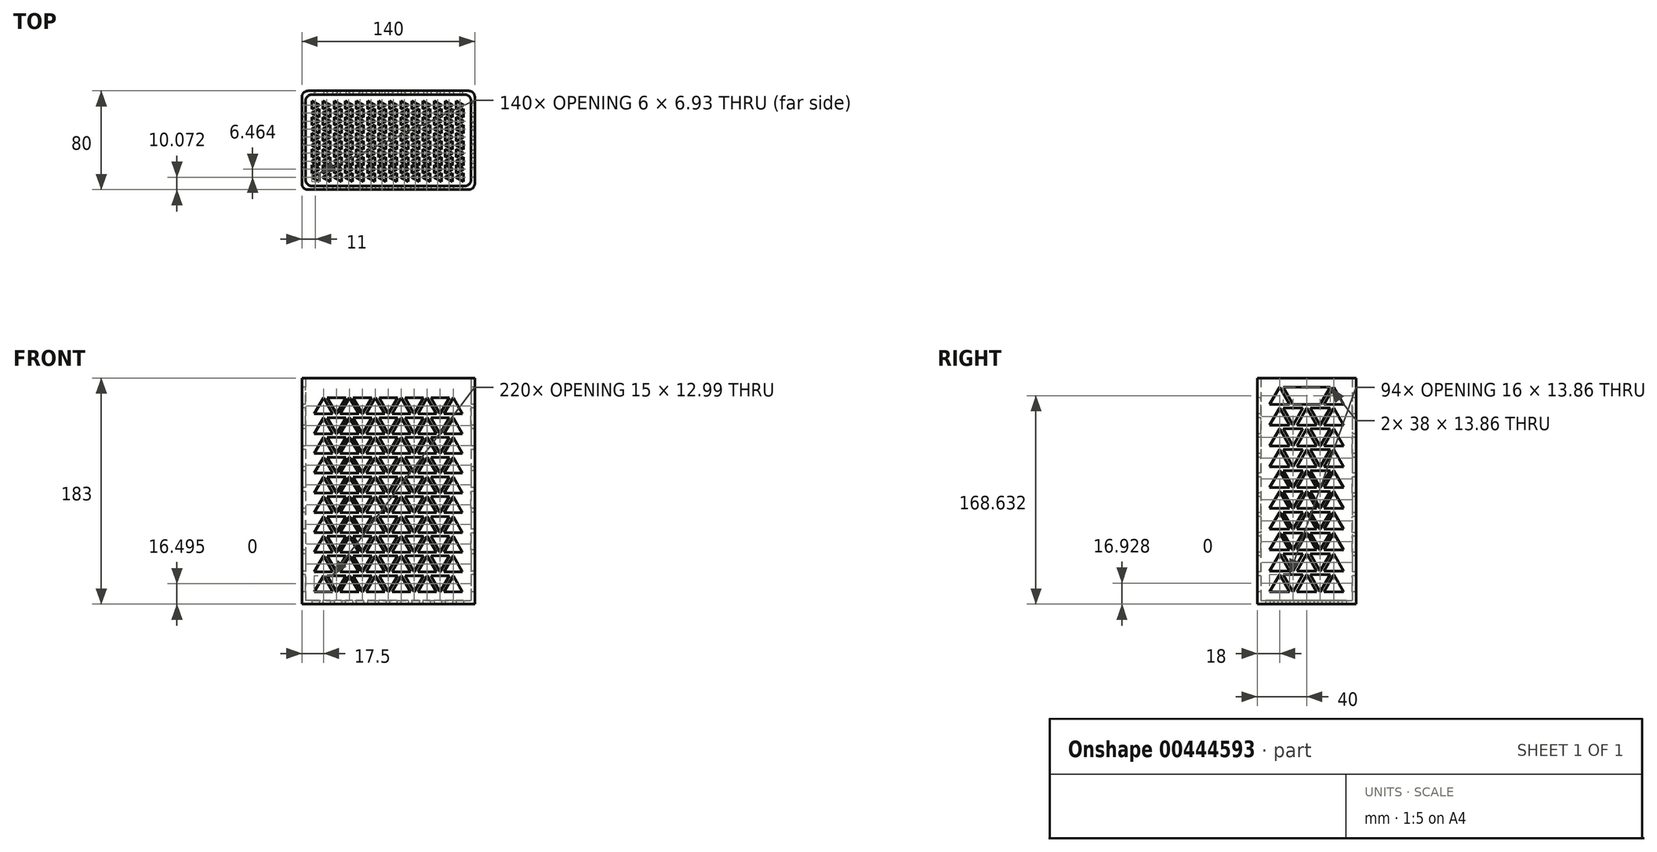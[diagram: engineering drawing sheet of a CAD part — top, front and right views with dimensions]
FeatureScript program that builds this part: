
annotation { "Feature Type Name" : "Feature", "Feature Type Description" : "" }
export const myFeature = defineFeature(function(context is Context, id is Id, definition is map)
    precondition{}
    {
        {
            var Q0;
            Q0=qCreatedBy(makeId("Top.planeOp"),FACE);
            var sketch = newSketch(context, id + "F0", { "sketchPlane" : qUnion([Q0])});
            skLineSegment(sketch, "E0.bottom", {"start": v(-70, 40) * mm, "end": v(70, 40) * mm});
            skLineSegment(sketch, "E0.top", {"start": v(-70, -40) * mm, "end": v(70, -40) * mm});
            skLineSegment(sketch, "E0.left", {"start": v(-70, 40) * mm, "end": v(-70, -40) * mm});
            skLineSegment(sketch, "E0.right", {"start": v(70, 40) * mm, "end": v(70, -40) * mm});
            skPoint(sketch, "E1", {"position": v(0, 40) * mm});
            skPoint(sketch, "E2", {"position": v(70, 0) * mm});
            skCircle(sketch, "E3.cCircle", {"center": v(-58, 22.07) * mm, "radius": 2 * mm, "construction": true});
            skLineSegment(sketch, "E3.0", {"start": v(-56, 25.54) * mm, "end": v(-56, 18.6) * mm});
            skLineSegment(sketch, "E3.1", {"start": v(-56, 18.6) * mm, "end": v(-62, 22.07) * mm});
            skLineSegment(sketch, "E3.2", {"start": v(-62, 22.07) * mm, "end": v(-56, 25.54) * mm});
            skPoint(sketch, "E3.0.midPoint", {"position": v(-56, 22.07) * mm});
            skCircle(sketch, "E4.cCircle", {"center": v(-60, 28.54) * mm, "radius": 2 * mm, "construction": true});
            skLineSegment(sketch, "E4.0", {"start": v(-62, 25.07) * mm, "end": v(-62, 32) * mm});
            skLineSegment(sketch, "E4.1", {"start": v(-62, 32) * mm, "end": v(-56, 28.54) * mm});
            skLineSegment(sketch, "E4.2", {"start": v(-56, 28.54) * mm, "end": v(-62, 25.07) * mm});
            skPoint(sketch, "E4.0.midPoint", {"position": v(-62, 28.54) * mm});
            skCircle(sketch, "E5.0.1.0", {"center": v(-58, 9.07) * mm, "radius": 2 * mm, "construction": true});
            skLineSegment(sketch, "E5.0.1.1", {"start": v(-56, 12.54) * mm, "end": v(-56, 5.6) * mm});
            skLineSegment(sketch, "E5.0.1.2", {"start": v(-56, 5.6) * mm, "end": v(-62, 9.07) * mm});
            skLineSegment(sketch, "E5.0.1.3", {"start": v(-62, 9.07) * mm, "end": v(-56, 12.54) * mm});
            skCircle(sketch, "E5.0.1.4", {"center": v(-60, 15.54) * mm, "radius": 2 * mm, "construction": true});
            skLineSegment(sketch, "E5.0.1.5", {"start": v(-62, 12.07) * mm, "end": v(-62, 19) * mm});
            skLineSegment(sketch, "E5.0.1.6", {"start": v(-62, 19) * mm, "end": v(-56, 15.54) * mm});
            skLineSegment(sketch, "E5.0.1.7", {"start": v(-56, 15.54) * mm, "end": v(-62, 12.07) * mm});
            skPoint(sketch, "E5.0.1.8", {"position": v(-62, 15.54) * mm});
            skPoint(sketch, "E5.0.1.9", {"position": v(-56, 9.07) * mm});
            skCircle(sketch, "E5.0.2.0", {"center": v(-58, -3.93) * mm, "radius": 2 * mm, "construction": true});
            skLineSegment(sketch, "E5.0.2.1", {"start": v(-56, -0.46) * mm, "end": v(-56, -7.4) * mm});
            skLineSegment(sketch, "E5.0.2.2", {"start": v(-56, -7.4) * mm, "end": v(-62, -3.93) * mm});
            skLineSegment(sketch, "E5.0.2.3", {"start": v(-62, -3.93) * mm, "end": v(-56, -0.46) * mm});
            skCircle(sketch, "E5.0.2.4", {"center": v(-60, 2.54) * mm, "radius": 2 * mm, "construction": true});
            skLineSegment(sketch, "E5.0.2.5", {"start": v(-62, -0.93) * mm, "end": v(-62, 6) * mm});
            skLineSegment(sketch, "E5.0.2.6", {"start": v(-62, 6) * mm, "end": v(-56, 2.54) * mm});
            skLineSegment(sketch, "E5.0.2.7", {"start": v(-56, 2.54) * mm, "end": v(-62, -0.93) * mm});
            skPoint(sketch, "E5.0.2.8", {"position": v(-62, 2.54) * mm});
            skPoint(sketch, "E5.0.2.9", {"position": v(-56, -3.93) * mm});
            skCircle(sketch, "E5.0.3.0", {"center": v(-58, -16.93) * mm, "radius": 2 * mm, "construction": true});
            skLineSegment(sketch, "E5.0.3.1", {"start": v(-56, -13.46) * mm, "end": v(-56, -20.4) * mm});
            skLineSegment(sketch, "E5.0.3.2", {"start": v(-56, -20.4) * mm, "end": v(-62, -16.93) * mm});
            skLineSegment(sketch, "E5.0.3.3", {"start": v(-62, -16.93) * mm, "end": v(-56, -13.46) * mm});
            skCircle(sketch, "E5.0.3.4", {"center": v(-60, -10.46) * mm, "radius": 2 * mm, "construction": true});
            skLineSegment(sketch, "E5.0.3.5", {"start": v(-62, -13.93) * mm, "end": v(-62, -7) * mm});
            skLineSegment(sketch, "E5.0.3.6", {"start": v(-62, -7) * mm, "end": v(-56, -10.46) * mm});
            skLineSegment(sketch, "E5.0.3.7", {"start": v(-56, -10.46) * mm, "end": v(-62, -13.93) * mm});
            skPoint(sketch, "E5.0.3.8", {"position": v(-62, -10.46) * mm});
            skPoint(sketch, "E5.0.3.9", {"position": v(-56, -16.93) * mm});
            skCircle(sketch, "E5.0.4.0", {"center": v(-58, -29.93) * mm, "radius": 2 * mm, "construction": true});
            skLineSegment(sketch, "E5.0.4.1", {"start": v(-56, -26.46) * mm, "end": v(-56, -33.4) * mm});
            skLineSegment(sketch, "E5.0.4.2", {"start": v(-56, -33.4) * mm, "end": v(-62, -29.93) * mm});
            skLineSegment(sketch, "E5.0.4.3", {"start": v(-62, -29.93) * mm, "end": v(-56, -26.46) * mm});
            skCircle(sketch, "E5.0.4.4", {"center": v(-60, -23.46) * mm, "radius": 2 * mm, "construction": true});
            skLineSegment(sketch, "E5.0.4.5", {"start": v(-62, -26.93) * mm, "end": v(-62, -20) * mm});
            skLineSegment(sketch, "E5.0.4.6", {"start": v(-62, -20) * mm, "end": v(-56, -23.46) * mm});
            skLineSegment(sketch, "E5.0.4.7", {"start": v(-56, -23.46) * mm, "end": v(-62, -26.93) * mm});
            skPoint(sketch, "E5.0.4.8", {"position": v(-62, -23.46) * mm});
            skPoint(sketch, "E5.0.4.9", {"position": v(-56, -29.93) * mm});
            skCircle(sketch, "E5.1.0.0", {"center": v(-49, 22.07) * mm, "radius": 2 * mm, "construction": true});
            skLineSegment(sketch, "E5.1.0.1", {"start": v(-47, 25.54) * mm, "end": v(-47, 18.6) * mm});
            skLineSegment(sketch, "E5.1.0.2", {"start": v(-47, 18.6) * mm, "end": v(-53, 22.07) * mm});
            skLineSegment(sketch, "E5.1.0.3", {"start": v(-53, 22.07) * mm, "end": v(-47, 25.54) * mm});
            skCircle(sketch, "E5.1.0.4", {"center": v(-51, 28.54) * mm, "radius": 2 * mm, "construction": true});
            skLineSegment(sketch, "E5.1.0.5", {"start": v(-53, 25.07) * mm, "end": v(-53, 32) * mm});
            skLineSegment(sketch, "E5.1.0.6", {"start": v(-53, 32) * mm, "end": v(-47, 28.54) * mm});
            skLineSegment(sketch, "E5.1.0.7", {"start": v(-47, 28.54) * mm, "end": v(-53, 25.07) * mm});
            skPoint(sketch, "E5.1.0.8", {"position": v(-53, 28.54) * mm});
            skPoint(sketch, "E5.1.0.9", {"position": v(-47, 22.07) * mm});
            skCircle(sketch, "E5.1.1.0", {"center": v(-49, 9.07) * mm, "radius": 2 * mm, "construction": true});
            skLineSegment(sketch, "E5.1.1.1", {"start": v(-47, 12.54) * mm, "end": v(-47, 5.6) * mm});
            skLineSegment(sketch, "E5.1.1.2", {"start": v(-47, 5.6) * mm, "end": v(-53, 9.07) * mm});
            skLineSegment(sketch, "E5.1.1.3", {"start": v(-53, 9.07) * mm, "end": v(-47, 12.54) * mm});
            skCircle(sketch, "E5.1.1.4", {"center": v(-51, 15.54) * mm, "radius": 2 * mm, "construction": true});
            skLineSegment(sketch, "E5.1.1.5", {"start": v(-53, 12.07) * mm, "end": v(-53, 19) * mm});
            skLineSegment(sketch, "E5.1.1.6", {"start": v(-53, 19) * mm, "end": v(-47, 15.54) * mm});
            skLineSegment(sketch, "E5.1.1.7", {"start": v(-47, 15.54) * mm, "end": v(-53, 12.07) * mm});
            skPoint(sketch, "E5.1.1.8", {"position": v(-53, 15.54) * mm});
            skPoint(sketch, "E5.1.1.9", {"position": v(-47, 9.07) * mm});
            skCircle(sketch, "E5.1.2.0", {"center": v(-49, -3.93) * mm, "radius": 2 * mm, "construction": true});
            skLineSegment(sketch, "E5.1.2.1", {"start": v(-47, -0.46) * mm, "end": v(-47, -7.4) * mm});
            skLineSegment(sketch, "E5.1.2.2", {"start": v(-47, -7.4) * mm, "end": v(-53, -3.93) * mm});
            skLineSegment(sketch, "E5.1.2.3", {"start": v(-53, -3.93) * mm, "end": v(-47, -0.46) * mm});
            skCircle(sketch, "E5.1.2.4", {"center": v(-51, 2.54) * mm, "radius": 2 * mm, "construction": true});
            skLineSegment(sketch, "E5.1.2.5", {"start": v(-53, -0.93) * mm, "end": v(-53, 6) * mm});
            skLineSegment(sketch, "E5.1.2.6", {"start": v(-53, 6) * mm, "end": v(-47, 2.54) * mm});
            skLineSegment(sketch, "E5.1.2.7", {"start": v(-47, 2.54) * mm, "end": v(-53, -0.93) * mm});
            skPoint(sketch, "E5.1.2.8", {"position": v(-53, 2.54) * mm});
            skPoint(sketch, "E5.1.2.9", {"position": v(-47, -3.93) * mm});
            skCircle(sketch, "E5.1.3.0", {"center": v(-49, -16.93) * mm, "radius": 2 * mm, "construction": true});
            skLineSegment(sketch, "E5.1.3.1", {"start": v(-47, -13.46) * mm, "end": v(-47, -20.4) * mm});
            skLineSegment(sketch, "E5.1.3.2", {"start": v(-47, -20.4) * mm, "end": v(-53, -16.93) * mm});
            skLineSegment(sketch, "E5.1.3.3", {"start": v(-53, -16.93) * mm, "end": v(-47, -13.46) * mm});
            skCircle(sketch, "E5.1.3.4", {"center": v(-51, -10.46) * mm, "radius": 2 * mm, "construction": true});
            skLineSegment(sketch, "E5.1.3.5", {"start": v(-53, -13.93) * mm, "end": v(-53, -7) * mm});
            skLineSegment(sketch, "E5.1.3.6", {"start": v(-53, -7) * mm, "end": v(-47, -10.46) * mm});
            skLineSegment(sketch, "E5.1.3.7", {"start": v(-47, -10.46) * mm, "end": v(-53, -13.93) * mm});
            skPoint(sketch, "E5.1.3.8", {"position": v(-53, -10.46) * mm});
            skPoint(sketch, "E5.1.3.9", {"position": v(-47, -16.93) * mm});
            skCircle(sketch, "E5.1.4.0", {"center": v(-49, -29.93) * mm, "radius": 2 * mm, "construction": true});
            skLineSegment(sketch, "E5.1.4.1", {"start": v(-47, -26.46) * mm, "end": v(-47, -33.4) * mm});
            skLineSegment(sketch, "E5.1.4.2", {"start": v(-47, -33.4) * mm, "end": v(-53, -29.93) * mm});
            skLineSegment(sketch, "E5.1.4.3", {"start": v(-53, -29.93) * mm, "end": v(-47, -26.46) * mm});
            skCircle(sketch, "E5.1.4.4", {"center": v(-51, -23.46) * mm, "radius": 2 * mm, "construction": true});
            skLineSegment(sketch, "E5.1.4.5", {"start": v(-53, -26.93) * mm, "end": v(-53, -20) * mm});
            skLineSegment(sketch, "E5.1.4.6", {"start": v(-53, -20) * mm, "end": v(-47, -23.46) * mm});
            skLineSegment(sketch, "E5.1.4.7", {"start": v(-47, -23.46) * mm, "end": v(-53, -26.93) * mm});
            skPoint(sketch, "E5.1.4.8", {"position": v(-53, -23.46) * mm});
            skPoint(sketch, "E5.1.4.9", {"position": v(-47, -29.93) * mm});
            skCircle(sketch, "E5.2.0.0", {"center": v(-40, 22.07) * mm, "radius": 2 * mm, "construction": true});
            skLineSegment(sketch, "E5.2.0.1", {"start": v(-38, 25.54) * mm, "end": v(-38, 18.6) * mm});
            skLineSegment(sketch, "E5.2.0.2", {"start": v(-38, 18.6) * mm, "end": v(-44, 22.07) * mm});
            skLineSegment(sketch, "E5.2.0.3", {"start": v(-44, 22.07) * mm, "end": v(-38, 25.54) * mm});
            skCircle(sketch, "E5.2.0.4", {"center": v(-42, 28.54) * mm, "radius": 2 * mm, "construction": true});
            skLineSegment(sketch, "E5.2.0.5", {"start": v(-44, 25.07) * mm, "end": v(-44, 32) * mm});
            skLineSegment(sketch, "E5.2.0.6", {"start": v(-44, 32) * mm, "end": v(-38, 28.54) * mm});
            skLineSegment(sketch, "E5.2.0.7", {"start": v(-38, 28.54) * mm, "end": v(-44, 25.07) * mm});
            skPoint(sketch, "E5.2.0.8", {"position": v(-44, 28.54) * mm});
            skPoint(sketch, "E5.2.0.9", {"position": v(-38, 22.07) * mm});
            skCircle(sketch, "E5.2.1.0", {"center": v(-40, 9.07) * mm, "radius": 2 * mm, "construction": true});
            skLineSegment(sketch, "E5.2.1.1", {"start": v(-38, 12.54) * mm, "end": v(-38, 5.6) * mm});
            skLineSegment(sketch, "E5.2.1.2", {"start": v(-38, 5.6) * mm, "end": v(-44, 9.07) * mm});
            skLineSegment(sketch, "E5.2.1.3", {"start": v(-44, 9.07) * mm, "end": v(-38, 12.54) * mm});
            skCircle(sketch, "E5.2.1.4", {"center": v(-42, 15.54) * mm, "radius": 2 * mm, "construction": true});
            skLineSegment(sketch, "E5.2.1.5", {"start": v(-44, 12.07) * mm, "end": v(-44, 19) * mm});
            skLineSegment(sketch, "E5.2.1.6", {"start": v(-44, 19) * mm, "end": v(-38, 15.54) * mm});
            skLineSegment(sketch, "E5.2.1.7", {"start": v(-38, 15.54) * mm, "end": v(-44, 12.07) * mm});
            skPoint(sketch, "E5.2.1.8", {"position": v(-44, 15.54) * mm});
            skPoint(sketch, "E5.2.1.9", {"position": v(-38, 9.07) * mm});
            skCircle(sketch, "E5.2.2.0", {"center": v(-40, -3.93) * mm, "radius": 2 * mm, "construction": true});
            skLineSegment(sketch, "E5.2.2.1", {"start": v(-38, -0.46) * mm, "end": v(-38, -7.4) * mm});
            skLineSegment(sketch, "E5.2.2.2", {"start": v(-38, -7.4) * mm, "end": v(-44, -3.93) * mm});
            skLineSegment(sketch, "E5.2.2.3", {"start": v(-44, -3.93) * mm, "end": v(-38, -0.46) * mm});
            skCircle(sketch, "E5.2.2.4", {"center": v(-42, 2.54) * mm, "radius": 2 * mm, "construction": true});
            skLineSegment(sketch, "E5.2.2.5", {"start": v(-44, -0.93) * mm, "end": v(-44, 6) * mm});
            skLineSegment(sketch, "E5.2.2.6", {"start": v(-44, 6) * mm, "end": v(-38, 2.54) * mm});
            skLineSegment(sketch, "E5.2.2.7", {"start": v(-38, 2.54) * mm, "end": v(-44, -0.93) * mm});
            skPoint(sketch, "E5.2.2.8", {"position": v(-44, 2.54) * mm});
            skPoint(sketch, "E5.2.2.9", {"position": v(-38, -3.93) * mm});
            skCircle(sketch, "E5.2.3.0", {"center": v(-40, -16.93) * mm, "radius": 2 * mm, "construction": true});
            skLineSegment(sketch, "E5.2.3.1", {"start": v(-38, -13.46) * mm, "end": v(-38, -20.4) * mm});
            skLineSegment(sketch, "E5.2.3.2", {"start": v(-38, -20.4) * mm, "end": v(-44, -16.93) * mm});
            skLineSegment(sketch, "E5.2.3.3", {"start": v(-44, -16.93) * mm, "end": v(-38, -13.46) * mm});
            skCircle(sketch, "E5.2.3.4", {"center": v(-42, -10.46) * mm, "radius": 2 * mm, "construction": true});
            skLineSegment(sketch, "E5.2.3.5", {"start": v(-44, -13.93) * mm, "end": v(-44, -7) * mm});
            skLineSegment(sketch, "E5.2.3.6", {"start": v(-44, -7) * mm, "end": v(-38, -10.46) * mm});
            skLineSegment(sketch, "E5.2.3.7", {"start": v(-38, -10.46) * mm, "end": v(-44, -13.93) * mm});
            skPoint(sketch, "E5.2.3.8", {"position": v(-44, -10.46) * mm});
            skPoint(sketch, "E5.2.3.9", {"position": v(-38, -16.93) * mm});
            skCircle(sketch, "E5.2.4.0", {"center": v(-40, -29.93) * mm, "radius": 2 * mm, "construction": true});
            skLineSegment(sketch, "E5.2.4.1", {"start": v(-38, -26.46) * mm, "end": v(-38, -33.4) * mm});
            skLineSegment(sketch, "E5.2.4.2", {"start": v(-38, -33.4) * mm, "end": v(-44, -29.93) * mm});
            skLineSegment(sketch, "E5.2.4.3", {"start": v(-44, -29.93) * mm, "end": v(-38, -26.46) * mm});
            skCircle(sketch, "E5.2.4.4", {"center": v(-42, -23.46) * mm, "radius": 2 * mm, "construction": true});
            skLineSegment(sketch, "E5.2.4.5", {"start": v(-44, -26.93) * mm, "end": v(-44, -20) * mm});
            skLineSegment(sketch, "E5.2.4.6", {"start": v(-44, -20) * mm, "end": v(-38, -23.46) * mm});
            skLineSegment(sketch, "E5.2.4.7", {"start": v(-38, -23.46) * mm, "end": v(-44, -26.93) * mm});
            skPoint(sketch, "E5.2.4.8", {"position": v(-44, -23.46) * mm});
            skPoint(sketch, "E5.2.4.9", {"position": v(-38, -29.93) * mm});
            skCircle(sketch, "E5.3.0.0", {"center": v(-31, 22.07) * mm, "radius": 2 * mm, "construction": true});
            skLineSegment(sketch, "E5.3.0.1", {"start": v(-29, 25.54) * mm, "end": v(-29, 18.6) * mm});
            skLineSegment(sketch, "E5.3.0.2", {"start": v(-29, 18.6) * mm, "end": v(-35, 22.07) * mm});
            skLineSegment(sketch, "E5.3.0.3", {"start": v(-35, 22.07) * mm, "end": v(-29, 25.54) * mm});
            skCircle(sketch, "E5.3.0.4", {"center": v(-33, 28.54) * mm, "radius": 2 * mm, "construction": true});
            skLineSegment(sketch, "E5.3.0.5", {"start": v(-35, 25.07) * mm, "end": v(-35, 32) * mm});
            skLineSegment(sketch, "E5.3.0.6", {"start": v(-35, 32) * mm, "end": v(-29, 28.54) * mm});
            skLineSegment(sketch, "E5.3.0.7", {"start": v(-29, 28.54) * mm, "end": v(-35, 25.07) * mm});
            skPoint(sketch, "E5.3.0.8", {"position": v(-35, 28.54) * mm});
            skPoint(sketch, "E5.3.0.9", {"position": v(-29, 22.07) * mm});
            skCircle(sketch, "E5.3.1.0", {"center": v(-31, 9.07) * mm, "radius": 2 * mm, "construction": true});
            skLineSegment(sketch, "E5.3.1.1", {"start": v(-29, 12.54) * mm, "end": v(-29, 5.6) * mm});
            skLineSegment(sketch, "E5.3.1.2", {"start": v(-29, 5.6) * mm, "end": v(-35, 9.07) * mm});
            skLineSegment(sketch, "E5.3.1.3", {"start": v(-35, 9.07) * mm, "end": v(-29, 12.54) * mm});
            skCircle(sketch, "E5.3.1.4", {"center": v(-33, 15.54) * mm, "radius": 2 * mm, "construction": true});
            skLineSegment(sketch, "E5.3.1.5", {"start": v(-35, 12.07) * mm, "end": v(-35, 19) * mm});
            skLineSegment(sketch, "E5.3.1.6", {"start": v(-35, 19) * mm, "end": v(-29, 15.54) * mm});
            skLineSegment(sketch, "E5.3.1.7", {"start": v(-29, 15.54) * mm, "end": v(-35, 12.07) * mm});
            skPoint(sketch, "E5.3.1.8", {"position": v(-35, 15.54) * mm});
            skPoint(sketch, "E5.3.1.9", {"position": v(-29, 9.07) * mm});
            skCircle(sketch, "E5.3.2.0", {"center": v(-31, -3.93) * mm, "radius": 2 * mm, "construction": true});
            skLineSegment(sketch, "E5.3.2.1", {"start": v(-29, -0.46) * mm, "end": v(-29, -7.4) * mm});
            skLineSegment(sketch, "E5.3.2.2", {"start": v(-29, -7.4) * mm, "end": v(-35, -3.93) * mm});
            skLineSegment(sketch, "E5.3.2.3", {"start": v(-35, -3.93) * mm, "end": v(-29, -0.46) * mm});
            skCircle(sketch, "E5.3.2.4", {"center": v(-33, 2.54) * mm, "radius": 2 * mm, "construction": true});
            skLineSegment(sketch, "E5.3.2.5", {"start": v(-35, -0.93) * mm, "end": v(-35, 6) * mm});
            skLineSegment(sketch, "E5.3.2.6", {"start": v(-35, 6) * mm, "end": v(-29, 2.54) * mm});
            skLineSegment(sketch, "E5.3.2.7", {"start": v(-29, 2.54) * mm, "end": v(-35, -0.93) * mm});
            skPoint(sketch, "E5.3.2.8", {"position": v(-35, 2.54) * mm});
            skPoint(sketch, "E5.3.2.9", {"position": v(-29, -3.93) * mm});
            skCircle(sketch, "E5.3.3.0", {"center": v(-31, -16.93) * mm, "radius": 2 * mm, "construction": true});
            skLineSegment(sketch, "E5.3.3.1", {"start": v(-29, -13.46) * mm, "end": v(-29, -20.4) * mm});
            skLineSegment(sketch, "E5.3.3.2", {"start": v(-29, -20.4) * mm, "end": v(-35, -16.93) * mm});
            skLineSegment(sketch, "E5.3.3.3", {"start": v(-35, -16.93) * mm, "end": v(-29, -13.46) * mm});
            skCircle(sketch, "E5.3.3.4", {"center": v(-33, -10.46) * mm, "radius": 2 * mm, "construction": true});
            skLineSegment(sketch, "E5.3.3.5", {"start": v(-35, -13.93) * mm, "end": v(-35, -7) * mm});
            skLineSegment(sketch, "E5.3.3.6", {"start": v(-35, -7) * mm, "end": v(-29, -10.46) * mm});
            skLineSegment(sketch, "E5.3.3.7", {"start": v(-29, -10.46) * mm, "end": v(-35, -13.93) * mm});
            skPoint(sketch, "E5.3.3.8", {"position": v(-35, -10.46) * mm});
            skPoint(sketch, "E5.3.3.9", {"position": v(-29, -16.93) * mm});
            skCircle(sketch, "E5.3.4.0", {"center": v(-31, -29.93) * mm, "radius": 2 * mm, "construction": true});
            skLineSegment(sketch, "E5.3.4.1", {"start": v(-29, -26.46) * mm, "end": v(-29, -33.4) * mm});
            skLineSegment(sketch, "E5.3.4.2", {"start": v(-29, -33.4) * mm, "end": v(-35, -29.93) * mm});
            skLineSegment(sketch, "E5.3.4.3", {"start": v(-35, -29.93) * mm, "end": v(-29, -26.46) * mm});
            skCircle(sketch, "E5.3.4.4", {"center": v(-33, -23.46) * mm, "radius": 2 * mm, "construction": true});
            skLineSegment(sketch, "E5.3.4.5", {"start": v(-35, -26.93) * mm, "end": v(-35, -20) * mm});
            skLineSegment(sketch, "E5.3.4.6", {"start": v(-35, -20) * mm, "end": v(-29, -23.46) * mm});
            skLineSegment(sketch, "E5.3.4.7", {"start": v(-29, -23.46) * mm, "end": v(-35, -26.93) * mm});
            skPoint(sketch, "E5.3.4.8", {"position": v(-35, -23.46) * mm});
            skPoint(sketch, "E5.3.4.9", {"position": v(-29, -29.93) * mm});
            skCircle(sketch, "E5.4.0.0", {"center": v(-22, 22.07) * mm, "radius": 2 * mm, "construction": true});
            skLineSegment(sketch, "E5.4.0.1", {"start": v(-20, 25.54) * mm, "end": v(-20, 18.6) * mm});
            skLineSegment(sketch, "E5.4.0.2", {"start": v(-20, 18.6) * mm, "end": v(-26, 22.07) * mm});
            skLineSegment(sketch, "E5.4.0.3", {"start": v(-26, 22.07) * mm, "end": v(-20, 25.54) * mm});
            skCircle(sketch, "E5.4.0.4", {"center": v(-24, 28.54) * mm, "radius": 2 * mm, "construction": true});
            skLineSegment(sketch, "E5.4.0.5", {"start": v(-26, 25.07) * mm, "end": v(-26, 32) * mm});
            skLineSegment(sketch, "E5.4.0.6", {"start": v(-26, 32) * mm, "end": v(-20, 28.54) * mm});
            skLineSegment(sketch, "E5.4.0.7", {"start": v(-20, 28.54) * mm, "end": v(-26, 25.07) * mm});
            skPoint(sketch, "E5.4.0.8", {"position": v(-26, 28.54) * mm});
            skPoint(sketch, "E5.4.0.9", {"position": v(-20, 22.07) * mm});
            skCircle(sketch, "E5.4.1.0", {"center": v(-22, 9.07) * mm, "radius": 2 * mm, "construction": true});
            skLineSegment(sketch, "E5.4.1.1", {"start": v(-20, 12.54) * mm, "end": v(-20, 5.6) * mm});
            skLineSegment(sketch, "E5.4.1.2", {"start": v(-20, 5.6) * mm, "end": v(-26, 9.07) * mm});
            skLineSegment(sketch, "E5.4.1.3", {"start": v(-26, 9.07) * mm, "end": v(-20, 12.54) * mm});
            skCircle(sketch, "E5.4.1.4", {"center": v(-24, 15.54) * mm, "radius": 2 * mm, "construction": true});
            skLineSegment(sketch, "E5.4.1.5", {"start": v(-26, 12.07) * mm, "end": v(-26, 19) * mm});
            skLineSegment(sketch, "E5.4.1.6", {"start": v(-26, 19) * mm, "end": v(-20, 15.54) * mm});
            skLineSegment(sketch, "E5.4.1.7", {"start": v(-20, 15.54) * mm, "end": v(-26, 12.07) * mm});
            skPoint(sketch, "E5.4.1.8", {"position": v(-26, 15.54) * mm});
            skPoint(sketch, "E5.4.1.9", {"position": v(-20, 9.07) * mm});
            skCircle(sketch, "E5.4.2.0", {"center": v(-22, -3.93) * mm, "radius": 2 * mm, "construction": true});
            skLineSegment(sketch, "E5.4.2.1", {"start": v(-20, -0.46) * mm, "end": v(-20, -7.4) * mm});
            skLineSegment(sketch, "E5.4.2.2", {"start": v(-20, -7.4) * mm, "end": v(-26, -3.93) * mm});
            skLineSegment(sketch, "E5.4.2.3", {"start": v(-26, -3.93) * mm, "end": v(-20, -0.46) * mm});
            skCircle(sketch, "E5.4.2.4", {"center": v(-24, 2.54) * mm, "radius": 2 * mm, "construction": true});
            skLineSegment(sketch, "E5.4.2.5", {"start": v(-26, -0.93) * mm, "end": v(-26, 6) * mm});
            skLineSegment(sketch, "E5.4.2.6", {"start": v(-26, 6) * mm, "end": v(-20, 2.54) * mm});
            skLineSegment(sketch, "E5.4.2.7", {"start": v(-20, 2.54) * mm, "end": v(-26, -0.93) * mm});
            skPoint(sketch, "E5.4.2.8", {"position": v(-26, 2.54) * mm});
            skPoint(sketch, "E5.4.2.9", {"position": v(-20, -3.93) * mm});
            skCircle(sketch, "E5.4.3.0", {"center": v(-22, -16.93) * mm, "radius": 2 * mm, "construction": true});
            skLineSegment(sketch, "E5.4.3.1", {"start": v(-20, -13.46) * mm, "end": v(-20, -20.4) * mm});
            skLineSegment(sketch, "E5.4.3.2", {"start": v(-20, -20.4) * mm, "end": v(-26, -16.93) * mm});
            skLineSegment(sketch, "E5.4.3.3", {"start": v(-26, -16.93) * mm, "end": v(-20, -13.46) * mm});
            skCircle(sketch, "E5.4.3.4", {"center": v(-24, -10.46) * mm, "radius": 2 * mm, "construction": true});
            skLineSegment(sketch, "E5.4.3.5", {"start": v(-26, -13.93) * mm, "end": v(-26, -7) * mm});
            skLineSegment(sketch, "E5.4.3.6", {"start": v(-26, -7) * mm, "end": v(-20, -10.46) * mm});
            skLineSegment(sketch, "E5.4.3.7", {"start": v(-20, -10.46) * mm, "end": v(-26, -13.93) * mm});
            skPoint(sketch, "E5.4.3.8", {"position": v(-26, -10.46) * mm});
            skPoint(sketch, "E5.4.3.9", {"position": v(-20, -16.93) * mm});
            skCircle(sketch, "E5.4.4.0", {"center": v(-22, -29.93) * mm, "radius": 2 * mm, "construction": true});
            skLineSegment(sketch, "E5.4.4.1", {"start": v(-20, -26.46) * mm, "end": v(-20, -33.4) * mm});
            skLineSegment(sketch, "E5.4.4.2", {"start": v(-20, -33.4) * mm, "end": v(-26, -29.93) * mm});
            skLineSegment(sketch, "E5.4.4.3", {"start": v(-26, -29.93) * mm, "end": v(-20, -26.46) * mm});
            skCircle(sketch, "E5.4.4.4", {"center": v(-24, -23.46) * mm, "radius": 2 * mm, "construction": true});
            skLineSegment(sketch, "E5.4.4.5", {"start": v(-26, -26.93) * mm, "end": v(-26, -20) * mm});
            skLineSegment(sketch, "E5.4.4.6", {"start": v(-26, -20) * mm, "end": v(-20, -23.46) * mm});
            skLineSegment(sketch, "E5.4.4.7", {"start": v(-20, -23.46) * mm, "end": v(-26, -26.93) * mm});
            skPoint(sketch, "E5.4.4.8", {"position": v(-26, -23.46) * mm});
            skPoint(sketch, "E5.4.4.9", {"position": v(-20, -29.93) * mm});
            skCircle(sketch, "E5.5.0.0", {"center": v(-13, 22.07) * mm, "radius": 2 * mm, "construction": true});
            skLineSegment(sketch, "E5.5.0.1", {"start": v(-11, 25.54) * mm, "end": v(-11, 18.6) * mm});
            skLineSegment(sketch, "E5.5.0.2", {"start": v(-11, 18.6) * mm, "end": v(-17, 22.07) * mm});
            skLineSegment(sketch, "E5.5.0.3", {"start": v(-17, 22.07) * mm, "end": v(-11, 25.54) * mm});
            skCircle(sketch, "E5.5.0.4", {"center": v(-15, 28.54) * mm, "radius": 2 * mm, "construction": true});
            skLineSegment(sketch, "E5.5.0.5", {"start": v(-17, 25.07) * mm, "end": v(-17, 32) * mm});
            skLineSegment(sketch, "E5.5.0.6", {"start": v(-17, 32) * mm, "end": v(-11, 28.54) * mm});
            skLineSegment(sketch, "E5.5.0.7", {"start": v(-11, 28.54) * mm, "end": v(-17, 25.07) * mm});
            skPoint(sketch, "E5.5.0.8", {"position": v(-17, 28.54) * mm});
            skPoint(sketch, "E5.5.0.9", {"position": v(-11, 22.07) * mm});
            skCircle(sketch, "E5.5.1.0", {"center": v(-13, 9.07) * mm, "radius": 2 * mm, "construction": true});
            skLineSegment(sketch, "E5.5.1.1", {"start": v(-11, 12.54) * mm, "end": v(-11, 5.6) * mm});
            skLineSegment(sketch, "E5.5.1.2", {"start": v(-11, 5.6) * mm, "end": v(-17, 9.07) * mm});
            skLineSegment(sketch, "E5.5.1.3", {"start": v(-17, 9.07) * mm, "end": v(-11, 12.54) * mm});
            skCircle(sketch, "E5.5.1.4", {"center": v(-15, 15.54) * mm, "radius": 2 * mm, "construction": true});
            skLineSegment(sketch, "E5.5.1.5", {"start": v(-17, 12.07) * mm, "end": v(-17, 19) * mm});
            skLineSegment(sketch, "E5.5.1.6", {"start": v(-17, 19) * mm, "end": v(-11, 15.54) * mm});
            skLineSegment(sketch, "E5.5.1.7", {"start": v(-11, 15.54) * mm, "end": v(-17, 12.07) * mm});
            skPoint(sketch, "E5.5.1.8", {"position": v(-17, 15.54) * mm});
            skPoint(sketch, "E5.5.1.9", {"position": v(-11, 9.07) * mm});
            skCircle(sketch, "E5.5.2.0", {"center": v(-13, -3.93) * mm, "radius": 2 * mm, "construction": true});
            skLineSegment(sketch, "E5.5.2.1", {"start": v(-11, -0.46) * mm, "end": v(-11, -7.4) * mm});
            skLineSegment(sketch, "E5.5.2.2", {"start": v(-11, -7.4) * mm, "end": v(-17, -3.93) * mm});
            skLineSegment(sketch, "E5.5.2.3", {"start": v(-17, -3.93) * mm, "end": v(-11, -0.46) * mm});
            skCircle(sketch, "E5.5.2.4", {"center": v(-15, 2.54) * mm, "radius": 2 * mm, "construction": true});
            skLineSegment(sketch, "E5.5.2.5", {"start": v(-17, -0.93) * mm, "end": v(-17, 6) * mm});
            skLineSegment(sketch, "E5.5.2.6", {"start": v(-17, 6) * mm, "end": v(-11, 2.54) * mm});
            skLineSegment(sketch, "E5.5.2.7", {"start": v(-11, 2.54) * mm, "end": v(-17, -0.93) * mm});
            skPoint(sketch, "E5.5.2.8", {"position": v(-17, 2.54) * mm});
            skPoint(sketch, "E5.5.2.9", {"position": v(-11, -3.93) * mm});
            skCircle(sketch, "E5.5.3.0", {"center": v(-13, -16.93) * mm, "radius": 2 * mm, "construction": true});
            skLineSegment(sketch, "E5.5.3.1", {"start": v(-11, -13.46) * mm, "end": v(-11, -20.4) * mm});
            skLineSegment(sketch, "E5.5.3.2", {"start": v(-11, -20.4) * mm, "end": v(-17, -16.93) * mm});
            skLineSegment(sketch, "E5.5.3.3", {"start": v(-17, -16.93) * mm, "end": v(-11, -13.46) * mm});
            skCircle(sketch, "E5.5.3.4", {"center": v(-15, -10.46) * mm, "radius": 2 * mm, "construction": true});
            skLineSegment(sketch, "E5.5.3.5", {"start": v(-17, -13.93) * mm, "end": v(-17, -7) * mm});
            skLineSegment(sketch, "E5.5.3.6", {"start": v(-17, -7) * mm, "end": v(-11, -10.46) * mm});
            skLineSegment(sketch, "E5.5.3.7", {"start": v(-11, -10.46) * mm, "end": v(-17, -13.93) * mm});
            skPoint(sketch, "E5.5.3.8", {"position": v(-17, -10.46) * mm});
            skPoint(sketch, "E5.5.3.9", {"position": v(-11, -16.93) * mm});
            skCircle(sketch, "E5.5.4.0", {"center": v(-13, -29.93) * mm, "radius": 2 * mm, "construction": true});
            skLineSegment(sketch, "E5.5.4.1", {"start": v(-11, -26.46) * mm, "end": v(-11, -33.4) * mm});
            skLineSegment(sketch, "E5.5.4.2", {"start": v(-11, -33.4) * mm, "end": v(-17, -29.93) * mm});
            skLineSegment(sketch, "E5.5.4.3", {"start": v(-17, -29.93) * mm, "end": v(-11, -26.46) * mm});
            skCircle(sketch, "E5.5.4.4", {"center": v(-15, -23.46) * mm, "radius": 2 * mm, "construction": true});
            skLineSegment(sketch, "E5.5.4.5", {"start": v(-17, -26.93) * mm, "end": v(-17, -20) * mm});
            skLineSegment(sketch, "E5.5.4.6", {"start": v(-17, -20) * mm, "end": v(-11, -23.46) * mm});
            skLineSegment(sketch, "E5.5.4.7", {"start": v(-11, -23.46) * mm, "end": v(-17, -26.93) * mm});
            skPoint(sketch, "E5.5.4.8", {"position": v(-17, -23.46) * mm});
            skPoint(sketch, "E5.5.4.9", {"position": v(-11, -29.93) * mm});
            skCircle(sketch, "E5.6.0.0", {"center": v(-4, 22.07) * mm, "radius": 2 * mm, "construction": true});
            skLineSegment(sketch, "E5.6.0.1", {"start": v(-2, 25.54) * mm, "end": v(-2, 18.6) * mm});
            skLineSegment(sketch, "E5.6.0.2", {"start": v(-2, 18.6) * mm, "end": v(-8, 22.07) * mm});
            skLineSegment(sketch, "E5.6.0.3", {"start": v(-8, 22.07) * mm, "end": v(-2, 25.54) * mm});
            skCircle(sketch, "E5.6.0.4", {"center": v(-6, 28.54) * mm, "radius": 2 * mm, "construction": true});
            skLineSegment(sketch, "E5.6.0.5", {"start": v(-8, 25.07) * mm, "end": v(-8, 32) * mm});
            skLineSegment(sketch, "E5.6.0.6", {"start": v(-8, 32) * mm, "end": v(-2, 28.54) * mm});
            skLineSegment(sketch, "E5.6.0.7", {"start": v(-2, 28.54) * mm, "end": v(-8, 25.07) * mm});
            skPoint(sketch, "E5.6.0.8", {"position": v(-8, 28.54) * mm});
            skPoint(sketch, "E5.6.0.9", {"position": v(-2, 22.07) * mm});
            skCircle(sketch, "E5.6.1.0", {"center": v(-4, 9.07) * mm, "radius": 2 * mm, "construction": true});
            skLineSegment(sketch, "E5.6.1.1", {"start": v(-2, 12.54) * mm, "end": v(-2, 5.6) * mm});
            skLineSegment(sketch, "E5.6.1.2", {"start": v(-2, 5.6) * mm, "end": v(-8, 9.07) * mm});
            skLineSegment(sketch, "E5.6.1.3", {"start": v(-8, 9.07) * mm, "end": v(-2, 12.54) * mm});
            skCircle(sketch, "E5.6.1.4", {"center": v(-6, 15.54) * mm, "radius": 2 * mm, "construction": true});
            skLineSegment(sketch, "E5.6.1.5", {"start": v(-8, 12.07) * mm, "end": v(-8, 19) * mm});
            skLineSegment(sketch, "E5.6.1.6", {"start": v(-8, 19) * mm, "end": v(-2, 15.54) * mm});
            skLineSegment(sketch, "E5.6.1.7", {"start": v(-2, 15.54) * mm, "end": v(-8, 12.07) * mm});
            skPoint(sketch, "E5.6.1.8", {"position": v(-8, 15.54) * mm});
            skPoint(sketch, "E5.6.1.9", {"position": v(-2, 9.07) * mm});
            skCircle(sketch, "E5.6.2.0", {"center": v(-4, -3.93) * mm, "radius": 2 * mm, "construction": true});
            skLineSegment(sketch, "E5.6.2.1", {"start": v(-2, -0.46) * mm, "end": v(-2, -7.4) * mm});
            skLineSegment(sketch, "E5.6.2.2", {"start": v(-2, -7.4) * mm, "end": v(-8, -3.93) * mm});
            skLineSegment(sketch, "E5.6.2.3", {"start": v(-8, -3.93) * mm, "end": v(-2, -0.46) * mm});
            skCircle(sketch, "E5.6.2.4", {"center": v(-6, 2.54) * mm, "radius": 2 * mm, "construction": true});
            skLineSegment(sketch, "E5.6.2.5", {"start": v(-8, -0.93) * mm, "end": v(-8, 6) * mm});
            skLineSegment(sketch, "E5.6.2.6", {"start": v(-8, 6) * mm, "end": v(-2, 2.54) * mm});
            skLineSegment(sketch, "E5.6.2.7", {"start": v(-2, 2.54) * mm, "end": v(-8, -0.93) * mm});
            skPoint(sketch, "E5.6.2.8", {"position": v(-8, 2.54) * mm});
            skPoint(sketch, "E5.6.2.9", {"position": v(-2, -3.93) * mm});
            skCircle(sketch, "E5.6.3.0", {"center": v(-4, -16.93) * mm, "radius": 2 * mm, "construction": true});
            skLineSegment(sketch, "E5.6.3.1", {"start": v(-2, -13.46) * mm, "end": v(-2, -20.4) * mm});
            skLineSegment(sketch, "E5.6.3.2", {"start": v(-2, -20.4) * mm, "end": v(-8, -16.93) * mm});
            skLineSegment(sketch, "E5.6.3.3", {"start": v(-8, -16.93) * mm, "end": v(-2, -13.46) * mm});
            skCircle(sketch, "E5.6.3.4", {"center": v(-6, -10.46) * mm, "radius": 2 * mm, "construction": true});
            skLineSegment(sketch, "E5.6.3.5", {"start": v(-8, -13.93) * mm, "end": v(-8, -7) * mm});
            skLineSegment(sketch, "E5.6.3.6", {"start": v(-8, -7) * mm, "end": v(-2, -10.46) * mm});
            skLineSegment(sketch, "E5.6.3.7", {"start": v(-2, -10.46) * mm, "end": v(-8, -13.93) * mm});
            skPoint(sketch, "E5.6.3.8", {"position": v(-8, -10.46) * mm});
            skPoint(sketch, "E5.6.3.9", {"position": v(-2, -16.93) * mm});
            skCircle(sketch, "E5.6.4.0", {"center": v(-4, -29.93) * mm, "radius": 2 * mm, "construction": true});
            skLineSegment(sketch, "E5.6.4.1", {"start": v(-2, -26.46) * mm, "end": v(-2, -33.4) * mm});
            skLineSegment(sketch, "E5.6.4.2", {"start": v(-2, -33.4) * mm, "end": v(-8, -29.93) * mm});
            skLineSegment(sketch, "E5.6.4.3", {"start": v(-8, -29.93) * mm, "end": v(-2, -26.46) * mm});
            skCircle(sketch, "E5.6.4.4", {"center": v(-6, -23.46) * mm, "radius": 2 * mm, "construction": true});
            skLineSegment(sketch, "E5.6.4.5", {"start": v(-8, -26.93) * mm, "end": v(-8, -20) * mm});
            skLineSegment(sketch, "E5.6.4.6", {"start": v(-8, -20) * mm, "end": v(-2, -23.46) * mm});
            skLineSegment(sketch, "E5.6.4.7", {"start": v(-2, -23.46) * mm, "end": v(-8, -26.93) * mm});
            skPoint(sketch, "E5.6.4.8", {"position": v(-8, -23.46) * mm});
            skPoint(sketch, "E5.6.4.9", {"position": v(-2, -29.93) * mm});
            skCircle(sketch, "E5.7.0.0", {"center": v(5, 22.07) * mm, "radius": 2 * mm, "construction": true});
            skLineSegment(sketch, "E5.7.0.1", {"start": v(7, 25.54) * mm, "end": v(7, 18.6) * mm});
            skLineSegment(sketch, "E5.7.0.2", {"start": v(7, 18.6) * mm, "end": v(1, 22.07) * mm});
            skLineSegment(sketch, "E5.7.0.3", {"start": v(1, 22.07) * mm, "end": v(7, 25.54) * mm});
            skCircle(sketch, "E5.7.0.4", {"center": v(3, 28.54) * mm, "radius": 2 * mm, "construction": true});
            skLineSegment(sketch, "E5.7.0.5", {"start": v(1, 25.07) * mm, "end": v(1, 32) * mm});
            skLineSegment(sketch, "E5.7.0.6", {"start": v(1, 32) * mm, "end": v(7, 28.54) * mm});
            skLineSegment(sketch, "E5.7.0.7", {"start": v(7, 28.54) * mm, "end": v(1, 25.07) * mm});
            skPoint(sketch, "E5.7.0.8", {"position": v(1, 28.54) * mm});
            skPoint(sketch, "E5.7.0.9", {"position": v(7, 22.07) * mm});
            skCircle(sketch, "E5.7.1.0", {"center": v(5, 9.07) * mm, "radius": 2 * mm, "construction": true});
            skLineSegment(sketch, "E5.7.1.1", {"start": v(7, 12.54) * mm, "end": v(7, 5.6) * mm});
            skLineSegment(sketch, "E5.7.1.2", {"start": v(7, 5.6) * mm, "end": v(1, 9.07) * mm});
            skLineSegment(sketch, "E5.7.1.3", {"start": v(1, 9.07) * mm, "end": v(7, 12.54) * mm});
            skCircle(sketch, "E5.7.1.4", {"center": v(3, 15.54) * mm, "radius": 2 * mm, "construction": true});
            skLineSegment(sketch, "E5.7.1.5", {"start": v(1, 12.07) * mm, "end": v(1, 19) * mm});
            skLineSegment(sketch, "E5.7.1.6", {"start": v(1, 19) * mm, "end": v(7, 15.54) * mm});
            skLineSegment(sketch, "E5.7.1.7", {"start": v(7, 15.54) * mm, "end": v(1, 12.07) * mm});
            skPoint(sketch, "E5.7.1.8", {"position": v(1, 15.54) * mm});
            skPoint(sketch, "E5.7.1.9", {"position": v(7, 9.07) * mm});
            skCircle(sketch, "E5.7.2.0", {"center": v(5, -3.93) * mm, "radius": 2 * mm, "construction": true});
            skLineSegment(sketch, "E5.7.2.1", {"start": v(7, -0.46) * mm, "end": v(7, -7.4) * mm});
            skLineSegment(sketch, "E5.7.2.2", {"start": v(7, -7.4) * mm, "end": v(1, -3.93) * mm});
            skLineSegment(sketch, "E5.7.2.3", {"start": v(1, -3.93) * mm, "end": v(7, -0.46) * mm});
            skCircle(sketch, "E5.7.2.4", {"center": v(3, 2.54) * mm, "radius": 2 * mm, "construction": true});
            skLineSegment(sketch, "E5.7.2.5", {"start": v(1, -0.93) * mm, "end": v(1, 6) * mm});
            skLineSegment(sketch, "E5.7.2.6", {"start": v(1, 6) * mm, "end": v(7, 2.54) * mm});
            skLineSegment(sketch, "E5.7.2.7", {"start": v(7, 2.54) * mm, "end": v(1, -0.93) * mm});
            skPoint(sketch, "E5.7.2.8", {"position": v(1, 2.54) * mm});
            skPoint(sketch, "E5.7.2.9", {"position": v(7, -3.93) * mm});
            skCircle(sketch, "E5.7.3.0", {"center": v(5, -16.93) * mm, "radius": 2 * mm, "construction": true});
            skLineSegment(sketch, "E5.7.3.1", {"start": v(7, -13.46) * mm, "end": v(7, -20.4) * mm});
            skLineSegment(sketch, "E5.7.3.2", {"start": v(7, -20.4) * mm, "end": v(1, -16.93) * mm});
            skLineSegment(sketch, "E5.7.3.3", {"start": v(1, -16.93) * mm, "end": v(7, -13.46) * mm});
            skCircle(sketch, "E5.7.3.4", {"center": v(3, -10.46) * mm, "radius": 2 * mm, "construction": true});
            skLineSegment(sketch, "E5.7.3.5", {"start": v(1, -13.93) * mm, "end": v(1, -7) * mm});
            skLineSegment(sketch, "E5.7.3.6", {"start": v(1, -7) * mm, "end": v(7, -10.46) * mm});
            skLineSegment(sketch, "E5.7.3.7", {"start": v(7, -10.46) * mm, "end": v(1, -13.93) * mm});
            skPoint(sketch, "E5.7.3.8", {"position": v(1, -10.46) * mm});
            skPoint(sketch, "E5.7.3.9", {"position": v(7, -16.93) * mm});
            skCircle(sketch, "E5.7.4.0", {"center": v(5, -29.93) * mm, "radius": 2 * mm, "construction": true});
            skLineSegment(sketch, "E5.7.4.1", {"start": v(7, -26.46) * mm, "end": v(7, -33.4) * mm});
            skLineSegment(sketch, "E5.7.4.2", {"start": v(7, -33.4) * mm, "end": v(1, -29.93) * mm});
            skLineSegment(sketch, "E5.7.4.3", {"start": v(1, -29.93) * mm, "end": v(7, -26.46) * mm});
            skCircle(sketch, "E5.7.4.4", {"center": v(3, -23.46) * mm, "radius": 2 * mm, "construction": true});
            skLineSegment(sketch, "E5.7.4.5", {"start": v(1, -26.93) * mm, "end": v(1, -20) * mm});
            skLineSegment(sketch, "E5.7.4.6", {"start": v(1, -20) * mm, "end": v(7, -23.46) * mm});
            skLineSegment(sketch, "E5.7.4.7", {"start": v(7, -23.46) * mm, "end": v(1, -26.93) * mm});
            skPoint(sketch, "E5.7.4.8", {"position": v(1, -23.46) * mm});
            skPoint(sketch, "E5.7.4.9", {"position": v(7, -29.93) * mm});
            skCircle(sketch, "E5.8.0.0", {"center": v(14, 22.07) * mm, "radius": 2 * mm, "construction": true});
            skLineSegment(sketch, "E5.8.0.1", {"start": v(16, 25.54) * mm, "end": v(16, 18.6) * mm});
            skLineSegment(sketch, "E5.8.0.2", {"start": v(16, 18.6) * mm, "end": v(10, 22.07) * mm});
            skLineSegment(sketch, "E5.8.0.3", {"start": v(10, 22.07) * mm, "end": v(16, 25.54) * mm});
            skCircle(sketch, "E5.8.0.4", {"center": v(12, 28.54) * mm, "radius": 2 * mm, "construction": true});
            skLineSegment(sketch, "E5.8.0.5", {"start": v(10, 25.07) * mm, "end": v(10, 32) * mm});
            skLineSegment(sketch, "E5.8.0.6", {"start": v(10, 32) * mm, "end": v(16, 28.54) * mm});
            skLineSegment(sketch, "E5.8.0.7", {"start": v(16, 28.54) * mm, "end": v(10, 25.07) * mm});
            skPoint(sketch, "E5.8.0.8", {"position": v(10, 28.54) * mm});
            skPoint(sketch, "E5.8.0.9", {"position": v(16, 22.07) * mm});
            skCircle(sketch, "E5.8.1.0", {"center": v(14, 9.07) * mm, "radius": 2 * mm, "construction": true});
            skLineSegment(sketch, "E5.8.1.1", {"start": v(16, 12.54) * mm, "end": v(16, 5.6) * mm});
            skLineSegment(sketch, "E5.8.1.2", {"start": v(16, 5.6) * mm, "end": v(10, 9.07) * mm});
            skLineSegment(sketch, "E5.8.1.3", {"start": v(10, 9.07) * mm, "end": v(16, 12.54) * mm});
            skCircle(sketch, "E5.8.1.4", {"center": v(12, 15.54) * mm, "radius": 2 * mm, "construction": true});
            skLineSegment(sketch, "E5.8.1.5", {"start": v(10, 12.07) * mm, "end": v(10, 19) * mm});
            skLineSegment(sketch, "E5.8.1.6", {"start": v(10, 19) * mm, "end": v(16, 15.54) * mm});
            skLineSegment(sketch, "E5.8.1.7", {"start": v(16, 15.54) * mm, "end": v(10, 12.07) * mm});
            skPoint(sketch, "E5.8.1.8", {"position": v(10, 15.54) * mm});
            skPoint(sketch, "E5.8.1.9", {"position": v(16, 9.07) * mm});
            skCircle(sketch, "E5.8.2.0", {"center": v(14, -3.93) * mm, "radius": 2 * mm, "construction": true});
            skLineSegment(sketch, "E5.8.2.1", {"start": v(16, -0.46) * mm, "end": v(16, -7.4) * mm});
            skLineSegment(sketch, "E5.8.2.2", {"start": v(16, -7.4) * mm, "end": v(10, -3.93) * mm});
            skLineSegment(sketch, "E5.8.2.3", {"start": v(10, -3.93) * mm, "end": v(16, -0.46) * mm});
            skCircle(sketch, "E5.8.2.4", {"center": v(12, 2.54) * mm, "radius": 2 * mm, "construction": true});
            skLineSegment(sketch, "E5.8.2.5", {"start": v(10, -0.93) * mm, "end": v(10, 6) * mm});
            skLineSegment(sketch, "E5.8.2.6", {"start": v(10, 6) * mm, "end": v(16, 2.54) * mm});
            skLineSegment(sketch, "E5.8.2.7", {"start": v(16, 2.54) * mm, "end": v(10, -0.93) * mm});
            skPoint(sketch, "E5.8.2.8", {"position": v(10, 2.54) * mm});
            skPoint(sketch, "E5.8.2.9", {"position": v(16, -3.93) * mm});
            skCircle(sketch, "E5.8.3.0", {"center": v(14, -16.93) * mm, "radius": 2 * mm, "construction": true});
            skLineSegment(sketch, "E5.8.3.1", {"start": v(16, -13.46) * mm, "end": v(16, -20.4) * mm});
            skLineSegment(sketch, "E5.8.3.2", {"start": v(16, -20.4) * mm, "end": v(10, -16.93) * mm});
            skLineSegment(sketch, "E5.8.3.3", {"start": v(10, -16.93) * mm, "end": v(16, -13.46) * mm});
            skCircle(sketch, "E5.8.3.4", {"center": v(12, -10.46) * mm, "radius": 2 * mm, "construction": true});
            skLineSegment(sketch, "E5.8.3.5", {"start": v(10, -13.93) * mm, "end": v(10, -7) * mm});
            skLineSegment(sketch, "E5.8.3.6", {"start": v(10, -7) * mm, "end": v(16, -10.46) * mm});
            skLineSegment(sketch, "E5.8.3.7", {"start": v(16, -10.46) * mm, "end": v(10, -13.93) * mm});
            skPoint(sketch, "E5.8.3.8", {"position": v(10, -10.46) * mm});
            skPoint(sketch, "E5.8.3.9", {"position": v(16, -16.93) * mm});
            skCircle(sketch, "E5.8.4.0", {"center": v(14, -29.93) * mm, "radius": 2 * mm, "construction": true});
            skLineSegment(sketch, "E5.8.4.1", {"start": v(16, -26.46) * mm, "end": v(16, -33.4) * mm});
            skLineSegment(sketch, "E5.8.4.2", {"start": v(16, -33.4) * mm, "end": v(10, -29.93) * mm});
            skLineSegment(sketch, "E5.8.4.3", {"start": v(10, -29.93) * mm, "end": v(16, -26.46) * mm});
            skCircle(sketch, "E5.8.4.4", {"center": v(12, -23.46) * mm, "radius": 2 * mm, "construction": true});
            skLineSegment(sketch, "E5.8.4.5", {"start": v(10, -26.93) * mm, "end": v(10, -20) * mm});
            skLineSegment(sketch, "E5.8.4.6", {"start": v(10, -20) * mm, "end": v(16, -23.46) * mm});
            skLineSegment(sketch, "E5.8.4.7", {"start": v(16, -23.46) * mm, "end": v(10, -26.93) * mm});
            skPoint(sketch, "E5.8.4.8", {"position": v(10, -23.46) * mm});
            skPoint(sketch, "E5.8.4.9", {"position": v(16, -29.93) * mm});
            skCircle(sketch, "E5.9.0.0", {"center": v(23, 22.07) * mm, "radius": 2 * mm, "construction": true});
            skLineSegment(sketch, "E5.9.0.1", {"start": v(25, 25.54) * mm, "end": v(25, 18.6) * mm});
            skLineSegment(sketch, "E5.9.0.2", {"start": v(25, 18.6) * mm, "end": v(19, 22.07) * mm});
            skLineSegment(sketch, "E5.9.0.3", {"start": v(19, 22.07) * mm, "end": v(25, 25.54) * mm});
            skCircle(sketch, "E5.9.0.4", {"center": v(21, 28.54) * mm, "radius": 2 * mm, "construction": true});
            skLineSegment(sketch, "E5.9.0.5", {"start": v(19, 25.07) * mm, "end": v(19, 32) * mm});
            skLineSegment(sketch, "E5.9.0.6", {"start": v(19, 32) * mm, "end": v(25, 28.54) * mm});
            skLineSegment(sketch, "E5.9.0.7", {"start": v(25, 28.54) * mm, "end": v(19, 25.07) * mm});
            skPoint(sketch, "E5.9.0.8", {"position": v(19, 28.54) * mm});
            skPoint(sketch, "E5.9.0.9", {"position": v(25, 22.07) * mm});
            skCircle(sketch, "E5.9.1.0", {"center": v(23, 9.07) * mm, "radius": 2 * mm, "construction": true});
            skLineSegment(sketch, "E5.9.1.1", {"start": v(25, 12.54) * mm, "end": v(25, 5.6) * mm});
            skLineSegment(sketch, "E5.9.1.2", {"start": v(25, 5.6) * mm, "end": v(19, 9.07) * mm});
            skLineSegment(sketch, "E5.9.1.3", {"start": v(19, 9.07) * mm, "end": v(25, 12.54) * mm});
            skCircle(sketch, "E5.9.1.4", {"center": v(21, 15.54) * mm, "radius": 2 * mm, "construction": true});
            skLineSegment(sketch, "E5.9.1.5", {"start": v(19, 12.07) * mm, "end": v(19, 19) * mm});
            skLineSegment(sketch, "E5.9.1.6", {"start": v(19, 19) * mm, "end": v(25, 15.54) * mm});
            skLineSegment(sketch, "E5.9.1.7", {"start": v(25, 15.54) * mm, "end": v(19, 12.07) * mm});
            skPoint(sketch, "E5.9.1.8", {"position": v(19, 15.54) * mm});
            skPoint(sketch, "E5.9.1.9", {"position": v(25, 9.07) * mm});
            skCircle(sketch, "E5.9.2.0", {"center": v(23, -3.93) * mm, "radius": 2 * mm, "construction": true});
            skLineSegment(sketch, "E5.9.2.1", {"start": v(25, -0.46) * mm, "end": v(25, -7.4) * mm});
            skLineSegment(sketch, "E5.9.2.2", {"start": v(25, -7.4) * mm, "end": v(19, -3.93) * mm});
            skLineSegment(sketch, "E5.9.2.3", {"start": v(19, -3.93) * mm, "end": v(25, -0.46) * mm});
            skCircle(sketch, "E5.9.2.4", {"center": v(21, 2.54) * mm, "radius": 2 * mm, "construction": true});
            skLineSegment(sketch, "E5.9.2.5", {"start": v(19, -0.93) * mm, "end": v(19, 6) * mm});
            skLineSegment(sketch, "E5.9.2.6", {"start": v(19, 6) * mm, "end": v(25, 2.54) * mm});
            skLineSegment(sketch, "E5.9.2.7", {"start": v(25, 2.54) * mm, "end": v(19, -0.93) * mm});
            skPoint(sketch, "E5.9.2.8", {"position": v(19, 2.54) * mm});
            skPoint(sketch, "E5.9.2.9", {"position": v(25, -3.93) * mm});
            skCircle(sketch, "E5.9.3.0", {"center": v(23, -16.93) * mm, "radius": 2 * mm, "construction": true});
            skLineSegment(sketch, "E5.9.3.1", {"start": v(25, -13.46) * mm, "end": v(25, -20.4) * mm});
            skLineSegment(sketch, "E5.9.3.2", {"start": v(25, -20.4) * mm, "end": v(19, -16.93) * mm});
            skLineSegment(sketch, "E5.9.3.3", {"start": v(19, -16.93) * mm, "end": v(25, -13.46) * mm});
            skCircle(sketch, "E5.9.3.4", {"center": v(21, -10.46) * mm, "radius": 2 * mm, "construction": true});
            skLineSegment(sketch, "E5.9.3.5", {"start": v(19, -13.93) * mm, "end": v(19, -7) * mm});
            skLineSegment(sketch, "E5.9.3.6", {"start": v(19, -7) * mm, "end": v(25, -10.46) * mm});
            skLineSegment(sketch, "E5.9.3.7", {"start": v(25, -10.46) * mm, "end": v(19, -13.93) * mm});
            skPoint(sketch, "E5.9.3.8", {"position": v(19, -10.46) * mm});
            skPoint(sketch, "E5.9.3.9", {"position": v(25, -16.93) * mm});
            skCircle(sketch, "E5.9.4.0", {"center": v(23, -29.93) * mm, "radius": 2 * mm, "construction": true});
            skLineSegment(sketch, "E5.9.4.1", {"start": v(25, -26.46) * mm, "end": v(25, -33.4) * mm});
            skLineSegment(sketch, "E5.9.4.2", {"start": v(25, -33.4) * mm, "end": v(19, -29.93) * mm});
            skLineSegment(sketch, "E5.9.4.3", {"start": v(19, -29.93) * mm, "end": v(25, -26.46) * mm});
            skCircle(sketch, "E5.9.4.4", {"center": v(21, -23.46) * mm, "radius": 2 * mm, "construction": true});
            skLineSegment(sketch, "E5.9.4.5", {"start": v(19, -26.93) * mm, "end": v(19, -20) * mm});
            skLineSegment(sketch, "E5.9.4.6", {"start": v(19, -20) * mm, "end": v(25, -23.46) * mm});
            skLineSegment(sketch, "E5.9.4.7", {"start": v(25, -23.46) * mm, "end": v(19, -26.93) * mm});
            skPoint(sketch, "E5.9.4.8", {"position": v(19, -23.46) * mm});
            skPoint(sketch, "E5.9.4.9", {"position": v(25, -29.93) * mm});
            skCircle(sketch, "E5.10.0.0", {"center": v(32, 22.07) * mm, "radius": 2 * mm, "construction": true});
            skLineSegment(sketch, "E5.10.0.1", {"start": v(34, 25.54) * mm, "end": v(34, 18.6) * mm});
            skLineSegment(sketch, "E5.10.0.2", {"start": v(34, 18.6) * mm, "end": v(28, 22.07) * mm});
            skLineSegment(sketch, "E5.10.0.3", {"start": v(28, 22.07) * mm, "end": v(34, 25.54) * mm});
            skCircle(sketch, "E5.10.0.4", {"center": v(30, 28.54) * mm, "radius": 2 * mm, "construction": true});
            skLineSegment(sketch, "E5.10.0.5", {"start": v(28, 25.07) * mm, "end": v(28, 32) * mm});
            skLineSegment(sketch, "E5.10.0.6", {"start": v(28, 32) * mm, "end": v(34, 28.54) * mm});
            skLineSegment(sketch, "E5.10.0.7", {"start": v(34, 28.54) * mm, "end": v(28, 25.07) * mm});
            skPoint(sketch, "E5.10.0.8", {"position": v(28, 28.54) * mm});
            skPoint(sketch, "E5.10.0.9", {"position": v(34, 22.07) * mm});
            skCircle(sketch, "E5.10.1.0", {"center": v(32, 9.07) * mm, "radius": 2 * mm, "construction": true});
            skLineSegment(sketch, "E5.10.1.1", {"start": v(34, 12.54) * mm, "end": v(34, 5.6) * mm});
            skLineSegment(sketch, "E5.10.1.2", {"start": v(34, 5.6) * mm, "end": v(28, 9.07) * mm});
            skLineSegment(sketch, "E5.10.1.3", {"start": v(28, 9.07) * mm, "end": v(34, 12.54) * mm});
            skCircle(sketch, "E5.10.1.4", {"center": v(30, 15.54) * mm, "radius": 2 * mm, "construction": true});
            skLineSegment(sketch, "E5.10.1.5", {"start": v(28, 12.07) * mm, "end": v(28, 19) * mm});
            skLineSegment(sketch, "E5.10.1.6", {"start": v(28, 19) * mm, "end": v(34, 15.54) * mm});
            skLineSegment(sketch, "E5.10.1.7", {"start": v(34, 15.54) * mm, "end": v(28, 12.07) * mm});
            skPoint(sketch, "E5.10.1.8", {"position": v(28, 15.54) * mm});
            skPoint(sketch, "E5.10.1.9", {"position": v(34, 9.07) * mm});
            skCircle(sketch, "E5.10.2.0", {"center": v(32, -3.93) * mm, "radius": 2 * mm, "construction": true});
            skLineSegment(sketch, "E5.10.2.1", {"start": v(34, -0.46) * mm, "end": v(34, -7.4) * mm});
            skLineSegment(sketch, "E5.10.2.2", {"start": v(34, -7.4) * mm, "end": v(28, -3.93) * mm});
            skLineSegment(sketch, "E5.10.2.3", {"start": v(28, -3.93) * mm, "end": v(34, -0.46) * mm});
            skCircle(sketch, "E5.10.2.4", {"center": v(30, 2.54) * mm, "radius": 2 * mm, "construction": true});
            skLineSegment(sketch, "E5.10.2.5", {"start": v(28, -0.93) * mm, "end": v(28, 6) * mm});
            skLineSegment(sketch, "E5.10.2.6", {"start": v(28, 6) * mm, "end": v(34, 2.54) * mm});
            skLineSegment(sketch, "E5.10.2.7", {"start": v(34, 2.54) * mm, "end": v(28, -0.93) * mm});
            skPoint(sketch, "E5.10.2.8", {"position": v(28, 2.54) * mm});
            skPoint(sketch, "E5.10.2.9", {"position": v(34, -3.93) * mm});
            skCircle(sketch, "E5.10.3.0", {"center": v(32, -16.93) * mm, "radius": 2 * mm, "construction": true});
            skLineSegment(sketch, "E5.10.3.1", {"start": v(34, -13.46) * mm, "end": v(34, -20.4) * mm});
            skLineSegment(sketch, "E5.10.3.2", {"start": v(34, -20.4) * mm, "end": v(28, -16.93) * mm});
            skLineSegment(sketch, "E5.10.3.3", {"start": v(28, -16.93) * mm, "end": v(34, -13.46) * mm});
            skCircle(sketch, "E5.10.3.4", {"center": v(30, -10.46) * mm, "radius": 2 * mm, "construction": true});
            skLineSegment(sketch, "E5.10.3.5", {"start": v(28, -13.93) * mm, "end": v(28, -7) * mm});
            skLineSegment(sketch, "E5.10.3.6", {"start": v(28, -7) * mm, "end": v(34, -10.46) * mm});
            skLineSegment(sketch, "E5.10.3.7", {"start": v(34, -10.46) * mm, "end": v(28, -13.93) * mm});
            skPoint(sketch, "E5.10.3.8", {"position": v(28, -10.46) * mm});
            skPoint(sketch, "E5.10.3.9", {"position": v(34, -16.93) * mm});
            skCircle(sketch, "E5.10.4.0", {"center": v(32, -29.93) * mm, "radius": 2 * mm, "construction": true});
            skLineSegment(sketch, "E5.10.4.1", {"start": v(34, -26.46) * mm, "end": v(34, -33.4) * mm});
            skLineSegment(sketch, "E5.10.4.2", {"start": v(34, -33.4) * mm, "end": v(28, -29.93) * mm});
            skLineSegment(sketch, "E5.10.4.3", {"start": v(28, -29.93) * mm, "end": v(34, -26.46) * mm});
            skCircle(sketch, "E5.10.4.4", {"center": v(30, -23.46) * mm, "radius": 2 * mm, "construction": true});
            skLineSegment(sketch, "E5.10.4.5", {"start": v(28, -26.93) * mm, "end": v(28, -20) * mm});
            skLineSegment(sketch, "E5.10.4.6", {"start": v(28, -20) * mm, "end": v(34, -23.46) * mm});
            skLineSegment(sketch, "E5.10.4.7", {"start": v(34, -23.46) * mm, "end": v(28, -26.93) * mm});
            skPoint(sketch, "E5.10.4.8", {"position": v(28, -23.46) * mm});
            skPoint(sketch, "E5.10.4.9", {"position": v(34, -29.93) * mm});
            skCircle(sketch, "E5.11.0.0", {"center": v(41, 22.07) * mm, "radius": 2 * mm, "construction": true});
            skLineSegment(sketch, "E5.11.0.1", {"start": v(43, 25.54) * mm, "end": v(43, 18.6) * mm});
            skLineSegment(sketch, "E5.11.0.2", {"start": v(43, 18.6) * mm, "end": v(37, 22.07) * mm});
            skLineSegment(sketch, "E5.11.0.3", {"start": v(37, 22.07) * mm, "end": v(43, 25.54) * mm});
            skCircle(sketch, "E5.11.0.4", {"center": v(39, 28.54) * mm, "radius": 2 * mm, "construction": true});
            skLineSegment(sketch, "E5.11.0.5", {"start": v(37, 25.07) * mm, "end": v(37, 32) * mm});
            skLineSegment(sketch, "E5.11.0.6", {"start": v(37, 32) * mm, "end": v(43, 28.54) * mm});
            skLineSegment(sketch, "E5.11.0.7", {"start": v(43, 28.54) * mm, "end": v(37, 25.07) * mm});
            skPoint(sketch, "E5.11.0.8", {"position": v(37, 28.54) * mm});
            skPoint(sketch, "E5.11.0.9", {"position": v(43, 22.07) * mm});
            skCircle(sketch, "E5.11.1.0", {"center": v(41, 9.07) * mm, "radius": 2 * mm, "construction": true});
            skLineSegment(sketch, "E5.11.1.1", {"start": v(43, 12.54) * mm, "end": v(43, 5.6) * mm});
            skLineSegment(sketch, "E5.11.1.2", {"start": v(43, 5.6) * mm, "end": v(37, 9.07) * mm});
            skLineSegment(sketch, "E5.11.1.3", {"start": v(37, 9.07) * mm, "end": v(43, 12.54) * mm});
            skCircle(sketch, "E5.11.1.4", {"center": v(39, 15.54) * mm, "radius": 2 * mm, "construction": true});
            skLineSegment(sketch, "E5.11.1.5", {"start": v(37, 12.07) * mm, "end": v(37, 19) * mm});
            skLineSegment(sketch, "E5.11.1.6", {"start": v(37, 19) * mm, "end": v(43, 15.54) * mm});
            skLineSegment(sketch, "E5.11.1.7", {"start": v(43, 15.54) * mm, "end": v(37, 12.07) * mm});
            skPoint(sketch, "E5.11.1.8", {"position": v(37, 15.54) * mm});
            skPoint(sketch, "E5.11.1.9", {"position": v(43, 9.07) * mm});
            skCircle(sketch, "E5.11.2.0", {"center": v(41, -3.93) * mm, "radius": 2 * mm, "construction": true});
            skLineSegment(sketch, "E5.11.2.1", {"start": v(43, -0.46) * mm, "end": v(43, -7.4) * mm});
            skLineSegment(sketch, "E5.11.2.2", {"start": v(43, -7.4) * mm, "end": v(37, -3.93) * mm});
            skLineSegment(sketch, "E5.11.2.3", {"start": v(37, -3.93) * mm, "end": v(43, -0.46) * mm});
            skCircle(sketch, "E5.11.2.4", {"center": v(39, 2.54) * mm, "radius": 2 * mm, "construction": true});
            skLineSegment(sketch, "E5.11.2.5", {"start": v(37, -0.93) * mm, "end": v(37, 6) * mm});
            skLineSegment(sketch, "E5.11.2.6", {"start": v(37, 6) * mm, "end": v(43, 2.54) * mm});
            skLineSegment(sketch, "E5.11.2.7", {"start": v(43, 2.54) * mm, "end": v(37, -0.93) * mm});
            skPoint(sketch, "E5.11.2.8", {"position": v(37, 2.54) * mm});
            skPoint(sketch, "E5.11.2.9", {"position": v(43, -3.93) * mm});
            skCircle(sketch, "E5.11.3.0", {"center": v(41, -16.93) * mm, "radius": 2 * mm, "construction": true});
            skLineSegment(sketch, "E5.11.3.1", {"start": v(43, -13.46) * mm, "end": v(43, -20.4) * mm});
            skLineSegment(sketch, "E5.11.3.2", {"start": v(43, -20.4) * mm, "end": v(37, -16.93) * mm});
            skLineSegment(sketch, "E5.11.3.3", {"start": v(37, -16.93) * mm, "end": v(43, -13.46) * mm});
            skCircle(sketch, "E5.11.3.4", {"center": v(39, -10.46) * mm, "radius": 2 * mm, "construction": true});
            skLineSegment(sketch, "E5.11.3.5", {"start": v(37, -13.93) * mm, "end": v(37, -7) * mm});
            skLineSegment(sketch, "E5.11.3.6", {"start": v(37, -7) * mm, "end": v(43, -10.46) * mm});
            skLineSegment(sketch, "E5.11.3.7", {"start": v(43, -10.46) * mm, "end": v(37, -13.93) * mm});
            skPoint(sketch, "E5.11.3.8", {"position": v(37, -10.46) * mm});
            skPoint(sketch, "E5.11.3.9", {"position": v(43, -16.93) * mm});
            skCircle(sketch, "E5.11.4.0", {"center": v(41, -29.93) * mm, "radius": 2 * mm, "construction": true});
            skLineSegment(sketch, "E5.11.4.1", {"start": v(43, -26.46) * mm, "end": v(43, -33.4) * mm});
            skLineSegment(sketch, "E5.11.4.2", {"start": v(43, -33.4) * mm, "end": v(37, -29.93) * mm});
            skLineSegment(sketch, "E5.11.4.3", {"start": v(37, -29.93) * mm, "end": v(43, -26.46) * mm});
            skCircle(sketch, "E5.11.4.4", {"center": v(39, -23.46) * mm, "radius": 2 * mm, "construction": true});
            skLineSegment(sketch, "E5.11.4.5", {"start": v(37, -26.93) * mm, "end": v(37, -20) * mm});
            skLineSegment(sketch, "E5.11.4.6", {"start": v(37, -20) * mm, "end": v(43, -23.46) * mm});
            skLineSegment(sketch, "E5.11.4.7", {"start": v(43, -23.46) * mm, "end": v(37, -26.93) * mm});
            skPoint(sketch, "E5.11.4.8", {"position": v(37, -23.46) * mm});
            skPoint(sketch, "E5.11.4.9", {"position": v(43, -29.93) * mm});
            skCircle(sketch, "E5.12.0.0", {"center": v(50, 22.07) * mm, "radius": 2 * mm, "construction": true});
            skLineSegment(sketch, "E5.12.0.1", {"start": v(52, 25.54) * mm, "end": v(52, 18.6) * mm});
            skLineSegment(sketch, "E5.12.0.2", {"start": v(52, 18.6) * mm, "end": v(46, 22.07) * mm});
            skLineSegment(sketch, "E5.12.0.3", {"start": v(46, 22.07) * mm, "end": v(52, 25.54) * mm});
            skCircle(sketch, "E5.12.0.4", {"center": v(48, 28.54) * mm, "radius": 2 * mm, "construction": true});
            skLineSegment(sketch, "E5.12.0.5", {"start": v(46, 25.07) * mm, "end": v(46, 32) * mm});
            skLineSegment(sketch, "E5.12.0.6", {"start": v(46, 32) * mm, "end": v(52, 28.54) * mm});
            skLineSegment(sketch, "E5.12.0.7", {"start": v(52, 28.54) * mm, "end": v(46, 25.07) * mm});
            skPoint(sketch, "E5.12.0.8", {"position": v(46, 28.54) * mm});
            skPoint(sketch, "E5.12.0.9", {"position": v(52, 22.07) * mm});
            skCircle(sketch, "E5.12.1.0", {"center": v(50, 9.07) * mm, "radius": 2 * mm, "construction": true});
            skLineSegment(sketch, "E5.12.1.1", {"start": v(52, 12.54) * mm, "end": v(52, 5.6) * mm});
            skLineSegment(sketch, "E5.12.1.2", {"start": v(52, 5.6) * mm, "end": v(46, 9.07) * mm});
            skLineSegment(sketch, "E5.12.1.3", {"start": v(46, 9.07) * mm, "end": v(52, 12.54) * mm});
            skCircle(sketch, "E5.12.1.4", {"center": v(48, 15.54) * mm, "radius": 2 * mm, "construction": true});
            skLineSegment(sketch, "E5.12.1.5", {"start": v(46, 12.07) * mm, "end": v(46, 19) * mm});
            skLineSegment(sketch, "E5.12.1.6", {"start": v(46, 19) * mm, "end": v(52, 15.54) * mm});
            skLineSegment(sketch, "E5.12.1.7", {"start": v(52, 15.54) * mm, "end": v(46, 12.07) * mm});
            skPoint(sketch, "E5.12.1.8", {"position": v(46, 15.54) * mm});
            skPoint(sketch, "E5.12.1.9", {"position": v(52, 9.07) * mm});
            skCircle(sketch, "E5.12.2.0", {"center": v(50, -3.93) * mm, "radius": 2 * mm, "construction": true});
            skLineSegment(sketch, "E5.12.2.1", {"start": v(52, -0.46) * mm, "end": v(52, -7.4) * mm});
            skLineSegment(sketch, "E5.12.2.2", {"start": v(52, -7.4) * mm, "end": v(46, -3.93) * mm});
            skLineSegment(sketch, "E5.12.2.3", {"start": v(46, -3.93) * mm, "end": v(52, -0.46) * mm});
            skCircle(sketch, "E5.12.2.4", {"center": v(48, 2.54) * mm, "radius": 2 * mm, "construction": true});
            skLineSegment(sketch, "E5.12.2.5", {"start": v(46, -0.93) * mm, "end": v(46, 6) * mm});
            skLineSegment(sketch, "E5.12.2.6", {"start": v(46, 6) * mm, "end": v(52, 2.54) * mm});
            skLineSegment(sketch, "E5.12.2.7", {"start": v(52, 2.54) * mm, "end": v(46, -0.93) * mm});
            skPoint(sketch, "E5.12.2.8", {"position": v(46, 2.54) * mm});
            skPoint(sketch, "E5.12.2.9", {"position": v(52, -3.93) * mm});
            skCircle(sketch, "E5.12.3.0", {"center": v(50, -16.93) * mm, "radius": 2 * mm, "construction": true});
            skLineSegment(sketch, "E5.12.3.1", {"start": v(52, -13.46) * mm, "end": v(52, -20.4) * mm});
            skLineSegment(sketch, "E5.12.3.2", {"start": v(52, -20.4) * mm, "end": v(46, -16.93) * mm});
            skLineSegment(sketch, "E5.12.3.3", {"start": v(46, -16.93) * mm, "end": v(52, -13.46) * mm});
            skCircle(sketch, "E5.12.3.4", {"center": v(48, -10.46) * mm, "radius": 2 * mm, "construction": true});
            skLineSegment(sketch, "E5.12.3.5", {"start": v(46, -13.93) * mm, "end": v(46, -7) * mm});
            skLineSegment(sketch, "E5.12.3.6", {"start": v(46, -7) * mm, "end": v(52, -10.46) * mm});
            skLineSegment(sketch, "E5.12.3.7", {"start": v(52, -10.46) * mm, "end": v(46, -13.93) * mm});
            skPoint(sketch, "E5.12.3.8", {"position": v(46, -10.46) * mm});
            skPoint(sketch, "E5.12.3.9", {"position": v(52, -16.93) * mm});
            skCircle(sketch, "E5.12.4.0", {"center": v(50, -29.93) * mm, "radius": 2 * mm, "construction": true});
            skLineSegment(sketch, "E5.12.4.1", {"start": v(52, -26.46) * mm, "end": v(52, -33.4) * mm});
            skLineSegment(sketch, "E5.12.4.2", {"start": v(52, -33.4) * mm, "end": v(46, -29.93) * mm});
            skLineSegment(sketch, "E5.12.4.3", {"start": v(46, -29.93) * mm, "end": v(52, -26.46) * mm});
            skCircle(sketch, "E5.12.4.4", {"center": v(48, -23.46) * mm, "radius": 2 * mm, "construction": true});
            skLineSegment(sketch, "E5.12.4.5", {"start": v(46, -26.93) * mm, "end": v(46, -20) * mm});
            skLineSegment(sketch, "E5.12.4.6", {"start": v(46, -20) * mm, "end": v(52, -23.46) * mm});
            skLineSegment(sketch, "E5.12.4.7", {"start": v(52, -23.46) * mm, "end": v(46, -26.93) * mm});
            skPoint(sketch, "E5.12.4.8", {"position": v(46, -23.46) * mm});
            skPoint(sketch, "E5.12.4.9", {"position": v(52, -29.93) * mm});
            skCircle(sketch, "E5.13.0.0", {"center": v(59, 22.07) * mm, "radius": 2 * mm, "construction": true});
            skLineSegment(sketch, "E5.13.0.1", {"start": v(61, 25.54) * mm, "end": v(61, 18.6) * mm});
            skLineSegment(sketch, "E5.13.0.2", {"start": v(61, 18.6) * mm, "end": v(55, 22.07) * mm});
            skLineSegment(sketch, "E5.13.0.3", {"start": v(55, 22.07) * mm, "end": v(61, 25.54) * mm});
            skCircle(sketch, "E5.13.0.4", {"center": v(57, 28.54) * mm, "radius": 2 * mm, "construction": true});
            skLineSegment(sketch, "E5.13.0.5", {"start": v(55, 25.07) * mm, "end": v(55, 32) * mm});
            skLineSegment(sketch, "E5.13.0.6", {"start": v(55, 32) * mm, "end": v(61, 28.54) * mm});
            skLineSegment(sketch, "E5.13.0.7", {"start": v(61, 28.54) * mm, "end": v(55, 25.07) * mm});
            skPoint(sketch, "E5.13.0.8", {"position": v(55, 28.54) * mm});
            skPoint(sketch, "E5.13.0.9", {"position": v(61, 22.07) * mm});
            skCircle(sketch, "E5.13.1.0", {"center": v(59, 9.07) * mm, "radius": 2 * mm, "construction": true});
            skLineSegment(sketch, "E5.13.1.1", {"start": v(61, 12.54) * mm, "end": v(61, 5.6) * mm});
            skLineSegment(sketch, "E5.13.1.2", {"start": v(61, 5.6) * mm, "end": v(55, 9.07) * mm});
            skLineSegment(sketch, "E5.13.1.3", {"start": v(55, 9.07) * mm, "end": v(61, 12.54) * mm});
            skCircle(sketch, "E5.13.1.4", {"center": v(57, 15.54) * mm, "radius": 2 * mm, "construction": true});
            skLineSegment(sketch, "E5.13.1.5", {"start": v(55, 12.07) * mm, "end": v(55, 19) * mm});
            skLineSegment(sketch, "E5.13.1.6", {"start": v(55, 19) * mm, "end": v(61, 15.54) * mm});
            skLineSegment(sketch, "E5.13.1.7", {"start": v(61, 15.54) * mm, "end": v(55, 12.07) * mm});
            skPoint(sketch, "E5.13.1.8", {"position": v(55, 15.54) * mm});
            skPoint(sketch, "E5.13.1.9", {"position": v(61, 9.07) * mm});
            skCircle(sketch, "E5.13.2.0", {"center": v(59, -3.93) * mm, "radius": 2 * mm, "construction": true});
            skLineSegment(sketch, "E5.13.2.1", {"start": v(61, -0.46) * mm, "end": v(61, -7.4) * mm});
            skLineSegment(sketch, "E5.13.2.2", {"start": v(61, -7.4) * mm, "end": v(55, -3.93) * mm});
            skLineSegment(sketch, "E5.13.2.3", {"start": v(55, -3.93) * mm, "end": v(61, -0.46) * mm});
            skCircle(sketch, "E5.13.2.4", {"center": v(57, 2.54) * mm, "radius": 2 * mm, "construction": true});
            skLineSegment(sketch, "E5.13.2.5", {"start": v(55, -0.93) * mm, "end": v(55, 6) * mm});
            skLineSegment(sketch, "E5.13.2.6", {"start": v(55, 6) * mm, "end": v(61, 2.54) * mm});
            skLineSegment(sketch, "E5.13.2.7", {"start": v(61, 2.54) * mm, "end": v(55, -0.93) * mm});
            skPoint(sketch, "E5.13.2.8", {"position": v(55, 2.54) * mm});
            skPoint(sketch, "E5.13.2.9", {"position": v(61, -3.93) * mm});
            skCircle(sketch, "E5.13.3.0", {"center": v(59, -16.93) * mm, "radius": 2 * mm, "construction": true});
            skLineSegment(sketch, "E5.13.3.1", {"start": v(61, -13.46) * mm, "end": v(61, -20.4) * mm});
            skLineSegment(sketch, "E5.13.3.2", {"start": v(61, -20.4) * mm, "end": v(55, -16.93) * mm});
            skLineSegment(sketch, "E5.13.3.3", {"start": v(55, -16.93) * mm, "end": v(61, -13.46) * mm});
            skCircle(sketch, "E5.13.3.4", {"center": v(57, -10.46) * mm, "radius": 2 * mm, "construction": true});
            skLineSegment(sketch, "E5.13.3.5", {"start": v(55, -13.93) * mm, "end": v(55, -7) * mm});
            skLineSegment(sketch, "E5.13.3.6", {"start": v(55, -7) * mm, "end": v(61, -10.46) * mm});
            skLineSegment(sketch, "E5.13.3.7", {"start": v(61, -10.46) * mm, "end": v(55, -13.93) * mm});
            skPoint(sketch, "E5.13.3.8", {"position": v(55, -10.46) * mm});
            skPoint(sketch, "E5.13.3.9", {"position": v(61, -16.93) * mm});
            skCircle(sketch, "E5.13.4.0", {"center": v(59, -29.93) * mm, "radius": 2 * mm, "construction": true});
            skLineSegment(sketch, "E5.13.4.1", {"start": v(61, -26.46) * mm, "end": v(61, -33.4) * mm});
            skLineSegment(sketch, "E5.13.4.2", {"start": v(61, -33.4) * mm, "end": v(55, -29.93) * mm});
            skLineSegment(sketch, "E5.13.4.3", {"start": v(55, -29.93) * mm, "end": v(61, -26.46) * mm});
            skCircle(sketch, "E5.13.4.4", {"center": v(57, -23.46) * mm, "radius": 2 * mm, "construction": true});
            skLineSegment(sketch, "E5.13.4.5", {"start": v(55, -26.93) * mm, "end": v(55, -20) * mm});
            skLineSegment(sketch, "E5.13.4.6", {"start": v(55, -20) * mm, "end": v(61, -23.46) * mm});
            skLineSegment(sketch, "E5.13.4.7", {"start": v(61, -23.46) * mm, "end": v(55, -26.93) * mm});
            skPoint(sketch, "E5.13.4.8", {"position": v(55, -23.46) * mm});
            skPoint(sketch, "E5.13.4.9", {"position": v(61, -29.93) * mm});
            skLineSegment(sketch, "E5.direction1", {"start": v(-62, 22.07) * mm, "end": v(-53, 22.07) * mm, "construction": true});
            skLineSegment(sketch, "E5.direction2", {"start": v(-62, 22.07) * mm, "end": v(-62, 9.07) * mm, "construction": true});
            skSolve(sketch);
        }
        {
            var Q0;
            Q0=makeQuery(id+"F0.imprint","IMPRINT",FACE,{"disambiguationData":[TD([[makeQuery(id+"F0.imprint","IMPRINT",EDGE,{"derivedFrom":sQuery(id+"F0.wireOp",EDGE,"E0.bottom")}),-1.0]])]});
            extrude(context, id + "F1", {"entities" : qUnion([Q0]), "depth" : 3 * mm});
        }
        {
            var Q0;
            Q0=makeQuery(id+"F1.opExtrude","CAP_FACE",FACE,{"disambiguationData":[OSD([sQuery(id+"F0.wireOp",EDGE,"E0.bottom"),sQuery(id+"F0.wireOp",EDGE,"E0.top"),sQuery(id+"F0.wireOp",EDGE,"E0.left"),sQuery(id+"F0.wireOp",EDGE,"E0.right"),sQuery(id+"F0.wireOp",EDGE,"E3.0"),sQuery(id+"F0.wireOp",EDGE,"E3.1"),sQuery(id+"F0.wireOp",EDGE,"E3.2"),sQuery(id+"F0.wireOp",EDGE,"E4.0"),sQuery(id+"F0.wireOp",EDGE,"E4.1"),sQuery(id+"F0.wireOp",EDGE,"E4.2"),sQuery(id+"F0.wireOp",EDGE,"E5.0.1.1"),sQuery(id+"F0.wireOp",EDGE,"E5.0.1.2"),sQuery(id+"F0.wireOp",EDGE,"E5.0.1.3"),sQuery(id+"F0.wireOp",EDGE,"E5.0.1.5"),sQuery(id+"F0.wireOp",EDGE,"E5.0.1.6"),sQuery(id+"F0.wireOp",EDGE,"E5.0.1.7"),sQuery(id+"F0.wireOp",EDGE,"E5.0.2.1"),sQuery(id+"F0.wireOp",EDGE,"E5.0.2.2"),sQuery(id+"F0.wireOp",EDGE,"E5.0.2.3"),sQuery(id+"F0.wireOp",EDGE,"E5.0.2.5"),sQuery(id+"F0.wireOp",EDGE,"E5.0.2.6"),sQuery(id+"F0.wireOp",EDGE,"E5.0.2.7"),sQuery(id+"F0.wireOp",EDGE,"E5.0.3.1"),sQuery(id+"F0.wireOp",EDGE,"E5.0.3.2"),sQuery(id+"F0.wireOp",EDGE,"E5.0.3.3"),sQuery(id+"F0.wireOp",EDGE,"E5.0.3.5"),sQuery(id+"F0.wireOp",EDGE,"E5.0.3.6"),sQuery(id+"F0.wireOp",EDGE,"E5.0.3.7"),sQuery(id+"F0.wireOp",EDGE,"E5.0.4.1"),sQuery(id+"F0.wireOp",EDGE,"E5.0.4.2"),sQuery(id+"F0.wireOp",EDGE,"E5.0.4.3"),sQuery(id+"F0.wireOp",EDGE,"E5.0.4.5"),sQuery(id+"F0.wireOp",EDGE,"E5.0.4.6"),sQuery(id+"F0.wireOp",EDGE,"E5.0.4.7"),sQuery(id+"F0.wireOp",EDGE,"E5.1.0.1"),sQuery(id+"F0.wireOp",EDGE,"E5.1.0.2"),sQuery(id+"F0.wireOp",EDGE,"E5.1.0.3"),sQuery(id+"F0.wireOp",EDGE,"E5.1.0.5"),sQuery(id+"F0.wireOp",EDGE,"E5.1.0.6"),sQuery(id+"F0.wireOp",EDGE,"E5.1.0.7"),sQuery(id+"F0.wireOp",EDGE,"E5.1.1.1"),sQuery(id+"F0.wireOp",EDGE,"E5.1.1.2"),sQuery(id+"F0.wireOp",EDGE,"E5.1.1.3"),sQuery(id+"F0.wireOp",EDGE,"E5.1.1.5"),sQuery(id+"F0.wireOp",EDGE,"E5.1.1.6"),sQuery(id+"F0.wireOp",EDGE,"E5.1.1.7"),sQuery(id+"F0.wireOp",EDGE,"E5.1.2.1"),sQuery(id+"F0.wireOp",EDGE,"E5.1.2.2"),sQuery(id+"F0.wireOp",EDGE,"E5.1.2.3"),sQuery(id+"F0.wireOp",EDGE,"E5.1.2.5"),sQuery(id+"F0.wireOp",EDGE,"E5.1.2.6"),sQuery(id+"F0.wireOp",EDGE,"E5.1.2.7"),sQuery(id+"F0.wireOp",EDGE,"E5.1.3.1"),sQuery(id+"F0.wireOp",EDGE,"E5.1.3.2"),sQuery(id+"F0.wireOp",EDGE,"E5.1.3.3"),sQuery(id+"F0.wireOp",EDGE,"E5.1.3.5"),sQuery(id+"F0.wireOp",EDGE,"E5.1.3.6"),sQuery(id+"F0.wireOp",EDGE,"E5.1.3.7"),sQuery(id+"F0.wireOp",EDGE,"E5.1.4.1"),sQuery(id+"F0.wireOp",EDGE,"E5.1.4.2"),sQuery(id+"F0.wireOp",EDGE,"E5.1.4.3"),sQuery(id+"F0.wireOp",EDGE,"E5.1.4.5"),sQuery(id+"F0.wireOp",EDGE,"E5.1.4.6"),sQuery(id+"F0.wireOp",EDGE,"E5.1.4.7"),sQuery(id+"F0.wireOp",EDGE,"E5.2.0.1"),sQuery(id+"F0.wireOp",EDGE,"E5.2.0.2"),sQuery(id+"F0.wireOp",EDGE,"E5.2.0.3"),sQuery(id+"F0.wireOp",EDGE,"E5.2.0.5"),sQuery(id+"F0.wireOp",EDGE,"E5.2.0.6"),sQuery(id+"F0.wireOp",EDGE,"E5.2.0.7"),sQuery(id+"F0.wireOp",EDGE,"E5.2.1.1"),sQuery(id+"F0.wireOp",EDGE,"E5.2.1.2"),sQuery(id+"F0.wireOp",EDGE,"E5.2.1.3"),sQuery(id+"F0.wireOp",EDGE,"E5.2.1.5"),sQuery(id+"F0.wireOp",EDGE,"E5.2.1.6"),sQuery(id+"F0.wireOp",EDGE,"E5.2.1.7"),sQuery(id+"F0.wireOp",EDGE,"E5.2.2.1"),sQuery(id+"F0.wireOp",EDGE,"E5.2.2.2"),sQuery(id+"F0.wireOp",EDGE,"E5.2.2.3"),sQuery(id+"F0.wireOp",EDGE,"E5.2.2.5"),sQuery(id+"F0.wireOp",EDGE,"E5.2.2.6"),sQuery(id+"F0.wireOp",EDGE,"E5.2.2.7"),sQuery(id+"F0.wireOp",EDGE,"E5.2.3.1"),sQuery(id+"F0.wireOp",EDGE,"E5.2.3.2"),sQuery(id+"F0.wireOp",EDGE,"E5.2.3.3"),sQuery(id+"F0.wireOp",EDGE,"E5.2.3.5"),sQuery(id+"F0.wireOp",EDGE,"E5.2.3.6"),sQuery(id+"F0.wireOp",EDGE,"E5.2.3.7"),sQuery(id+"F0.wireOp",EDGE,"E5.2.4.1"),sQuery(id+"F0.wireOp",EDGE,"E5.2.4.2"),sQuery(id+"F0.wireOp",EDGE,"E5.2.4.3"),sQuery(id+"F0.wireOp",EDGE,"E5.2.4.5"),sQuery(id+"F0.wireOp",EDGE,"E5.2.4.6"),sQuery(id+"F0.wireOp",EDGE,"E5.2.4.7"),sQuery(id+"F0.wireOp",EDGE,"E5.3.0.1"),sQuery(id+"F0.wireOp",EDGE,"E5.3.0.2"),sQuery(id+"F0.wireOp",EDGE,"E5.3.0.3"),sQuery(id+"F0.wireOp",EDGE,"E5.3.0.5"),sQuery(id+"F0.wireOp",EDGE,"E5.3.0.6"),sQuery(id+"F0.wireOp",EDGE,"E5.3.0.7"),sQuery(id+"F0.wireOp",EDGE,"E5.3.1.1"),sQuery(id+"F0.wireOp",EDGE,"E5.3.1.2"),sQuery(id+"F0.wireOp",EDGE,"E5.3.1.3"),sQuery(id+"F0.wireOp",EDGE,"E5.3.1.5"),sQuery(id+"F0.wireOp",EDGE,"E5.3.1.6"),sQuery(id+"F0.wireOp",EDGE,"E5.3.1.7"),sQuery(id+"F0.wireOp",EDGE,"E5.3.2.1"),sQuery(id+"F0.wireOp",EDGE,"E5.3.2.2"),sQuery(id+"F0.wireOp",EDGE,"E5.3.2.3"),sQuery(id+"F0.wireOp",EDGE,"E5.3.2.5"),sQuery(id+"F0.wireOp",EDGE,"E5.3.2.6"),sQuery(id+"F0.wireOp",EDGE,"E5.3.2.7"),sQuery(id+"F0.wireOp",EDGE,"E5.3.3.1"),sQuery(id+"F0.wireOp",EDGE,"E5.3.3.2"),sQuery(id+"F0.wireOp",EDGE,"E5.3.3.3"),sQuery(id+"F0.wireOp",EDGE,"E5.3.3.5"),sQuery(id+"F0.wireOp",EDGE,"E5.3.3.6"),sQuery(id+"F0.wireOp",EDGE,"E5.3.3.7"),sQuery(id+"F0.wireOp",EDGE,"E5.3.4.1"),sQuery(id+"F0.wireOp",EDGE,"E5.3.4.2"),sQuery(id+"F0.wireOp",EDGE,"E5.3.4.3"),sQuery(id+"F0.wireOp",EDGE,"E5.3.4.5"),sQuery(id+"F0.wireOp",EDGE,"E5.3.4.6"),sQuery(id+"F0.wireOp",EDGE,"E5.3.4.7"),sQuery(id+"F0.wireOp",EDGE,"E5.4.0.1"),sQuery(id+"F0.wireOp",EDGE,"E5.4.0.2"),sQuery(id+"F0.wireOp",EDGE,"E5.4.0.3"),sQuery(id+"F0.wireOp",EDGE,"E5.4.0.5"),sQuery(id+"F0.wireOp",EDGE,"E5.4.0.6"),sQuery(id+"F0.wireOp",EDGE,"E5.4.0.7"),sQuery(id+"F0.wireOp",EDGE,"E5.4.1.1"),sQuery(id+"F0.wireOp",EDGE,"E5.4.1.2"),sQuery(id+"F0.wireOp",EDGE,"E5.4.1.3"),sQuery(id+"F0.wireOp",EDGE,"E5.4.1.5"),sQuery(id+"F0.wireOp",EDGE,"E5.4.1.6"),sQuery(id+"F0.wireOp",EDGE,"E5.4.1.7"),sQuery(id+"F0.wireOp",EDGE,"E5.4.2.1"),sQuery(id+"F0.wireOp",EDGE,"E5.4.2.2"),sQuery(id+"F0.wireOp",EDGE,"E5.4.2.3"),sQuery(id+"F0.wireOp",EDGE,"E5.4.2.5"),sQuery(id+"F0.wireOp",EDGE,"E5.4.2.6"),sQuery(id+"F0.wireOp",EDGE,"E5.4.2.7"),sQuery(id+"F0.wireOp",EDGE,"E5.4.3.1"),sQuery(id+"F0.wireOp",EDGE,"E5.4.3.2"),sQuery(id+"F0.wireOp",EDGE,"E5.4.3.3"),sQuery(id+"F0.wireOp",EDGE,"E5.4.3.5"),sQuery(id+"F0.wireOp",EDGE,"E5.4.3.6"),sQuery(id+"F0.wireOp",EDGE,"E5.4.3.7"),sQuery(id+"F0.wireOp",EDGE,"E5.4.4.1"),sQuery(id+"F0.wireOp",EDGE,"E5.4.4.2"),sQuery(id+"F0.wireOp",EDGE,"E5.4.4.3"),sQuery(id+"F0.wireOp",EDGE,"E5.4.4.5"),sQuery(id+"F0.wireOp",EDGE,"E5.4.4.6"),sQuery(id+"F0.wireOp",EDGE,"E5.4.4.7"),sQuery(id+"F0.wireOp",EDGE,"E5.5.0.1"),sQuery(id+"F0.wireOp",EDGE,"E5.5.0.2"),sQuery(id+"F0.wireOp",EDGE,"E5.5.0.3"),sQuery(id+"F0.wireOp",EDGE,"E5.5.0.5"),sQuery(id+"F0.wireOp",EDGE,"E5.5.0.6"),sQuery(id+"F0.wireOp",EDGE,"E5.5.0.7"),sQuery(id+"F0.wireOp",EDGE,"E5.5.1.1"),sQuery(id+"F0.wireOp",EDGE,"E5.5.1.2"),sQuery(id+"F0.wireOp",EDGE,"E5.5.1.3"),sQuery(id+"F0.wireOp",EDGE,"E5.5.1.5"),sQuery(id+"F0.wireOp",EDGE,"E5.5.1.6"),sQuery(id+"F0.wireOp",EDGE,"E5.5.1.7"),sQuery(id+"F0.wireOp",EDGE,"E5.5.2.1"),sQuery(id+"F0.wireOp",EDGE,"E5.5.2.2"),sQuery(id+"F0.wireOp",EDGE,"E5.5.2.3"),sQuery(id+"F0.wireOp",EDGE,"E5.5.2.5"),sQuery(id+"F0.wireOp",EDGE,"E5.5.2.6"),sQuery(id+"F0.wireOp",EDGE,"E5.5.2.7"),sQuery(id+"F0.wireOp",EDGE,"E5.5.3.1"),sQuery(id+"F0.wireOp",EDGE,"E5.5.3.2"),sQuery(id+"F0.wireOp",EDGE,"E5.5.3.3"),sQuery(id+"F0.wireOp",EDGE,"E5.5.3.5"),sQuery(id+"F0.wireOp",EDGE,"E5.5.3.6"),sQuery(id+"F0.wireOp",EDGE,"E5.5.3.7"),sQuery(id+"F0.wireOp",EDGE,"E5.5.4.1"),sQuery(id+"F0.wireOp",EDGE,"E5.5.4.2"),sQuery(id+"F0.wireOp",EDGE,"E5.5.4.3"),sQuery(id+"F0.wireOp",EDGE,"E5.5.4.5"),sQuery(id+"F0.wireOp",EDGE,"E5.5.4.6"),sQuery(id+"F0.wireOp",EDGE,"E5.5.4.7"),sQuery(id+"F0.wireOp",EDGE,"E5.6.0.1"),sQuery(id+"F0.wireOp",EDGE,"E5.6.0.2"),sQuery(id+"F0.wireOp",EDGE,"E5.6.0.3"),sQuery(id+"F0.wireOp",EDGE,"E5.6.0.5"),sQuery(id+"F0.wireOp",EDGE,"E5.6.0.6"),sQuery(id+"F0.wireOp",EDGE,"E5.6.0.7"),sQuery(id+"F0.wireOp",EDGE,"E5.6.1.1"),sQuery(id+"F0.wireOp",EDGE,"E5.6.1.2"),sQuery(id+"F0.wireOp",EDGE,"E5.6.1.3"),sQuery(id+"F0.wireOp",EDGE,"E5.6.1.5"),sQuery(id+"F0.wireOp",EDGE,"E5.6.1.6"),sQuery(id+"F0.wireOp",EDGE,"E5.6.1.7"),sQuery(id+"F0.wireOp",EDGE,"E5.6.2.1"),sQuery(id+"F0.wireOp",EDGE,"E5.6.2.2"),sQuery(id+"F0.wireOp",EDGE,"E5.6.2.3"),sQuery(id+"F0.wireOp",EDGE,"E5.6.2.5"),sQuery(id+"F0.wireOp",EDGE,"E5.6.2.6"),sQuery(id+"F0.wireOp",EDGE,"E5.6.2.7"),sQuery(id+"F0.wireOp",EDGE,"E5.6.3.1"),sQuery(id+"F0.wireOp",EDGE,"E5.6.3.2"),sQuery(id+"F0.wireOp",EDGE,"E5.6.3.3"),sQuery(id+"F0.wireOp",EDGE,"E5.6.3.5"),sQuery(id+"F0.wireOp",EDGE,"E5.6.3.6"),sQuery(id+"F0.wireOp",EDGE,"E5.6.3.7"),sQuery(id+"F0.wireOp",EDGE,"E5.6.4.1"),sQuery(id+"F0.wireOp",EDGE,"E5.6.4.2"),sQuery(id+"F0.wireOp",EDGE,"E5.6.4.3"),sQuery(id+"F0.wireOp",EDGE,"E5.6.4.5"),sQuery(id+"F0.wireOp",EDGE,"E5.6.4.6"),sQuery(id+"F0.wireOp",EDGE,"E5.6.4.7"),sQuery(id+"F0.wireOp",EDGE,"E5.7.0.1"),sQuery(id+"F0.wireOp",EDGE,"E5.7.0.2"),sQuery(id+"F0.wireOp",EDGE,"E5.7.0.3"),sQuery(id+"F0.wireOp",EDGE,"E5.7.0.5"),sQuery(id+"F0.wireOp",EDGE,"E5.7.0.6"),sQuery(id+"F0.wireOp",EDGE,"E5.7.0.7"),sQuery(id+"F0.wireOp",EDGE,"E5.7.1.1"),sQuery(id+"F0.wireOp",EDGE,"E5.7.1.2"),sQuery(id+"F0.wireOp",EDGE,"E5.7.1.3"),sQuery(id+"F0.wireOp",EDGE,"E5.7.1.5"),sQuery(id+"F0.wireOp",EDGE,"E5.7.1.6"),sQuery(id+"F0.wireOp",EDGE,"E5.7.1.7"),sQuery(id+"F0.wireOp",EDGE,"E5.7.2.1"),sQuery(id+"F0.wireOp",EDGE,"E5.7.2.2"),sQuery(id+"F0.wireOp",EDGE,"E5.7.2.3"),sQuery(id+"F0.wireOp",EDGE,"E5.7.2.5"),sQuery(id+"F0.wireOp",EDGE,"E5.7.2.6"),sQuery(id+"F0.wireOp",EDGE,"E5.7.2.7"),sQuery(id+"F0.wireOp",EDGE,"E5.7.3.1"),sQuery(id+"F0.wireOp",EDGE,"E5.7.3.2"),sQuery(id+"F0.wireOp",EDGE,"E5.7.3.3"),sQuery(id+"F0.wireOp",EDGE,"E5.7.3.5"),sQuery(id+"F0.wireOp",EDGE,"E5.7.3.6"),sQuery(id+"F0.wireOp",EDGE,"E5.7.3.7"),sQuery(id+"F0.wireOp",EDGE,"E5.7.4.1"),sQuery(id+"F0.wireOp",EDGE,"E5.7.4.2"),sQuery(id+"F0.wireOp",EDGE,"E5.7.4.3"),sQuery(id+"F0.wireOp",EDGE,"E5.7.4.5"),sQuery(id+"F0.wireOp",EDGE,"E5.7.4.6"),sQuery(id+"F0.wireOp",EDGE,"E5.7.4.7"),sQuery(id+"F0.wireOp",EDGE,"E5.8.0.1"),sQuery(id+"F0.wireOp",EDGE,"E5.8.0.2"),sQuery(id+"F0.wireOp",EDGE,"E5.8.0.3"),sQuery(id+"F0.wireOp",EDGE,"E5.8.0.5"),sQuery(id+"F0.wireOp",EDGE,"E5.8.0.6"),sQuery(id+"F0.wireOp",EDGE,"E5.8.0.7"),sQuery(id+"F0.wireOp",EDGE,"E5.8.1.1"),sQuery(id+"F0.wireOp",EDGE,"E5.8.1.2"),sQuery(id+"F0.wireOp",EDGE,"E5.8.1.3"),sQuery(id+"F0.wireOp",EDGE,"E5.8.1.5"),sQuery(id+"F0.wireOp",EDGE,"E5.8.1.6"),sQuery(id+"F0.wireOp",EDGE,"E5.8.1.7"),sQuery(id+"F0.wireOp",EDGE,"E5.8.2.1"),sQuery(id+"F0.wireOp",EDGE,"E5.8.2.2"),sQuery(id+"F0.wireOp",EDGE,"E5.8.2.3"),sQuery(id+"F0.wireOp",EDGE,"E5.8.2.5"),sQuery(id+"F0.wireOp",EDGE,"E5.8.2.6"),sQuery(id+"F0.wireOp",EDGE,"E5.8.2.7"),sQuery(id+"F0.wireOp",EDGE,"E5.8.3.1"),sQuery(id+"F0.wireOp",EDGE,"E5.8.3.2"),sQuery(id+"F0.wireOp",EDGE,"E5.8.3.3"),sQuery(id+"F0.wireOp",EDGE,"E5.8.3.5"),sQuery(id+"F0.wireOp",EDGE,"E5.8.3.6"),sQuery(id+"F0.wireOp",EDGE,"E5.8.3.7"),sQuery(id+"F0.wireOp",EDGE,"E5.8.4.1"),sQuery(id+"F0.wireOp",EDGE,"E5.8.4.2"),sQuery(id+"F0.wireOp",EDGE,"E5.8.4.3"),sQuery(id+"F0.wireOp",EDGE,"E5.8.4.5"),sQuery(id+"F0.wireOp",EDGE,"E5.8.4.6"),sQuery(id+"F0.wireOp",EDGE,"E5.8.4.7"),sQuery(id+"F0.wireOp",EDGE,"E5.9.0.1"),sQuery(id+"F0.wireOp",EDGE,"E5.9.0.2"),sQuery(id+"F0.wireOp",EDGE,"E5.9.0.3"),sQuery(id+"F0.wireOp",EDGE,"E5.9.0.5"),sQuery(id+"F0.wireOp",EDGE,"E5.9.0.6"),sQuery(id+"F0.wireOp",EDGE,"E5.9.0.7"),sQuery(id+"F0.wireOp",EDGE,"E5.9.1.1"),sQuery(id+"F0.wireOp",EDGE,"E5.9.1.2"),sQuery(id+"F0.wireOp",EDGE,"E5.9.1.3"),sQuery(id+"F0.wireOp",EDGE,"E5.9.1.5"),sQuery(id+"F0.wireOp",EDGE,"E5.9.1.6"),sQuery(id+"F0.wireOp",EDGE,"E5.9.1.7"),sQuery(id+"F0.wireOp",EDGE,"E5.9.2.1"),sQuery(id+"F0.wireOp",EDGE,"E5.9.2.2"),sQuery(id+"F0.wireOp",EDGE,"E5.9.2.3"),sQuery(id+"F0.wireOp",EDGE,"E5.9.2.5"),sQuery(id+"F0.wireOp",EDGE,"E5.9.2.6"),sQuery(id+"F0.wireOp",EDGE,"E5.9.2.7"),sQuery(id+"F0.wireOp",EDGE,"E5.9.3.1"),sQuery(id+"F0.wireOp",EDGE,"E5.9.3.2"),sQuery(id+"F0.wireOp",EDGE,"E5.9.3.3"),sQuery(id+"F0.wireOp",EDGE,"E5.9.3.5"),sQuery(id+"F0.wireOp",EDGE,"E5.9.3.6"),sQuery(id+"F0.wireOp",EDGE,"E5.9.3.7"),sQuery(id+"F0.wireOp",EDGE,"E5.9.4.1"),sQuery(id+"F0.wireOp",EDGE,"E5.9.4.2"),sQuery(id+"F0.wireOp",EDGE,"E5.9.4.3"),sQuery(id+"F0.wireOp",EDGE,"E5.9.4.5"),sQuery(id+"F0.wireOp",EDGE,"E5.9.4.6"),sQuery(id+"F0.wireOp",EDGE,"E5.9.4.7"),sQuery(id+"F0.wireOp",EDGE,"E5.10.0.1"),sQuery(id+"F0.wireOp",EDGE,"E5.10.0.2"),sQuery(id+"F0.wireOp",EDGE,"E5.10.0.3"),sQuery(id+"F0.wireOp",EDGE,"E5.10.0.5"),sQuery(id+"F0.wireOp",EDGE,"E5.10.0.6"),sQuery(id+"F0.wireOp",EDGE,"E5.10.0.7"),sQuery(id+"F0.wireOp",EDGE,"E5.10.1.1"),sQuery(id+"F0.wireOp",EDGE,"E5.10.1.2"),sQuery(id+"F0.wireOp",EDGE,"E5.10.1.3"),sQuery(id+"F0.wireOp",EDGE,"E5.10.1.5"),sQuery(id+"F0.wireOp",EDGE,"E5.10.1.6"),sQuery(id+"F0.wireOp",EDGE,"E5.10.1.7"),sQuery(id+"F0.wireOp",EDGE,"E5.10.2.1"),sQuery(id+"F0.wireOp",EDGE,"E5.10.2.2"),sQuery(id+"F0.wireOp",EDGE,"E5.10.2.3"),sQuery(id+"F0.wireOp",EDGE,"E5.10.2.5"),sQuery(id+"F0.wireOp",EDGE,"E5.10.2.6"),sQuery(id+"F0.wireOp",EDGE,"E5.10.2.7"),sQuery(id+"F0.wireOp",EDGE,"E5.10.3.1"),sQuery(id+"F0.wireOp",EDGE,"E5.10.3.2"),sQuery(id+"F0.wireOp",EDGE,"E5.10.3.3"),sQuery(id+"F0.wireOp",EDGE,"E5.10.3.5"),sQuery(id+"F0.wireOp",EDGE,"E5.10.3.6"),sQuery(id+"F0.wireOp",EDGE,"E5.10.3.7"),sQuery(id+"F0.wireOp",EDGE,"E5.10.4.1"),sQuery(id+"F0.wireOp",EDGE,"E5.10.4.2"),sQuery(id+"F0.wireOp",EDGE,"E5.10.4.3"),sQuery(id+"F0.wireOp",EDGE,"E5.10.4.5"),sQuery(id+"F0.wireOp",EDGE,"E5.10.4.6"),sQuery(id+"F0.wireOp",EDGE,"E5.10.4.7"),sQuery(id+"F0.wireOp",EDGE,"E5.11.0.1"),sQuery(id+"F0.wireOp",EDGE,"E5.11.0.2"),sQuery(id+"F0.wireOp",EDGE,"E5.11.0.3"),sQuery(id+"F0.wireOp",EDGE,"E5.11.0.5"),sQuery(id+"F0.wireOp",EDGE,"E5.11.0.6"),sQuery(id+"F0.wireOp",EDGE,"E5.11.0.7"),sQuery(id+"F0.wireOp",EDGE,"E5.11.1.1"),sQuery(id+"F0.wireOp",EDGE,"E5.11.1.2"),sQuery(id+"F0.wireOp",EDGE,"E5.11.1.3"),sQuery(id+"F0.wireOp",EDGE,"E5.11.1.5"),sQuery(id+"F0.wireOp",EDGE,"E5.11.1.6"),sQuery(id+"F0.wireOp",EDGE,"E5.11.1.7"),sQuery(id+"F0.wireOp",EDGE,"E5.11.2.1"),sQuery(id+"F0.wireOp",EDGE,"E5.11.2.2"),sQuery(id+"F0.wireOp",EDGE,"E5.11.2.3"),sQuery(id+"F0.wireOp",EDGE,"E5.11.2.5"),sQuery(id+"F0.wireOp",EDGE,"E5.11.2.6"),sQuery(id+"F0.wireOp",EDGE,"E5.11.2.7"),sQuery(id+"F0.wireOp",EDGE,"E5.11.3.1"),sQuery(id+"F0.wireOp",EDGE,"E5.11.3.2"),sQuery(id+"F0.wireOp",EDGE,"E5.11.3.3"),sQuery(id+"F0.wireOp",EDGE,"E5.11.3.5"),sQuery(id+"F0.wireOp",EDGE,"E5.11.3.6"),sQuery(id+"F0.wireOp",EDGE,"E5.11.3.7"),sQuery(id+"F0.wireOp",EDGE,"E5.11.4.1"),sQuery(id+"F0.wireOp",EDGE,"E5.11.4.2"),sQuery(id+"F0.wireOp",EDGE,"E5.11.4.3"),sQuery(id+"F0.wireOp",EDGE,"E5.11.4.5"),sQuery(id+"F0.wireOp",EDGE,"E5.11.4.6"),sQuery(id+"F0.wireOp",EDGE,"E5.11.4.7"),sQuery(id+"F0.wireOp",EDGE,"E5.12.0.1"),sQuery(id+"F0.wireOp",EDGE,"E5.12.0.2"),sQuery(id+"F0.wireOp",EDGE,"E5.12.0.3"),sQuery(id+"F0.wireOp",EDGE,"E5.12.0.5"),sQuery(id+"F0.wireOp",EDGE,"E5.12.0.6"),sQuery(id+"F0.wireOp",EDGE,"E5.12.0.7"),sQuery(id+"F0.wireOp",EDGE,"E5.12.1.1"),sQuery(id+"F0.wireOp",EDGE,"E5.12.1.2"),sQuery(id+"F0.wireOp",EDGE,"E5.12.1.3"),sQuery(id+"F0.wireOp",EDGE,"E5.12.1.5"),sQuery(id+"F0.wireOp",EDGE,"E5.12.1.6"),sQuery(id+"F0.wireOp",EDGE,"E5.12.1.7"),sQuery(id+"F0.wireOp",EDGE,"E5.12.2.1"),sQuery(id+"F0.wireOp",EDGE,"E5.12.2.2"),sQuery(id+"F0.wireOp",EDGE,"E5.12.2.3"),sQuery(id+"F0.wireOp",EDGE,"E5.12.2.5"),sQuery(id+"F0.wireOp",EDGE,"E5.12.2.6"),sQuery(id+"F0.wireOp",EDGE,"E5.12.2.7"),sQuery(id+"F0.wireOp",EDGE,"E5.12.3.1"),sQuery(id+"F0.wireOp",EDGE,"E5.12.3.2"),sQuery(id+"F0.wireOp",EDGE,"E5.12.3.3"),sQuery(id+"F0.wireOp",EDGE,"E5.12.3.5"),sQuery(id+"F0.wireOp",EDGE,"E5.12.3.6"),sQuery(id+"F0.wireOp",EDGE,"E5.12.3.7"),sQuery(id+"F0.wireOp",EDGE,"E5.12.4.1"),sQuery(id+"F0.wireOp",EDGE,"E5.12.4.2"),sQuery(id+"F0.wireOp",EDGE,"E5.12.4.3"),sQuery(id+"F0.wireOp",EDGE,"E5.12.4.5"),sQuery(id+"F0.wireOp",EDGE,"E5.12.4.6"),sQuery(id+"F0.wireOp",EDGE,"E5.12.4.7"),sQuery(id+"F0.wireOp",EDGE,"E5.13.0.1"),sQuery(id+"F0.wireOp",EDGE,"E5.13.0.2"),sQuery(id+"F0.wireOp",EDGE,"E5.13.0.3"),sQuery(id+"F0.wireOp",EDGE,"E5.13.0.5"),sQuery(id+"F0.wireOp",EDGE,"E5.13.0.6"),sQuery(id+"F0.wireOp",EDGE,"E5.13.0.7"),sQuery(id+"F0.wireOp",EDGE,"E5.13.1.1"),sQuery(id+"F0.wireOp",EDGE,"E5.13.1.2"),sQuery(id+"F0.wireOp",EDGE,"E5.13.1.3"),sQuery(id+"F0.wireOp",EDGE,"E5.13.1.5"),sQuery(id+"F0.wireOp",EDGE,"E5.13.1.6"),sQuery(id+"F0.wireOp",EDGE,"E5.13.1.7"),sQuery(id+"F0.wireOp",EDGE,"E5.13.2.1"),sQuery(id+"F0.wireOp",EDGE,"E5.13.2.2"),sQuery(id+"F0.wireOp",EDGE,"E5.13.2.3"),sQuery(id+"F0.wireOp",EDGE,"E5.13.2.5"),sQuery(id+"F0.wireOp",EDGE,"E5.13.2.6"),sQuery(id+"F0.wireOp",EDGE,"E5.13.2.7"),sQuery(id+"F0.wireOp",EDGE,"E5.13.3.1"),sQuery(id+"F0.wireOp",EDGE,"E5.13.3.2"),sQuery(id+"F0.wireOp",EDGE,"E5.13.3.3"),sQuery(id+"F0.wireOp",EDGE,"E5.13.3.5"),sQuery(id+"F0.wireOp",EDGE,"E5.13.3.6"),sQuery(id+"F0.wireOp",EDGE,"E5.13.3.7"),sQuery(id+"F0.wireOp",EDGE,"E5.13.4.1"),sQuery(id+"F0.wireOp",EDGE,"E5.13.4.2"),sQuery(id+"F0.wireOp",EDGE,"E5.13.4.3"),sQuery(id+"F0.wireOp",EDGE,"E5.13.4.5"),sQuery(id+"F0.wireOp",EDGE,"E5.13.4.6"),sQuery(id+"F0.wireOp",EDGE,"E5.13.4.7")])],"isStart":false});
            var sketch = newSketch(context, id + "F2", { "sketchPlane" : qUnion([Q0])});
            skLineSegment(sketch, "E6.bottom", {"start": v(-70, 40) * mm, "end": v(70, 40) * mm});
            skLineSegment(sketch, "E6.top", {"start": v(-70, -40) * mm, "end": v(70, -40) * mm});
            skLineSegment(sketch, "E6.left", {"start": v(-70, 40) * mm, "end": v(-70, -40) * mm});
            skLineSegment(sketch, "E6.right", {"start": v(70, 40) * mm, "end": v(70, -40) * mm});
            skLineSegment(sketch, "E7.bottom", {"start": v(-67, 37) * mm, "end": v(67, 37) * mm});
            skLineSegment(sketch, "E7.top", {"start": v(-67, -37) * mm, "end": v(67, -37) * mm});
            skLineSegment(sketch, "E7.left", {"start": v(-67, 37) * mm, "end": v(-67, -37) * mm});
            skLineSegment(sketch, "E7.right", {"start": v(67, 37) * mm, "end": v(67, -37) * mm});
            skSolve(sketch);
        }
        {
            var Q0;
            Q0=makeQuery(id+"F2.imprint","IMPRINT",FACE,{"disambiguationData":[TD([[makeQuery(id+"F2.imprint","IMPRINT",EDGE,{"derivedFrom":sQuery(id+"F2.wireOp",EDGE,"E6.bottom")}),-1.0]])]});
            extrude(context, id + "F3", {"entities" : qUnion([Q0]), "operationType" : NewBodyOperationType.ADD, "depth" : 180 * mm});
        }
        {
            var Q0;
            Q0=makeQuery(id+"F3.boolean.opBoolean","MERGE",EDGE,{"derivedFrom":[makeQuery(id+"F1.opExtrude","SWEPT_EDGE",EDGE,{"disambiguationData":[OSD([sQuery(id+"F0.wireOp",EDGE,"E0.top"),sQuery(id+"F0.wireOp",EDGE,"E0.left")])]}),makeQuery(id+"F3.opExtrude","SWEPT_EDGE",EDGE,{"disambiguationData":[OSD([sQuery(id+"F2.wireOp",EDGE,"E6.top"),sQuery(id+"F2.wireOp",EDGE,"E6.left")])]})]});
            var Q1;
            Q1=makeQuery(id+"F3.boolean.opBoolean","MERGE",EDGE,{"derivedFrom":[makeQuery(id+"F1.opExtrude","SWEPT_EDGE",EDGE,{"disambiguationData":[OSD([sQuery(id+"F0.wireOp",EDGE,"E0.bottom"),sQuery(id+"F0.wireOp",EDGE,"E0.left")])]}),makeQuery(id+"F3.opExtrude","SWEPT_EDGE",EDGE,{"disambiguationData":[OSD([sQuery(id+"F2.wireOp",EDGE,"E6.bottom"),sQuery(id+"F2.wireOp",EDGE,"E6.left")])]})]});
            var Q2;
            Q2=makeQuery(id+"F3.boolean.opBoolean","MERGE",EDGE,{"derivedFrom":[makeQuery(id+"F1.opExtrude","SWEPT_EDGE",EDGE,{"disambiguationData":[OSD([sQuery(id+"F0.wireOp",EDGE,"E0.bottom"),sQuery(id+"F0.wireOp",EDGE,"E0.right")])]}),makeQuery(id+"F3.opExtrude","SWEPT_EDGE",EDGE,{"disambiguationData":[OSD([sQuery(id+"F2.wireOp",EDGE,"E6.bottom"),sQuery(id+"F2.wireOp",EDGE,"E6.right")])]})]});
            var Q3;
            Q3=makeQuery(id+"F3.boolean.opBoolean","MERGE",EDGE,{"derivedFrom":[makeQuery(id+"F1.opExtrude","SWEPT_EDGE",EDGE,{"disambiguationData":[OSD([sQuery(id+"F0.wireOp",EDGE,"E0.top"),sQuery(id+"F0.wireOp",EDGE,"E0.right")])]}),makeQuery(id+"F3.opExtrude","SWEPT_EDGE",EDGE,{"disambiguationData":[OSD([sQuery(id+"F2.wireOp",EDGE,"E6.top"),sQuery(id+"F2.wireOp",EDGE,"E6.right")])]})]});
            var Q4;
            Q4=makeQuery(id+"F3.opExtrude","SWEPT_EDGE",EDGE,{"disambiguationData":[OSD([sQuery(id+"F2.wireOp",EDGE,"E7.top"),sQuery(id+"F2.wireOp",EDGE,"E7.left")])]});
            var Q5;
            Q5=makeQuery(id+"F3.opExtrude","SWEPT_EDGE",EDGE,{"disambiguationData":[OSD([sQuery(id+"F2.wireOp",EDGE,"E7.bottom"),sQuery(id+"F2.wireOp",EDGE,"E7.left")])]});
            var Q6;
            Q6=makeQuery(id+"F3.opExtrude","SWEPT_EDGE",EDGE,{"disambiguationData":[OSD([sQuery(id+"F2.wireOp",EDGE,"E7.bottom"),sQuery(id+"F2.wireOp",EDGE,"E7.right")])]});
            var Q7;
            Q7=makeQuery(id+"F3.opExtrude","SWEPT_EDGE",EDGE,{"disambiguationData":[OSD([sQuery(id+"F2.wireOp",EDGE,"E7.top"),sQuery(id+"F2.wireOp",EDGE,"E7.right")])]});
            fillet(context, id + "F4", {"entities" : qUnion([Q0, Q1, Q2, Q3, Q4, Q5, Q6, Q7]), "radius" : 5 * mm, "tangentPropagation" : true, "allowEdgeOverflow" : false});
        }
        {
            var Q0;
            Q0=makeQuery(id+"F3.boolean.opBoolean","MERGE",FACE,{"derivedFrom":[makeQuery(id+"F1.opExtrude","SWEPT_FACE",FACE,{"disambiguationData":[OSD([sQuery(id+"F0.wireOp",EDGE,"E0.left")])]}),makeQuery(id+"F3.opExtrude","SWEPT_FACE",FACE,{"disambiguationData":[OSD([sQuery(id+"F2.wireOp",EDGE,"E6.left")])]})]});
            var sketch = newSketch(context, id + "F5", { "sketchPlane" : qUnion([Q0])});
            skCircle(sketch, "E8.cCircle", {"center": v(-22, 14.62) * mm, "radius": 4.62 * mm, "construction": true});
            skLineSegment(sketch, "E8.0", {"start": v(-14, 10) * mm, "end": v(-30, 10) * mm});
            skLineSegment(sketch, "E8.1", {"start": v(-30, 10) * mm, "end": v(-22, 23.86) * mm});
            skLineSegment(sketch, "E8.2", {"start": v(-22, 23.86) * mm, "end": v(-14, 10) * mm});
            skPoint(sketch, "E8.0.midPoint", {"position": v(-22, 10) * mm});
            skCircle(sketch, "E9.cCircle", {"center": v(-11, 19.24) * mm, "radius": 4.62 * mm, "construction": true});
            skLineSegment(sketch, "E9.0", {"start": v(-19, 23.86) * mm, "end": v(-3, 23.86) * mm});
            skLineSegment(sketch, "E9.1", {"start": v(-3, 23.86) * mm, "end": v(-11, 10) * mm});
            skLineSegment(sketch, "E9.2", {"start": v(-11, 10) * mm, "end": v(-19, 23.86) * mm});
            skPoint(sketch, "E9.0.midPoint", {"position": v(-11, 23.86) * mm});
            skCircle(sketch, "E10.cCircle", {"center": v(0, 14.62) * mm, "radius": 4.62 * mm, "construction": true});
            skLineSegment(sketch, "E10.0", {"start": v(8, 10) * mm, "end": v(-8, 10) * mm});
            skLineSegment(sketch, "E10.1", {"start": v(-8, 10) * mm, "end": v(0, 23.86) * mm});
            skLineSegment(sketch, "E10.2", {"start": v(0, 23.86) * mm, "end": v(8, 10) * mm});
            skPoint(sketch, "E10.0.midPoint", {"position": v(0, 10) * mm});
            skCircle(sketch, "E11.cCircle", {"center": v(11, 19.24) * mm, "radius": 4.62 * mm, "construction": true});
            skLineSegment(sketch, "E11.0", {"start": v(3, 23.86) * mm, "end": v(19, 23.86) * mm});
            skLineSegment(sketch, "E11.1", {"start": v(19, 23.86) * mm, "end": v(11, 10) * mm});
            skLineSegment(sketch, "E11.2", {"start": v(11, 10) * mm, "end": v(3, 23.86) * mm});
            skPoint(sketch, "E11.0.midPoint", {"position": v(11, 23.86) * mm});
            skCircle(sketch, "E12.cCircle", {"center": v(22, 14.62) * mm, "radius": 4.62 * mm, "construction": true});
            skLineSegment(sketch, "E12.0", {"start": v(30, 10) * mm, "end": v(14, 10) * mm});
            skLineSegment(sketch, "E12.1", {"start": v(14, 10) * mm, "end": v(22, 23.86) * mm});
            skLineSegment(sketch, "E12.2", {"start": v(22, 23.86) * mm, "end": v(30, 10) * mm});
            skPoint(sketch, "E12.0.midPoint", {"position": v(22, 10) * mm});
            skLineSegment(sketch, "E13.0.1.0", {"start": v(-30, 26.86) * mm, "end": v(-22, 40.71) * mm});
            skLineSegment(sketch, "E13.0.1.1", {"start": v(19, 40.71) * mm, "end": v(11, 26.86) * mm});
            skCircle(sketch, "E13.0.1.2", {"center": v(-22, 31.47) * mm, "radius": 4.62 * mm, "construction": true});
            skCircle(sketch, "E13.0.1.3", {"center": v(11, 36.1) * mm, "radius": 4.62 * mm, "construction": true});
            skCircle(sketch, "E13.0.1.4", {"center": v(22, 31.47) * mm, "radius": 4.62 * mm, "construction": true});
            skLineSegment(sketch, "E13.0.1.5", {"start": v(-14, 26.86) * mm, "end": v(-30, 26.86) * mm});
            skPoint(sketch, "E13.0.1.6", {"position": v(11, 40.71) * mm});
            skPoint(sketch, "E13.0.1.7", {"position": v(0, 26.86) * mm});
            skPoint(sketch, "E13.0.1.8", {"position": v(-11, 40.71) * mm});
            skLineSegment(sketch, "E13.0.1.9", {"start": v(30, 26.86) * mm, "end": v(14, 26.86) * mm});
            skLineSegment(sketch, "E13.0.1.10", {"start": v(3, 40.71) * mm, "end": v(19, 40.71) * mm});
            skCircle(sketch, "E13.0.1.11", {"center": v(-11, 36.1) * mm, "radius": 4.62 * mm, "construction": true});
            skCircle(sketch, "E13.0.1.12", {"center": v(0, 31.47) * mm, "radius": 4.62 * mm, "construction": true});
            skLineSegment(sketch, "E13.0.1.13", {"start": v(-22, 40.71) * mm, "end": v(-14, 26.86) * mm});
            skLineSegment(sketch, "E13.0.1.14", {"start": v(-3, 40.71) * mm, "end": v(-11, 26.86) * mm});
            skPoint(sketch, "E13.0.1.15", {"position": v(-22, 26.86) * mm});
            skLineSegment(sketch, "E13.0.1.16", {"start": v(14, 26.86) * mm, "end": v(22, 40.71) * mm});
            skLineSegment(sketch, "E13.0.1.17", {"start": v(8, 26.86) * mm, "end": v(-8, 26.86) * mm});
            skLineSegment(sketch, "E13.0.1.18", {"start": v(-19, 40.71) * mm, "end": v(-3, 40.71) * mm});
            skLineSegment(sketch, "E13.0.1.19", {"start": v(11, 26.86) * mm, "end": v(3, 40.71) * mm});
            skLineSegment(sketch, "E13.0.1.20", {"start": v(22, 40.71) * mm, "end": v(30, 26.86) * mm});
            skLineSegment(sketch, "E13.0.1.21", {"start": v(0, 40.71) * mm, "end": v(8, 26.86) * mm});
            skLineSegment(sketch, "E13.0.1.22", {"start": v(-8, 26.86) * mm, "end": v(0, 40.71) * mm});
            skPoint(sketch, "E13.0.1.23", {"position": v(22, 26.86) * mm});
            skLineSegment(sketch, "E13.0.1.24", {"start": v(-11, 26.86) * mm, "end": v(-19, 40.71) * mm});
            skLineSegment(sketch, "E13.0.2.0", {"start": v(-30, 43.71) * mm, "end": v(-22, 57.57) * mm});
            skLineSegment(sketch, "E13.0.2.1", {"start": v(19, 57.57) * mm, "end": v(11, 43.71) * mm});
            skCircle(sketch, "E13.0.2.2", {"center": v(-22, 48.33) * mm, "radius": 4.62 * mm, "construction": true});
            skCircle(sketch, "E13.0.2.3", {"center": v(11, 52.95) * mm, "radius": 4.62 * mm, "construction": true});
            skCircle(sketch, "E13.0.2.4", {"center": v(22, 48.33) * mm, "radius": 4.62 * mm, "construction": true});
            skLineSegment(sketch, "E13.0.2.5", {"start": v(-14, 43.71) * mm, "end": v(-30, 43.71) * mm});
            skPoint(sketch, "E13.0.2.6", {"position": v(11, 57.57) * mm});
            skPoint(sketch, "E13.0.2.7", {"position": v(0, 43.71) * mm});
            skPoint(sketch, "E13.0.2.8", {"position": v(-11, 57.57) * mm});
            skLineSegment(sketch, "E13.0.2.9", {"start": v(30, 43.71) * mm, "end": v(14, 43.71) * mm});
            skLineSegment(sketch, "E13.0.2.10", {"start": v(3, 57.57) * mm, "end": v(19, 57.57) * mm});
            skCircle(sketch, "E13.0.2.11", {"center": v(-11, 52.95) * mm, "radius": 4.62 * mm, "construction": true});
            skCircle(sketch, "E13.0.2.12", {"center": v(0, 48.33) * mm, "radius": 4.62 * mm, "construction": true});
            skLineSegment(sketch, "E13.0.2.13", {"start": v(-22, 57.57) * mm, "end": v(-14, 43.71) * mm});
            skLineSegment(sketch, "E13.0.2.14", {"start": v(-3, 57.57) * mm, "end": v(-11, 43.71) * mm});
            skPoint(sketch, "E13.0.2.15", {"position": v(-22, 43.71) * mm});
            skLineSegment(sketch, "E13.0.2.16", {"start": v(14, 43.71) * mm, "end": v(22, 57.57) * mm});
            skLineSegment(sketch, "E13.0.2.17", {"start": v(8, 43.71) * mm, "end": v(-8, 43.71) * mm});
            skLineSegment(sketch, "E13.0.2.18", {"start": v(-19, 57.57) * mm, "end": v(-3, 57.57) * mm});
            skLineSegment(sketch, "E13.0.2.19", {"start": v(11, 43.71) * mm, "end": v(3, 57.57) * mm});
            skLineSegment(sketch, "E13.0.2.20", {"start": v(22, 57.57) * mm, "end": v(30, 43.71) * mm});
            skLineSegment(sketch, "E13.0.2.21", {"start": v(0, 57.57) * mm, "end": v(8, 43.71) * mm});
            skLineSegment(sketch, "E13.0.2.22", {"start": v(-8, 43.71) * mm, "end": v(0, 57.57) * mm});
            skPoint(sketch, "E13.0.2.23", {"position": v(22, 43.71) * mm});
            skLineSegment(sketch, "E13.0.2.24", {"start": v(-11, 43.71) * mm, "end": v(-19, 57.57) * mm});
            skLineSegment(sketch, "E13.0.3.0", {"start": v(-30, 60.57) * mm, "end": v(-22, 74.42) * mm});
            skLineSegment(sketch, "E13.0.3.1", {"start": v(19, 74.42) * mm, "end": v(11, 60.57) * mm});
            skCircle(sketch, "E13.0.3.2", {"center": v(-22, 65.19) * mm, "radius": 4.62 * mm, "construction": true});
            skCircle(sketch, "E13.0.3.3", {"center": v(11, 69.8) * mm, "radius": 4.62 * mm, "construction": true});
            skCircle(sketch, "E13.0.3.4", {"center": v(22, 65.19) * mm, "radius": 4.62 * mm, "construction": true});
            skLineSegment(sketch, "E13.0.3.5", {"start": v(-14, 60.57) * mm, "end": v(-30, 60.57) * mm});
            skPoint(sketch, "E13.0.3.6", {"position": v(11, 74.42) * mm});
            skPoint(sketch, "E13.0.3.7", {"position": v(0, 60.57) * mm});
            skPoint(sketch, "E13.0.3.8", {"position": v(-11, 74.42) * mm});
            skLineSegment(sketch, "E13.0.3.9", {"start": v(30, 60.57) * mm, "end": v(14, 60.57) * mm});
            skLineSegment(sketch, "E13.0.3.10", {"start": v(3, 74.42) * mm, "end": v(19, 74.42) * mm});
            skCircle(sketch, "E13.0.3.11", {"center": v(-11, 69.8) * mm, "radius": 4.62 * mm, "construction": true});
            skCircle(sketch, "E13.0.3.12", {"center": v(0, 65.19) * mm, "radius": 4.62 * mm, "construction": true});
            skLineSegment(sketch, "E13.0.3.13", {"start": v(-22, 74.42) * mm, "end": v(-14, 60.57) * mm});
            skLineSegment(sketch, "E13.0.3.14", {"start": v(-3, 74.42) * mm, "end": v(-11, 60.57) * mm});
            skPoint(sketch, "E13.0.3.15", {"position": v(-22, 60.57) * mm});
            skLineSegment(sketch, "E13.0.3.16", {"start": v(14, 60.57) * mm, "end": v(22, 74.42) * mm});
            skLineSegment(sketch, "E13.0.3.17", {"start": v(8, 60.57) * mm, "end": v(-8, 60.57) * mm});
            skLineSegment(sketch, "E13.0.3.18", {"start": v(-19, 74.42) * mm, "end": v(-3, 74.42) * mm});
            skLineSegment(sketch, "E13.0.3.19", {"start": v(11, 60.57) * mm, "end": v(3, 74.42) * mm});
            skLineSegment(sketch, "E13.0.3.20", {"start": v(22, 74.42) * mm, "end": v(30, 60.57) * mm});
            skLineSegment(sketch, "E13.0.3.21", {"start": v(0, 74.42) * mm, "end": v(8, 60.57) * mm});
            skLineSegment(sketch, "E13.0.3.22", {"start": v(-8, 60.57) * mm, "end": v(0, 74.42) * mm});
            skPoint(sketch, "E13.0.3.23", {"position": v(22, 60.57) * mm});
            skLineSegment(sketch, "E13.0.3.24", {"start": v(-11, 60.57) * mm, "end": v(-19, 74.42) * mm});
            skLineSegment(sketch, "E13.0.4.0", {"start": v(-30, 77.42) * mm, "end": v(-22, 91.28) * mm});
            skLineSegment(sketch, "E13.0.4.1", {"start": v(19, 91.28) * mm, "end": v(11, 77.42) * mm});
            skCircle(sketch, "E13.0.4.2", {"center": v(-22, 82.04) * mm, "radius": 4.62 * mm, "construction": true});
            skCircle(sketch, "E13.0.4.3", {"center": v(11, 86.66) * mm, "radius": 4.62 * mm, "construction": true});
            skCircle(sketch, "E13.0.4.4", {"center": v(22, 82.04) * mm, "radius": 4.62 * mm, "construction": true});
            skLineSegment(sketch, "E13.0.4.5", {"start": v(-14, 77.42) * mm, "end": v(-30, 77.42) * mm});
            skPoint(sketch, "E13.0.4.6", {"position": v(11, 91.28) * mm});
            skPoint(sketch, "E13.0.4.7", {"position": v(0, 77.42) * mm});
            skPoint(sketch, "E13.0.4.8", {"position": v(-11, 91.28) * mm});
            skLineSegment(sketch, "E13.0.4.9", {"start": v(30, 77.42) * mm, "end": v(14, 77.42) * mm});
            skLineSegment(sketch, "E13.0.4.10", {"start": v(3, 91.28) * mm, "end": v(19, 91.28) * mm});
            skCircle(sketch, "E13.0.4.11", {"center": v(-11, 86.66) * mm, "radius": 4.62 * mm, "construction": true});
            skCircle(sketch, "E13.0.4.12", {"center": v(0, 82.04) * mm, "radius": 4.62 * mm, "construction": true});
            skLineSegment(sketch, "E13.0.4.13", {"start": v(-22, 91.28) * mm, "end": v(-14, 77.42) * mm});
            skLineSegment(sketch, "E13.0.4.14", {"start": v(-3, 91.28) * mm, "end": v(-11, 77.42) * mm});
            skPoint(sketch, "E13.0.4.15", {"position": v(-22, 77.42) * mm});
            skLineSegment(sketch, "E13.0.4.16", {"start": v(14, 77.42) * mm, "end": v(22, 91.28) * mm});
            skLineSegment(sketch, "E13.0.4.17", {"start": v(8, 77.42) * mm, "end": v(-8, 77.42) * mm});
            skLineSegment(sketch, "E13.0.4.18", {"start": v(-19, 91.28) * mm, "end": v(-3, 91.28) * mm});
            skLineSegment(sketch, "E13.0.4.19", {"start": v(11, 77.42) * mm, "end": v(3, 91.28) * mm});
            skLineSegment(sketch, "E13.0.4.20", {"start": v(22, 91.28) * mm, "end": v(30, 77.42) * mm});
            skLineSegment(sketch, "E13.0.4.21", {"start": v(0, 91.28) * mm, "end": v(8, 77.42) * mm});
            skLineSegment(sketch, "E13.0.4.22", {"start": v(-8, 77.42) * mm, "end": v(0, 91.28) * mm});
            skPoint(sketch, "E13.0.4.23", {"position": v(22, 77.42) * mm});
            skLineSegment(sketch, "E13.0.4.24", {"start": v(-11, 77.42) * mm, "end": v(-19, 91.28) * mm});
            skLineSegment(sketch, "E13.0.5.0", {"start": v(-30, 94.28) * mm, "end": v(-22, 108.14) * mm});
            skLineSegment(sketch, "E13.0.5.1", {"start": v(19, 108.14) * mm, "end": v(11, 94.28) * mm});
            skCircle(sketch, "E13.0.5.2", {"center": v(-22, 98.9) * mm, "radius": 4.62 * mm, "construction": true});
            skCircle(sketch, "E13.0.5.3", {"center": v(11, 103.52) * mm, "radius": 4.62 * mm, "construction": true});
            skCircle(sketch, "E13.0.5.4", {"center": v(22, 98.9) * mm, "radius": 4.62 * mm, "construction": true});
            skLineSegment(sketch, "E13.0.5.5", {"start": v(-14, 94.28) * mm, "end": v(-30, 94.28) * mm});
            skPoint(sketch, "E13.0.5.6", {"position": v(11, 108.14) * mm});
            skPoint(sketch, "E13.0.5.7", {"position": v(0, 94.28) * mm});
            skPoint(sketch, "E13.0.5.8", {"position": v(-11, 108.14) * mm});
            skLineSegment(sketch, "E13.0.5.9", {"start": v(30, 94.28) * mm, "end": v(14, 94.28) * mm});
            skLineSegment(sketch, "E13.0.5.10", {"start": v(3, 108.14) * mm, "end": v(19, 108.14) * mm});
            skCircle(sketch, "E13.0.5.11", {"center": v(-11, 103.52) * mm, "radius": 4.62 * mm, "construction": true});
            skCircle(sketch, "E13.0.5.12", {"center": v(0, 98.9) * mm, "radius": 4.62 * mm, "construction": true});
            skLineSegment(sketch, "E13.0.5.13", {"start": v(-22, 108.14) * mm, "end": v(-14, 94.28) * mm});
            skLineSegment(sketch, "E13.0.5.14", {"start": v(-3, 108.14) * mm, "end": v(-11, 94.28) * mm});
            skPoint(sketch, "E13.0.5.15", {"position": v(-22, 94.28) * mm});
            skLineSegment(sketch, "E13.0.5.16", {"start": v(14, 94.28) * mm, "end": v(22, 108.14) * mm});
            skLineSegment(sketch, "E13.0.5.17", {"start": v(8, 94.28) * mm, "end": v(-8, 94.28) * mm});
            skLineSegment(sketch, "E13.0.5.18", {"start": v(-19, 108.14) * mm, "end": v(-3, 108.14) * mm});
            skLineSegment(sketch, "E13.0.5.19", {"start": v(11, 94.28) * mm, "end": v(3, 108.14) * mm});
            skLineSegment(sketch, "E13.0.5.20", {"start": v(22, 108.14) * mm, "end": v(30, 94.28) * mm});
            skLineSegment(sketch, "E13.0.5.21", {"start": v(0, 108.14) * mm, "end": v(8, 94.28) * mm});
            skLineSegment(sketch, "E13.0.5.22", {"start": v(-8, 94.28) * mm, "end": v(0, 108.14) * mm});
            skPoint(sketch, "E13.0.5.23", {"position": v(22, 94.28) * mm});
            skLineSegment(sketch, "E13.0.5.24", {"start": v(-11, 94.28) * mm, "end": v(-19, 108.14) * mm});
            skLineSegment(sketch, "E13.0.6.0", {"start": v(-30, 111.14) * mm, "end": v(-22, 125) * mm});
            skLineSegment(sketch, "E13.0.6.1", {"start": v(19, 125) * mm, "end": v(11, 111.14) * mm});
            skCircle(sketch, "E13.0.6.2", {"center": v(-22, 115.75) * mm, "radius": 4.62 * mm, "construction": true});
            skCircle(sketch, "E13.0.6.3", {"center": v(11, 120.37) * mm, "radius": 4.62 * mm, "construction": true});
            skCircle(sketch, "E13.0.6.4", {"center": v(22, 115.75) * mm, "radius": 4.62 * mm, "construction": true});
            skLineSegment(sketch, "E13.0.6.5", {"start": v(-14, 111.14) * mm, "end": v(-30, 111.14) * mm});
            skPoint(sketch, "E13.0.6.6", {"position": v(11, 125) * mm});
            skPoint(sketch, "E13.0.6.7", {"position": v(0, 111.14) * mm});
            skPoint(sketch, "E13.0.6.8", {"position": v(-11, 125) * mm});
            skLineSegment(sketch, "E13.0.6.9", {"start": v(30, 111.14) * mm, "end": v(14, 111.14) * mm});
            skLineSegment(sketch, "E13.0.6.10", {"start": v(3, 125) * mm, "end": v(19, 125) * mm});
            skCircle(sketch, "E13.0.6.11", {"center": v(-11, 120.37) * mm, "radius": 4.62 * mm, "construction": true});
            skCircle(sketch, "E13.0.6.12", {"center": v(0, 115.75) * mm, "radius": 4.62 * mm, "construction": true});
            skLineSegment(sketch, "E13.0.6.13", {"start": v(-22, 125) * mm, "end": v(-14, 111.14) * mm});
            skLineSegment(sketch, "E13.0.6.14", {"start": v(-3, 125) * mm, "end": v(-11, 111.14) * mm});
            skPoint(sketch, "E13.0.6.15", {"position": v(-22, 111.14) * mm});
            skLineSegment(sketch, "E13.0.6.16", {"start": v(14, 111.14) * mm, "end": v(22, 125) * mm});
            skLineSegment(sketch, "E13.0.6.17", {"start": v(8, 111.14) * mm, "end": v(-8, 111.14) * mm});
            skLineSegment(sketch, "E13.0.6.18", {"start": v(-19, 125) * mm, "end": v(-3, 125) * mm});
            skLineSegment(sketch, "E13.0.6.19", {"start": v(11, 111.14) * mm, "end": v(3, 125) * mm});
            skLineSegment(sketch, "E13.0.6.20", {"start": v(22, 125) * mm, "end": v(30, 111.14) * mm});
            skLineSegment(sketch, "E13.0.6.21", {"start": v(0, 125) * mm, "end": v(8, 111.14) * mm});
            skLineSegment(sketch, "E13.0.6.22", {"start": v(-8, 111.14) * mm, "end": v(0, 125) * mm});
            skPoint(sketch, "E13.0.6.23", {"position": v(22, 111.14) * mm});
            skLineSegment(sketch, "E13.0.6.24", {"start": v(-11, 111.14) * mm, "end": v(-19, 125) * mm});
            skLineSegment(sketch, "E13.0.7.0", {"start": v(-30, 128) * mm, "end": v(-22, 141.85) * mm});
            skLineSegment(sketch, "E13.0.7.1", {"start": v(19, 141.85) * mm, "end": v(11, 128) * mm});
            skCircle(sketch, "E13.0.7.2", {"center": v(-22, 132.61) * mm, "radius": 4.62 * mm, "construction": true});
            skCircle(sketch, "E13.0.7.3", {"center": v(11, 137.23) * mm, "radius": 4.62 * mm, "construction": true});
            skCircle(sketch, "E13.0.7.4", {"center": v(22, 132.61) * mm, "radius": 4.62 * mm, "construction": true});
            skLineSegment(sketch, "E13.0.7.5", {"start": v(-14, 128) * mm, "end": v(-30, 128) * mm});
            skPoint(sketch, "E13.0.7.6", {"position": v(11, 141.85) * mm});
            skPoint(sketch, "E13.0.7.7", {"position": v(0, 128) * mm});
            skPoint(sketch, "E13.0.7.8", {"position": v(-11, 141.85) * mm});
            skLineSegment(sketch, "E13.0.7.9", {"start": v(30, 128) * mm, "end": v(14, 128) * mm});
            skLineSegment(sketch, "E13.0.7.10", {"start": v(3, 141.85) * mm, "end": v(19, 141.85) * mm});
            skCircle(sketch, "E13.0.7.11", {"center": v(-11, 137.23) * mm, "radius": 4.62 * mm, "construction": true});
            skCircle(sketch, "E13.0.7.12", {"center": v(0, 132.61) * mm, "radius": 4.62 * mm, "construction": true});
            skLineSegment(sketch, "E13.0.7.13", {"start": v(-22, 141.85) * mm, "end": v(-14, 128) * mm});
            skLineSegment(sketch, "E13.0.7.14", {"start": v(-3, 141.85) * mm, "end": v(-11, 128) * mm});
            skPoint(sketch, "E13.0.7.15", {"position": v(-22, 128) * mm});
            skLineSegment(sketch, "E13.0.7.16", {"start": v(14, 128) * mm, "end": v(22, 141.85) * mm});
            skLineSegment(sketch, "E13.0.7.17", {"start": v(8, 128) * mm, "end": v(-8, 128) * mm});
            skLineSegment(sketch, "E13.0.7.18", {"start": v(-19, 141.85) * mm, "end": v(-3, 141.85) * mm});
            skLineSegment(sketch, "E13.0.7.19", {"start": v(11, 128) * mm, "end": v(3, 141.85) * mm});
            skLineSegment(sketch, "E13.0.7.20", {"start": v(22, 141.85) * mm, "end": v(30, 128) * mm});
            skLineSegment(sketch, "E13.0.7.21", {"start": v(0, 141.85) * mm, "end": v(8, 128) * mm});
            skLineSegment(sketch, "E13.0.7.22", {"start": v(-8, 128) * mm, "end": v(0, 141.85) * mm});
            skPoint(sketch, "E13.0.7.23", {"position": v(22, 128) * mm});
            skLineSegment(sketch, "E13.0.7.24", {"start": v(-11, 128) * mm, "end": v(-19, 141.85) * mm});
            skLineSegment(sketch, "E13.0.8.0", {"start": v(-30, 144.85) * mm, "end": v(-22, 158.7) * mm});
            skLineSegment(sketch, "E13.0.8.1", {"start": v(19, 158.7) * mm, "end": v(11, 144.85) * mm});
            skCircle(sketch, "E13.0.8.2", {"center": v(-22, 149.47) * mm, "radius": 4.62 * mm, "construction": true});
            skCircle(sketch, "E13.0.8.3", {"center": v(11, 154.09) * mm, "radius": 4.62 * mm, "construction": true});
            skCircle(sketch, "E13.0.8.4", {"center": v(22, 149.47) * mm, "radius": 4.62 * mm, "construction": true});
            skLineSegment(sketch, "E13.0.8.5", {"start": v(-14, 144.85) * mm, "end": v(-30, 144.85) * mm});
            skPoint(sketch, "E13.0.8.6", {"position": v(11, 158.7) * mm});
            skPoint(sketch, "E13.0.8.7", {"position": v(0, 144.85) * mm});
            skPoint(sketch, "E13.0.8.8", {"position": v(-11, 158.7) * mm});
            skLineSegment(sketch, "E13.0.8.9", {"start": v(30, 144.85) * mm, "end": v(14, 144.85) * mm});
            skLineSegment(sketch, "E13.0.8.10", {"start": v(3, 158.7) * mm, "end": v(19, 158.7) * mm});
            skCircle(sketch, "E13.0.8.11", {"center": v(-11, 154.09) * mm, "radius": 4.62 * mm, "construction": true});
            skCircle(sketch, "E13.0.8.12", {"center": v(0, 149.47) * mm, "radius": 4.62 * mm, "construction": true});
            skLineSegment(sketch, "E13.0.8.13", {"start": v(-22, 158.7) * mm, "end": v(-14, 144.85) * mm});
            skLineSegment(sketch, "E13.0.8.14", {"start": v(-3, 158.7) * mm, "end": v(-11, 144.85) * mm});
            skPoint(sketch, "E13.0.8.15", {"position": v(-22, 144.85) * mm});
            skLineSegment(sketch, "E13.0.8.16", {"start": v(14, 144.85) * mm, "end": v(22, 158.7) * mm});
            skLineSegment(sketch, "E13.0.8.17", {"start": v(8, 144.85) * mm, "end": v(-8, 144.85) * mm});
            skLineSegment(sketch, "E13.0.8.18", {"start": v(-19, 158.7) * mm, "end": v(-3, 158.7) * mm});
            skLineSegment(sketch, "E13.0.8.19", {"start": v(11, 144.85) * mm, "end": v(3, 158.7) * mm});
            skLineSegment(sketch, "E13.0.8.20", {"start": v(22, 158.7) * mm, "end": v(30, 144.85) * mm});
            skLineSegment(sketch, "E13.0.8.21", {"start": v(0, 158.7) * mm, "end": v(8, 144.85) * mm});
            skLineSegment(sketch, "E13.0.8.22", {"start": v(-8, 144.85) * mm, "end": v(0, 158.7) * mm});
            skPoint(sketch, "E13.0.8.23", {"position": v(22, 144.85) * mm});
            skLineSegment(sketch, "E13.0.8.24", {"start": v(-11, 144.85) * mm, "end": v(-19, 158.7) * mm});
            skLineSegment(sketch, "E13.0.9.0", {"start": v(-30, 161.7) * mm, "end": v(-22, 175.56) * mm});
            skLineSegment(sketch, "E13.0.9.1", {"start": v(19, 175.56) * mm, "end": v(11, 161.7) * mm});
            skCircle(sketch, "E13.0.9.2", {"center": v(-22, 166.32) * mm, "radius": 4.62 * mm, "construction": true});
            skCircle(sketch, "E13.0.9.3", {"center": v(11, 170.94) * mm, "radius": 4.62 * mm, "construction": true});
            skCircle(sketch, "E13.0.9.4", {"center": v(22, 166.32) * mm, "radius": 4.62 * mm, "construction": true});
            skLineSegment(sketch, "E13.0.9.5", {"start": v(-14, 161.7) * mm, "end": v(-30, 161.7) * mm});
            skPoint(sketch, "E13.0.9.6", {"position": v(11, 175.56) * mm});
            skPoint(sketch, "E13.0.9.7", {"position": v(0, 161.7) * mm});
            skPoint(sketch, "E13.0.9.8", {"position": v(-11, 175.56) * mm});
            skLineSegment(sketch, "E13.0.9.9", {"start": v(30, 161.7) * mm, "end": v(14, 161.7) * mm});
            skLineSegment(sketch, "E13.0.9.10", {"start": v(3, 175.56) * mm, "end": v(19, 175.56) * mm});
            skCircle(sketch, "E13.0.9.11", {"center": v(-11, 170.94) * mm, "radius": 4.62 * mm, "construction": true});
            skCircle(sketch, "E13.0.9.12", {"center": v(0, 166.32) * mm, "radius": 4.62 * mm, "construction": true});
            skLineSegment(sketch, "E13.0.9.13", {"start": v(-22, 175.56) * mm, "end": v(-14, 161.7) * mm});
            skLineSegment(sketch, "E13.0.9.14", {"start": v(-3, 175.56) * mm, "end": v(-11, 161.7) * mm});
            skPoint(sketch, "E13.0.9.15", {"position": v(-22, 161.7) * mm});
            skLineSegment(sketch, "E13.0.9.16", {"start": v(14, 161.7) * mm, "end": v(22, 175.56) * mm});
            skLineSegment(sketch, "E13.0.9.17", {"start": v(8, 161.7) * mm, "end": v(-8, 161.7) * mm});
            skLineSegment(sketch, "E13.0.9.18", {"start": v(-19, 175.56) * mm, "end": v(-3, 175.56) * mm});
            skLineSegment(sketch, "E13.0.9.19", {"start": v(11, 161.7) * mm, "end": v(3, 175.56) * mm});
            skLineSegment(sketch, "E13.0.9.20", {"start": v(22, 175.56) * mm, "end": v(30, 161.7) * mm});
            skLineSegment(sketch, "E13.0.9.21", {"start": v(0, 175.56) * mm, "end": v(8, 161.7) * mm});
            skLineSegment(sketch, "E13.0.9.22", {"start": v(-8, 161.7) * mm, "end": v(0, 175.56) * mm});
            skPoint(sketch, "E13.0.9.23", {"position": v(22, 161.7) * mm});
            skLineSegment(sketch, "E13.0.9.24", {"start": v(-11, 161.7) * mm, "end": v(-19, 175.56) * mm});
            skLineSegment(sketch, "E13.direction1", {"start": v(-30, 10) * mm, "end": v(-5, 10) * mm, "construction": true});
            skLineSegment(sketch, "E13.direction2", {"start": v(-30, 10) * mm, "end": v(-30, 26.86) * mm, "construction": true});
            skSolve(sketch);
        }
        {
            var Q0;
            Q0=makeQuery(id+"F5.imprint","IMPRINT",FACE,{"disambiguationData":[TD([[makeQuery(id+"F5.imprint","IMPRINT",EDGE,{"derivedFrom":sQuery(id+"F5.wireOp",EDGE,"E13.0.9.0")}),-1.0]])]});
            var Q1;
            Q1=makeQuery(id+"F5.imprint","IMPRINT",FACE,{"disambiguationData":[TD([[makeQuery(id+"F5.imprint","IMPRINT",EDGE,{"derivedFrom":sQuery(id+"F5.wireOp",EDGE,"E13.0.9.14")}),-1.0]])]});
            var Q2;
            Q2=makeQuery(id+"F5.imprint","IMPRINT",FACE,{"disambiguationData":[TD([[makeQuery(id+"F5.imprint","IMPRINT",EDGE,{"derivedFrom":sQuery(id+"F5.wireOp",EDGE,"E13.0.9.17")}),-1.0]])]});
            var Q3;
            Q3=makeQuery(id+"F5.imprint","IMPRINT",FACE,{"disambiguationData":[TD([[makeQuery(id+"F5.imprint","IMPRINT",EDGE,{"derivedFrom":sQuery(id+"F5.wireOp",EDGE,"E13.0.9.1")}),-1.0]])]});
            var Q4;
            Q4=makeQuery(id+"F5.imprint","IMPRINT",FACE,{"disambiguationData":[TD([[makeQuery(id+"F5.imprint","IMPRINT",EDGE,{"derivedFrom":sQuery(id+"F5.wireOp",EDGE,"E13.0.9.9")}),-1.0]])]});
            var Q5;
            Q5=makeQuery(id+"F5.imprint","IMPRINT",FACE,{"disambiguationData":[TD([[makeQuery(id+"F5.imprint","IMPRINT",EDGE,{"derivedFrom":sQuery(id+"F5.wireOp",EDGE,"E13.0.8.9")}),-1.0]])]});
            var Q6;
            Q6=makeQuery(id+"F5.imprint","IMPRINT",FACE,{"disambiguationData":[TD([[makeQuery(id+"F5.imprint","IMPRINT",EDGE,{"derivedFrom":sQuery(id+"F5.wireOp",EDGE,"E13.0.8.1")}),-1.0]])]});
            var Q7;
            Q7=makeQuery(id+"F5.imprint","IMPRINT",FACE,{"disambiguationData":[TD([[makeQuery(id+"F5.imprint","IMPRINT",EDGE,{"derivedFrom":sQuery(id+"F5.wireOp",EDGE,"E13.0.8.17")}),-1.0]])]});
            var Q8;
            Q8=makeQuery(id+"F5.imprint","IMPRINT",FACE,{"disambiguationData":[TD([[makeQuery(id+"F5.imprint","IMPRINT",EDGE,{"derivedFrom":sQuery(id+"F5.wireOp",EDGE,"E13.0.8.14")}),-1.0]])]});
            var Q9;
            Q9=makeQuery(id+"F5.imprint","IMPRINT",FACE,{"disambiguationData":[TD([[makeQuery(id+"F5.imprint","IMPRINT",EDGE,{"derivedFrom":sQuery(id+"F5.wireOp",EDGE,"E13.0.8.0")}),-1.0]])]});
            var Q10;
            Q10=makeQuery(id+"F5.imprint","IMPRINT",FACE,{"disambiguationData":[TD([[makeQuery(id+"F5.imprint","IMPRINT",EDGE,{"derivedFrom":sQuery(id+"F5.wireOp",EDGE,"E13.0.7.14")}),-1.0]])]});
            var Q11;
            Q11=makeQuery(id+"F5.imprint","IMPRINT",FACE,{"disambiguationData":[TD([[makeQuery(id+"F5.imprint","IMPRINT",EDGE,{"derivedFrom":sQuery(id+"F5.wireOp",EDGE,"E13.0.7.1")}),-1.0]])]});
            var Q12;
            Q12=makeQuery(id+"F5.imprint","IMPRINT",FACE,{"disambiguationData":[TD([[makeQuery(id+"F5.imprint","IMPRINT",EDGE,{"derivedFrom":sQuery(id+"F5.wireOp",EDGE,"E13.0.7.9")}),-1.0]])]});
            var Q13;
            Q13=makeQuery(id+"F5.imprint","IMPRINT",FACE,{"disambiguationData":[TD([[makeQuery(id+"F5.imprint","IMPRINT",EDGE,{"derivedFrom":sQuery(id+"F5.wireOp",EDGE,"E13.0.7.0")}),-1.0]])]});
            var Q14;
            Q14=makeQuery(id+"F5.imprint","IMPRINT",FACE,{"disambiguationData":[TD([[makeQuery(id+"F5.imprint","IMPRINT",EDGE,{"derivedFrom":sQuery(id+"F5.wireOp",EDGE,"E13.0.6.0")}),-1.0]])]});
            var Q15;
            Q15=makeQuery(id+"F5.imprint","IMPRINT",FACE,{"disambiguationData":[TD([[makeQuery(id+"F5.imprint","IMPRINT",EDGE,{"derivedFrom":sQuery(id+"F5.wireOp",EDGE,"E13.0.6.14")}),-1.0]])]});
            var Q16;
            Q16=makeQuery(id+"F5.imprint","IMPRINT",FACE,{"disambiguationData":[TD([[makeQuery(id+"F5.imprint","IMPRINT",EDGE,{"derivedFrom":sQuery(id+"F5.wireOp",EDGE,"E13.0.7.17")}),-1.0]])]});
            var Q17;
            Q17=makeQuery(id+"F5.imprint","IMPRINT",FACE,{"disambiguationData":[TD([[makeQuery(id+"F5.imprint","IMPRINT",EDGE,{"derivedFrom":sQuery(id+"F5.wireOp",EDGE,"E13.0.6.17")}),-1.0]])]});
            var Q18;
            Q18=makeQuery(id+"F5.imprint","IMPRINT",FACE,{"disambiguationData":[TD([[makeQuery(id+"F5.imprint","IMPRINT",EDGE,{"derivedFrom":sQuery(id+"F5.wireOp",EDGE,"E13.0.6.1")}),-1.0]])]});
            var Q19;
            Q19=makeQuery(id+"F5.imprint","IMPRINT",FACE,{"disambiguationData":[TD([[makeQuery(id+"F5.imprint","IMPRINT",EDGE,{"derivedFrom":sQuery(id+"F5.wireOp",EDGE,"E13.0.6.9")}),-1.0]])]});
            var Q20;
            Q20=makeQuery(id+"F5.imprint","IMPRINT",FACE,{"disambiguationData":[TD([[makeQuery(id+"F5.imprint","IMPRINT",EDGE,{"derivedFrom":sQuery(id+"F5.wireOp",EDGE,"E13.0.5.9")}),-1.0]])]});
            var Q21;
            Q21=makeQuery(id+"F5.imprint","IMPRINT",FACE,{"disambiguationData":[TD([[makeQuery(id+"F5.imprint","IMPRINT",EDGE,{"derivedFrom":sQuery(id+"F5.wireOp",EDGE,"E13.0.5.1")}),-1.0]])]});
            var Q22;
            Q22=makeQuery(id+"F5.imprint","IMPRINT",FACE,{"disambiguationData":[TD([[makeQuery(id+"F5.imprint","IMPRINT",EDGE,{"derivedFrom":sQuery(id+"F5.wireOp",EDGE,"E13.0.5.17")}),-1.0]])]});
            var Q23;
            Q23=makeQuery(id+"F5.imprint","IMPRINT",FACE,{"disambiguationData":[TD([[makeQuery(id+"F5.imprint","IMPRINT",EDGE,{"derivedFrom":sQuery(id+"F5.wireOp",EDGE,"E13.0.5.14")}),-1.0]])]});
            var Q24;
            Q24=makeQuery(id+"F5.imprint","IMPRINT",FACE,{"disambiguationData":[TD([[makeQuery(id+"F5.imprint","IMPRINT",EDGE,{"derivedFrom":sQuery(id+"F5.wireOp",EDGE,"E13.0.5.0")}),-1.0]])]});
            var Q25;
            Q25=makeQuery(id+"F5.imprint","IMPRINT",FACE,{"disambiguationData":[TD([[makeQuery(id+"F5.imprint","IMPRINT",EDGE,{"derivedFrom":sQuery(id+"F5.wireOp",EDGE,"E13.0.4.0")}),-1.0]])]});
            var Q26;
            Q26=makeQuery(id+"F5.imprint","IMPRINT",FACE,{"disambiguationData":[TD([[makeQuery(id+"F5.imprint","IMPRINT",EDGE,{"derivedFrom":sQuery(id+"F5.wireOp",EDGE,"E13.0.4.14")}),-1.0]])]});
            var Q27;
            Q27=makeQuery(id+"F5.imprint","IMPRINT",FACE,{"disambiguationData":[TD([[makeQuery(id+"F5.imprint","IMPRINT",EDGE,{"derivedFrom":sQuery(id+"F5.wireOp",EDGE,"E13.0.4.17")}),-1.0]])]});
            var Q28;
            Q28=makeQuery(id+"F5.imprint","IMPRINT",FACE,{"disambiguationData":[TD([[makeQuery(id+"F5.imprint","IMPRINT",EDGE,{"derivedFrom":sQuery(id+"F5.wireOp",EDGE,"E13.0.4.1")}),-1.0]])]});
            var Q29;
            Q29=makeQuery(id+"F5.imprint","IMPRINT",FACE,{"disambiguationData":[TD([[makeQuery(id+"F5.imprint","IMPRINT",EDGE,{"derivedFrom":sQuery(id+"F5.wireOp",EDGE,"E13.0.4.9")}),-1.0]])]});
            var Q30;
            Q30=makeQuery(id+"F5.imprint","IMPRINT",FACE,{"disambiguationData":[TD([[makeQuery(id+"F5.imprint","IMPRINT",EDGE,{"derivedFrom":sQuery(id+"F5.wireOp",EDGE,"E13.0.3.9")}),-1.0]])]});
            var Q31;
            Q31=makeQuery(id+"F5.imprint","IMPRINT",FACE,{"disambiguationData":[TD([[makeQuery(id+"F5.imprint","IMPRINT",EDGE,{"derivedFrom":sQuery(id+"F5.wireOp",EDGE,"E13.0.3.1")}),-1.0]])]});
            var Q32;
            Q32=makeQuery(id+"F5.imprint","IMPRINT",FACE,{"disambiguationData":[TD([[makeQuery(id+"F5.imprint","IMPRINT",EDGE,{"derivedFrom":sQuery(id+"F5.wireOp",EDGE,"E13.0.3.17")}),-1.0]])]});
            var Q33;
            Q33=makeQuery(id+"F5.imprint","IMPRINT",FACE,{"disambiguationData":[TD([[makeQuery(id+"F5.imprint","IMPRINT",EDGE,{"derivedFrom":sQuery(id+"F5.wireOp",EDGE,"E13.0.3.14")}),-1.0]])]});
            var Q34;
            Q34=makeQuery(id+"F5.imprint","IMPRINT",FACE,{"disambiguationData":[TD([[makeQuery(id+"F5.imprint","IMPRINT",EDGE,{"derivedFrom":sQuery(id+"F5.wireOp",EDGE,"E13.0.3.0")}),-1.0]])]});
            var Q35;
            Q35=makeQuery(id+"F5.imprint","IMPRINT",FACE,{"disambiguationData":[TD([[makeQuery(id+"F5.imprint","IMPRINT",EDGE,{"derivedFrom":sQuery(id+"F5.wireOp",EDGE,"E13.0.2.0")}),-1.0]])]});
            var Q36;
            Q36=makeQuery(id+"F5.imprint","IMPRINT",FACE,{"disambiguationData":[TD([[makeQuery(id+"F5.imprint","IMPRINT",EDGE,{"derivedFrom":sQuery(id+"F5.wireOp",EDGE,"E13.0.2.14")}),-1.0]])]});
            var Q37;
            Q37=makeQuery(id+"F5.imprint","IMPRINT",FACE,{"disambiguationData":[TD([[makeQuery(id+"F5.imprint","IMPRINT",EDGE,{"derivedFrom":sQuery(id+"F5.wireOp",EDGE,"E13.0.2.17")}),-1.0]])]});
            var Q38;
            Q38=makeQuery(id+"F5.imprint","IMPRINT",FACE,{"disambiguationData":[TD([[makeQuery(id+"F5.imprint","IMPRINT",EDGE,{"derivedFrom":sQuery(id+"F5.wireOp",EDGE,"E13.0.2.1")}),-1.0]])]});
            var Q39;
            Q39=makeQuery(id+"F5.imprint","IMPRINT",FACE,{"disambiguationData":[TD([[makeQuery(id+"F5.imprint","IMPRINT",EDGE,{"derivedFrom":sQuery(id+"F5.wireOp",EDGE,"E13.0.2.9")}),-1.0]])]});
            var Q40;
            Q40=makeQuery(id+"F5.imprint","IMPRINT",FACE,{"disambiguationData":[TD([[makeQuery(id+"F5.imprint","IMPRINT",EDGE,{"derivedFrom":sQuery(id+"F5.wireOp",EDGE,"E13.0.1.9")}),-1.0]])]});
            var Q41;
            Q41=makeQuery(id+"F5.imprint","IMPRINT",FACE,{"disambiguationData":[TD([[makeQuery(id+"F5.imprint","IMPRINT",EDGE,{"derivedFrom":sQuery(id+"F5.wireOp",EDGE,"E13.0.1.17")}),-1.0]])]});
            var Q42;
            Q42=makeQuery(id+"F5.imprint","IMPRINT",FACE,{"disambiguationData":[TD([[makeQuery(id+"F5.imprint","IMPRINT",EDGE,{"derivedFrom":sQuery(id+"F5.wireOp",EDGE,"E13.0.1.1")}),-1.0]])]});
            var Q43;
            Q43=makeQuery(id+"F5.imprint","IMPRINT",FACE,{"disambiguationData":[TD([[makeQuery(id+"F5.imprint","IMPRINT",EDGE,{"derivedFrom":sQuery(id+"F5.wireOp",EDGE,"E13.0.1.0")}),-1.0]])]});
            var Q44;
            Q44=makeQuery(id+"F5.imprint","IMPRINT",FACE,{"disambiguationData":[TD([[makeQuery(id+"F5.imprint","IMPRINT",EDGE,{"derivedFrom":sQuery(id+"F5.wireOp",EDGE,"E13.0.1.14")}),-1.0]])]});
            var Q45;
            Q45=makeQuery(id+"F5.imprint","IMPRINT",FACE,{"disambiguationData":[TD([[makeQuery(id+"F5.imprint","IMPRINT",EDGE,{"derivedFrom":sQuery(id+"F5.wireOp",EDGE,"E8.0")}),-1.0]])]});
            var Q46;
            Q46=makeQuery(id+"F5.imprint","IMPRINT",FACE,{"disambiguationData":[TD([[makeQuery(id+"F5.imprint","IMPRINT",EDGE,{"derivedFrom":sQuery(id+"F5.wireOp",EDGE,"E9.0")}),-1.0]])]});
            var Q47;
            Q47=makeQuery(id+"F5.imprint","IMPRINT",FACE,{"disambiguationData":[TD([[makeQuery(id+"F5.imprint","IMPRINT",EDGE,{"derivedFrom":sQuery(id+"F5.wireOp",EDGE,"E10.0")}),-1.0]])]});
            var Q48;
            Q48=makeQuery(id+"F5.imprint","IMPRINT",FACE,{"disambiguationData":[TD([[makeQuery(id+"F5.imprint","IMPRINT",EDGE,{"derivedFrom":sQuery(id+"F5.wireOp",EDGE,"E11.0")}),-1.0]])]});
            var Q49;
            Q49=makeQuery(id+"F5.imprint","IMPRINT",FACE,{"disambiguationData":[TD([[makeQuery(id+"F5.imprint","IMPRINT",EDGE,{"derivedFrom":sQuery(id+"F5.wireOp",EDGE,"E12.0")}),-1.0]])]});
            extrude(context, id + "F6", {"entities" : qUnion([Q0, Q1, Q2, Q3, Q4, Q5, Q6, Q7, Q8, Q9, Q10, Q11, Q12, Q13, Q14, Q15, Q16, Q17, Q18, Q19, Q20, Q21, Q22, Q23, Q24, Q25, Q26, Q27, Q28, Q29, Q30, Q31, Q32, Q33, Q34, Q35, Q36, Q37, Q38, Q39, Q40, Q41, Q42, Q43, Q44, Q45, Q46, Q47, Q48, Q49]), "operationType" : NewBodyOperationType.REMOVE, "endBound" : BoundingType.THROUGH_ALL, "oppositeDirection" : true, "depth" : 25 * mm});
        }
        {
            var Q0;
            Q0=makeQuery(id+"F3.boolean.opBoolean","MERGE",FACE,{"derivedFrom":[makeQuery(id+"F1.opExtrude","SWEPT_FACE",FACE,{"disambiguationData":[OSD([sQuery(id+"F0.wireOp",EDGE,"E0.top")])]}),makeQuery(id+"F3.opExtrude","SWEPT_FACE",FACE,{"disambiguationData":[OSD([sQuery(id+"F2.wireOp",EDGE,"E6.top")])]})]});
            var sketch = newSketch(context, id + "F7", { "sketchPlane" : qUnion([Q0])});
            skCircle(sketch, "E14.cCircle", {"center": v(-52.5, 14.33) * mm, "radius": 4.33 * mm, "construction": true});
            skLineSegment(sketch, "E14.0", {"start": v(-45, 10) * mm, "end": v(-60, 10) * mm});
            skLineSegment(sketch, "E14.1", {"start": v(-60, 10) * mm, "end": v(-52.5, 23) * mm});
            skLineSegment(sketch, "E14.2", {"start": v(-52.5, 23) * mm, "end": v(-45, 10) * mm});
            skPoint(sketch, "E14.0.midPoint", {"position": v(-52.5, 10) * mm});
            skCircle(sketch, "E15.cCircle", {"center": v(-42, 18.66) * mm, "radius": 4.33 * mm, "construction": true});
            skLineSegment(sketch, "E15.0", {"start": v(-49.5, 23) * mm, "end": v(-34.5, 23) * mm});
            skLineSegment(sketch, "E15.1", {"start": v(-34.5, 23) * mm, "end": v(-42, 10) * mm});
            skLineSegment(sketch, "E15.2", {"start": v(-42, 10) * mm, "end": v(-49.5, 23) * mm});
            skPoint(sketch, "E15.0.midPoint", {"position": v(-42, 23) * mm});
            skCircle(sketch, "E16.cCircle", {"center": v(-31.5, 14.33) * mm, "radius": 4.33 * mm, "construction": true});
            skLineSegment(sketch, "E16.0", {"start": v(-24, 10) * mm, "end": v(-39, 10) * mm});
            skLineSegment(sketch, "E16.1", {"start": v(-39, 10) * mm, "end": v(-31.5, 23) * mm});
            skLineSegment(sketch, "E16.2", {"start": v(-31.5, 23) * mm, "end": v(-24, 10) * mm});
            skPoint(sketch, "E16.0.midPoint", {"position": v(-31.5, 10) * mm});
            skCircle(sketch, "E17.cCircle", {"center": v(-21, 18.66) * mm, "radius": 4.33 * mm, "construction": true});
            skLineSegment(sketch, "E17.0", {"start": v(-28.5, 23) * mm, "end": v(-13.5, 23) * mm});
            skLineSegment(sketch, "E17.1", {"start": v(-13.5, 23) * mm, "end": v(-21, 10) * mm});
            skLineSegment(sketch, "E17.2", {"start": v(-21, 10) * mm, "end": v(-28.5, 23) * mm});
            skPoint(sketch, "E17.0.midPoint", {"position": v(-21, 23) * mm});
            skCircle(sketch, "E18.cCircle", {"center": v(-10.5, 14.33) * mm, "radius": 4.33 * mm, "construction": true});
            skLineSegment(sketch, "E18.0", {"start": v(-3, 10) * mm, "end": v(-18, 10) * mm});
            skLineSegment(sketch, "E18.1", {"start": v(-18, 10) * mm, "end": v(-10.5, 23) * mm});
            skLineSegment(sketch, "E18.2", {"start": v(-10.5, 23) * mm, "end": v(-3, 10) * mm});
            skPoint(sketch, "E18.0.midPoint", {"position": v(-10.5, 10) * mm});
            skCircle(sketch, "E19.cCircle", {"center": v(0, 18.66) * mm, "radius": 4.33 * mm, "construction": true});
            skLineSegment(sketch, "E19.0", {"start": v(-7.5, 23) * mm, "end": v(7.5, 23) * mm});
            skLineSegment(sketch, "E19.1", {"start": v(7.5, 23) * mm, "end": v(0, 10) * mm});
            skLineSegment(sketch, "E19.2", {"start": v(0, 10) * mm, "end": v(-7.5, 23) * mm});
            skPoint(sketch, "E19.0.midPoint", {"position": v(0, 23) * mm});
            skCircle(sketch, "E20.cCircle", {"center": v(10.5, 14.33) * mm, "radius": 4.33 * mm, "construction": true});
            skLineSegment(sketch, "E20.0", {"start": v(18, 10) * mm, "end": v(3, 10) * mm});
            skLineSegment(sketch, "E20.1", {"start": v(3, 10) * mm, "end": v(10.5, 23) * mm});
            skLineSegment(sketch, "E20.2", {"start": v(10.5, 23) * mm, "end": v(18, 10) * mm});
            skPoint(sketch, "E20.0.midPoint", {"position": v(10.5, 10) * mm});
            skCircle(sketch, "E21.cCircle", {"center": v(21, 18.66) * mm, "radius": 4.33 * mm, "construction": true});
            skLineSegment(sketch, "E21.0", {"start": v(13.5, 23) * mm, "end": v(28.5, 23) * mm});
            skLineSegment(sketch, "E21.1", {"start": v(28.5, 23) * mm, "end": v(21, 10) * mm});
            skLineSegment(sketch, "E21.2", {"start": v(21, 10) * mm, "end": v(13.5, 23) * mm});
            skPoint(sketch, "E21.0.midPoint", {"position": v(21, 23) * mm});
            skCircle(sketch, "E22.cCircle", {"center": v(31.5, 14.33) * mm, "radius": 4.33 * mm, "construction": true});
            skLineSegment(sketch, "E22.0", {"start": v(39, 10) * mm, "end": v(24, 10) * mm});
            skLineSegment(sketch, "E22.1", {"start": v(24, 10) * mm, "end": v(31.5, 23) * mm});
            skLineSegment(sketch, "E22.2", {"start": v(31.5, 23) * mm, "end": v(39, 10) * mm});
            skPoint(sketch, "E22.0.midPoint", {"position": v(31.5, 10) * mm});
            skCircle(sketch, "E23.cCircle", {"center": v(42, 18.66) * mm, "radius": 4.33 * mm, "construction": true});
            skLineSegment(sketch, "E23.0", {"start": v(34.5, 23) * mm, "end": v(49.5, 23) * mm});
            skLineSegment(sketch, "E23.1", {"start": v(49.5, 23) * mm, "end": v(42, 10) * mm});
            skLineSegment(sketch, "E23.2", {"start": v(42, 10) * mm, "end": v(34.5, 23) * mm});
            skPoint(sketch, "E23.0.midPoint", {"position": v(42, 23) * mm});
            skCircle(sketch, "E24.cCircle", {"center": v(52.5, 14.33) * mm, "radius": 4.33 * mm, "construction": true});
            skLineSegment(sketch, "E24.0", {"start": v(60, 10) * mm, "end": v(45, 10) * mm});
            skLineSegment(sketch, "E24.1", {"start": v(45, 10) * mm, "end": v(52.5, 23) * mm});
            skLineSegment(sketch, "E24.2", {"start": v(52.5, 23) * mm, "end": v(60, 10) * mm});
            skPoint(sketch, "E24.0.midPoint", {"position": v(52.5, 10) * mm});
            skLineSegment(sketch, "E25.0.1.0", {"start": v(-31.5, 38.98) * mm, "end": v(-24, 25.99) * mm});
            skLineSegment(sketch, "E25.0.1.1", {"start": v(-39, 25.99) * mm, "end": v(-31.5, 38.98) * mm});
            skLineSegment(sketch, "E25.0.1.2", {"start": v(-45, 26) * mm, "end": v(-60, 26) * mm});
            skLineSegment(sketch, "E25.0.1.3", {"start": v(-34.5, 38.98) * mm, "end": v(-42, 25.99) * mm});
            skLineSegment(sketch, "E25.0.1.4", {"start": v(-49.5, 38.98) * mm, "end": v(-34.5, 38.98) * mm});
            skCircle(sketch, "E25.0.1.5", {"center": v(-52.5, 30.32) * mm, "radius": 4.33 * mm, "construction": true});
            skCircle(sketch, "E25.0.1.6", {"center": v(42, 34.65) * mm, "radius": 4.33 * mm, "construction": true});
            skLineSegment(sketch, "E25.0.1.7", {"start": v(13.5, 38.98) * mm, "end": v(28.5, 38.98) * mm});
            skCircle(sketch, "E25.0.1.8", {"center": v(-42, 34.65) * mm, "radius": 4.33 * mm, "construction": true});
            skCircle(sketch, "E25.0.1.9", {"center": v(0, 34.65) * mm, "radius": 4.33 * mm, "construction": true});
            skLineSegment(sketch, "E25.0.1.10", {"start": v(-21, 26) * mm, "end": v(-28.5, 38.98) * mm});
            skLineSegment(sketch, "E25.0.1.11", {"start": v(-13.5, 38.98) * mm, "end": v(-21, 25.99) * mm});
            skLineSegment(sketch, "E25.0.1.12", {"start": v(-28.5, 38.98) * mm, "end": v(-13.5, 38.98) * mm});
            skLineSegment(sketch, "E25.0.1.13", {"start": v(52.5, 38.98) * mm, "end": v(60, 26) * mm});
            skPoint(sketch, "E25.0.1.14", {"position": v(-42, 38.98) * mm});
            skLineSegment(sketch, "E25.0.1.15", {"start": v(-60, 26) * mm, "end": v(-52.5, 38.98) * mm});
            skLineSegment(sketch, "E25.0.1.16", {"start": v(-18, 26) * mm, "end": v(-10.5, 38.98) * mm});
            skLineSegment(sketch, "E25.0.1.17", {"start": v(28.5, 38.98) * mm, "end": v(21, 26) * mm});
            skLineSegment(sketch, "E25.0.1.18", {"start": v(-3, 26) * mm, "end": v(-18, 26) * mm});
            skCircle(sketch, "E25.0.1.19", {"center": v(31.5, 30.32) * mm, "radius": 4.33 * mm, "construction": true});
            skPoint(sketch, "E25.0.1.20", {"position": v(-31.5, 26) * mm});
            skLineSegment(sketch, "E25.0.1.21", {"start": v(7.5, 38.98) * mm, "end": v(0, 26) * mm});
            skLineSegment(sketch, "E25.0.1.22", {"start": v(18, 26) * mm, "end": v(3, 26) * mm});
            skCircle(sketch, "E25.0.1.23", {"center": v(-10.5, 30.32) * mm, "radius": 4.33 * mm, "construction": true});
            skLineSegment(sketch, "E25.0.1.24", {"start": v(24, 26) * mm, "end": v(31.5, 38.98) * mm});
            skPoint(sketch, "E25.0.1.25", {"position": v(52.5, 26) * mm});
            skLineSegment(sketch, "E25.0.1.26", {"start": v(60, 26) * mm, "end": v(45, 26) * mm});
            skPoint(sketch, "E25.0.1.27", {"position": v(0, 38.98) * mm});
            skCircle(sketch, "E25.0.1.28", {"center": v(52.5, 30.32) * mm, "radius": 4.33 * mm, "construction": true});
            skLineSegment(sketch, "E25.0.1.29", {"start": v(31.5, 38.98) * mm, "end": v(39, 26) * mm});
            skLineSegment(sketch, "E25.0.1.30", {"start": v(-7.5, 38.98) * mm, "end": v(7.5, 38.98) * mm});
            skLineSegment(sketch, "E25.0.1.31", {"start": v(42, 26) * mm, "end": v(34.5, 38.98) * mm});
            skLineSegment(sketch, "E25.0.1.32", {"start": v(0, 26) * mm, "end": v(-7.5, 38.98) * mm});
            skLineSegment(sketch, "E25.0.1.33", {"start": v(-24, 26) * mm, "end": v(-39, 26) * mm});
            skCircle(sketch, "E25.0.1.34", {"center": v(-21, 34.65) * mm, "radius": 4.33 * mm, "construction": true});
            skLineSegment(sketch, "E25.0.1.35", {"start": v(3, 25.99) * mm, "end": v(10.5, 38.98) * mm});
            skPoint(sketch, "E25.0.1.36", {"position": v(-52.5, 26) * mm});
            skLineSegment(sketch, "E25.0.1.37", {"start": v(-52.5, 38.98) * mm, "end": v(-45, 26) * mm});
            skPoint(sketch, "E25.0.1.38", {"position": v(10.5, 26) * mm});
            skLineSegment(sketch, "E25.0.1.39", {"start": v(34.5, 38.98) * mm, "end": v(49.5, 38.98) * mm});
            skCircle(sketch, "E25.0.1.40", {"center": v(21, 34.65) * mm, "radius": 4.33 * mm, "construction": true});
            skLineSegment(sketch, "E25.0.1.41", {"start": v(39, 26) * mm, "end": v(24, 26) * mm});
            skPoint(sketch, "E25.0.1.42", {"position": v(-10.5, 26) * mm});
            skLineSegment(sketch, "E25.0.1.43", {"start": v(10.5, 38.98) * mm, "end": v(18, 26) * mm});
            skLineSegment(sketch, "E25.0.1.44", {"start": v(49.5, 38.98) * mm, "end": v(42, 26) * mm});
            skLineSegment(sketch, "E25.0.1.45", {"start": v(21, 26) * mm, "end": v(13.5, 38.98) * mm});
            skPoint(sketch, "E25.0.1.46", {"position": v(-21, 38.98) * mm});
            skCircle(sketch, "E25.0.1.47", {"center": v(10.5, 30.32) * mm, "radius": 4.33 * mm, "construction": true});
            skCircle(sketch, "E25.0.1.48", {"center": v(-31.5, 30.32) * mm, "radius": 4.33 * mm, "construction": true});
            skLineSegment(sketch, "E25.0.1.49", {"start": v(-42, 25.99) * mm, "end": v(-49.5, 38.98) * mm});
            skLineSegment(sketch, "E25.0.1.50", {"start": v(-10.5, 38.98) * mm, "end": v(-3, 26) * mm});
            skPoint(sketch, "E25.0.1.51", {"position": v(31.5, 26) * mm});
            skPoint(sketch, "E25.0.1.52", {"position": v(42, 38.98) * mm});
            skLineSegment(sketch, "E25.0.1.53", {"start": v(45, 26) * mm, "end": v(52.5, 38.98) * mm});
            skPoint(sketch, "E25.0.1.54", {"position": v(21, 38.98) * mm});
            skLineSegment(sketch, "E25.0.2.0", {"start": v(-31.5, 54.97) * mm, "end": v(-24, 41.98) * mm});
            skLineSegment(sketch, "E25.0.2.1", {"start": v(-39, 41.98) * mm, "end": v(-31.5, 54.97) * mm});
            skLineSegment(sketch, "E25.0.2.2", {"start": v(-45, 41.98) * mm, "end": v(-60, 41.98) * mm});
            skLineSegment(sketch, "E25.0.2.3", {"start": v(-34.5, 54.97) * mm, "end": v(-42, 41.98) * mm});
            skLineSegment(sketch, "E25.0.2.4", {"start": v(-49.5, 54.97) * mm, "end": v(-34.5, 54.97) * mm});
            skCircle(sketch, "E25.0.2.5", {"center": v(-52.5, 46.31) * mm, "radius": 4.33 * mm, "construction": true});
            skCircle(sketch, "E25.0.2.6", {"center": v(42, 50.64) * mm, "radius": 4.33 * mm, "construction": true});
            skLineSegment(sketch, "E25.0.2.7", {"start": v(13.5, 54.97) * mm, "end": v(28.5, 54.97) * mm});
            skCircle(sketch, "E25.0.2.8", {"center": v(-42, 50.64) * mm, "radius": 4.33 * mm, "construction": true});
            skCircle(sketch, "E25.0.2.9", {"center": v(0, 50.64) * mm, "radius": 4.33 * mm, "construction": true});
            skLineSegment(sketch, "E25.0.2.10", {"start": v(-21, 41.98) * mm, "end": v(-28.5, 54.97) * mm});
            skLineSegment(sketch, "E25.0.2.11", {"start": v(-13.5, 54.97) * mm, "end": v(-21, 41.98) * mm});
            skLineSegment(sketch, "E25.0.2.12", {"start": v(-28.5, 54.97) * mm, "end": v(-13.5, 54.97) * mm});
            skLineSegment(sketch, "E25.0.2.13", {"start": v(52.5, 54.97) * mm, "end": v(60, 41.98) * mm});
            skPoint(sketch, "E25.0.2.14", {"position": v(-42, 54.97) * mm});
            skLineSegment(sketch, "E25.0.2.15", {"start": v(-60, 41.98) * mm, "end": v(-52.5, 54.97) * mm});
            skLineSegment(sketch, "E25.0.2.16", {"start": v(-18, 41.98) * mm, "end": v(-10.5, 54.97) * mm});
            skLineSegment(sketch, "E25.0.2.17", {"start": v(28.5, 54.97) * mm, "end": v(21, 41.98) * mm});
            skLineSegment(sketch, "E25.0.2.18", {"start": v(-3, 41.98) * mm, "end": v(-18, 41.98) * mm});
            skCircle(sketch, "E25.0.2.19", {"center": v(31.5, 46.31) * mm, "radius": 4.33 * mm, "construction": true});
            skPoint(sketch, "E25.0.2.20", {"position": v(-31.5, 41.98) * mm});
            skLineSegment(sketch, "E25.0.2.21", {"start": v(7.5, 54.97) * mm, "end": v(0, 41.98) * mm});
            skLineSegment(sketch, "E25.0.2.22", {"start": v(18, 41.98) * mm, "end": v(3, 41.98) * mm});
            skCircle(sketch, "E25.0.2.23", {"center": v(-10.5, 46.31) * mm, "radius": 4.33 * mm, "construction": true});
            skLineSegment(sketch, "E25.0.2.24", {"start": v(24, 41.98) * mm, "end": v(31.5, 54.97) * mm});
            skPoint(sketch, "E25.0.2.25", {"position": v(52.5, 41.98) * mm});
            skLineSegment(sketch, "E25.0.2.26", {"start": v(60, 41.98) * mm, "end": v(45, 41.98) * mm});
            skPoint(sketch, "E25.0.2.27", {"position": v(0, 54.97) * mm});
            skCircle(sketch, "E25.0.2.28", {"center": v(52.5, 46.31) * mm, "radius": 4.33 * mm, "construction": true});
            skLineSegment(sketch, "E25.0.2.29", {"start": v(31.5, 54.97) * mm, "end": v(39, 41.98) * mm});
            skLineSegment(sketch, "E25.0.2.30", {"start": v(-7.5, 54.97) * mm, "end": v(7.5, 54.97) * mm});
            skLineSegment(sketch, "E25.0.2.31", {"start": v(42, 41.98) * mm, "end": v(34.5, 54.97) * mm});
            skLineSegment(sketch, "E25.0.2.32", {"start": v(0, 41.98) * mm, "end": v(-7.5, 54.97) * mm});
            skLineSegment(sketch, "E25.0.2.33", {"start": v(-24, 41.98) * mm, "end": v(-39, 41.98) * mm});
            skCircle(sketch, "E25.0.2.34", {"center": v(-21, 50.64) * mm, "radius": 4.33 * mm, "construction": true});
            skLineSegment(sketch, "E25.0.2.35", {"start": v(3, 41.98) * mm, "end": v(10.5, 54.97) * mm});
            skPoint(sketch, "E25.0.2.36", {"position": v(-52.5, 41.98) * mm});
            skLineSegment(sketch, "E25.0.2.37", {"start": v(-52.5, 54.97) * mm, "end": v(-45, 41.98) * mm});
            skPoint(sketch, "E25.0.2.38", {"position": v(10.5, 41.98) * mm});
            skLineSegment(sketch, "E25.0.2.39", {"start": v(34.5, 54.97) * mm, "end": v(49.5, 54.97) * mm});
            skCircle(sketch, "E25.0.2.40", {"center": v(21, 50.64) * mm, "radius": 4.33 * mm, "construction": true});
            skLineSegment(sketch, "E25.0.2.41", {"start": v(39, 41.98) * mm, "end": v(24, 41.98) * mm});
            skPoint(sketch, "E25.0.2.42", {"position": v(-10.5, 41.98) * mm});
            skLineSegment(sketch, "E25.0.2.43", {"start": v(10.5, 54.97) * mm, "end": v(18, 41.98) * mm});
            skLineSegment(sketch, "E25.0.2.44", {"start": v(49.5, 54.97) * mm, "end": v(42, 41.98) * mm});
            skLineSegment(sketch, "E25.0.2.45", {"start": v(21, 41.98) * mm, "end": v(13.5, 54.97) * mm});
            skPoint(sketch, "E25.0.2.46", {"position": v(-21, 54.97) * mm});
            skCircle(sketch, "E25.0.2.47", {"center": v(10.5, 46.31) * mm, "radius": 4.33 * mm, "construction": true});
            skCircle(sketch, "E25.0.2.48", {"center": v(-31.5, 46.31) * mm, "radius": 4.33 * mm, "construction": true});
            skLineSegment(sketch, "E25.0.2.49", {"start": v(-42, 41.98) * mm, "end": v(-49.5, 54.97) * mm});
            skLineSegment(sketch, "E25.0.2.50", {"start": v(-10.5, 54.97) * mm, "end": v(-3, 41.98) * mm});
            skPoint(sketch, "E25.0.2.51", {"position": v(31.5, 41.98) * mm});
            skPoint(sketch, "E25.0.2.52", {"position": v(42, 54.97) * mm});
            skLineSegment(sketch, "E25.0.2.53", {"start": v(45, 41.98) * mm, "end": v(52.5, 54.97) * mm});
            skPoint(sketch, "E25.0.2.54", {"position": v(21, 54.97) * mm});
            skLineSegment(sketch, "E25.0.3.0", {"start": v(-31.5, 70.96) * mm, "end": v(-24, 57.97) * mm});
            skLineSegment(sketch, "E25.0.3.1", {"start": v(-39, 57.97) * mm, "end": v(-31.5, 70.96) * mm});
            skLineSegment(sketch, "E25.0.3.2", {"start": v(-45, 57.97) * mm, "end": v(-60, 57.97) * mm});
            skLineSegment(sketch, "E25.0.3.3", {"start": v(-34.5, 70.96) * mm, "end": v(-42, 57.97) * mm});
            skLineSegment(sketch, "E25.0.3.4", {"start": v(-49.5, 70.96) * mm, "end": v(-34.5, 70.96) * mm});
            skCircle(sketch, "E25.0.3.5", {"center": v(-52.5, 62.3) * mm, "radius": 4.33 * mm, "construction": true});
            skCircle(sketch, "E25.0.3.6", {"center": v(42, 66.63) * mm, "radius": 4.33 * mm, "construction": true});
            skLineSegment(sketch, "E25.0.3.7", {"start": v(13.5, 70.96) * mm, "end": v(28.5, 70.96) * mm});
            skCircle(sketch, "E25.0.3.8", {"center": v(-42, 66.63) * mm, "radius": 4.33 * mm, "construction": true});
            skCircle(sketch, "E25.0.3.9", {"center": v(0, 66.63) * mm, "radius": 4.33 * mm, "construction": true});
            skLineSegment(sketch, "E25.0.3.10", {"start": v(-21, 57.97) * mm, "end": v(-28.5, 70.96) * mm});
            skLineSegment(sketch, "E25.0.3.11", {"start": v(-13.5, 70.96) * mm, "end": v(-21, 57.97) * mm});
            skLineSegment(sketch, "E25.0.3.12", {"start": v(-28.5, 70.96) * mm, "end": v(-13.5, 70.96) * mm});
            skLineSegment(sketch, "E25.0.3.13", {"start": v(52.5, 70.96) * mm, "end": v(60, 57.97) * mm});
            skPoint(sketch, "E25.0.3.14", {"position": v(-42, 70.96) * mm});
            skLineSegment(sketch, "E25.0.3.15", {"start": v(-60, 57.97) * mm, "end": v(-52.5, 70.96) * mm});
            skLineSegment(sketch, "E25.0.3.16", {"start": v(-18, 57.97) * mm, "end": v(-10.5, 70.96) * mm});
            skLineSegment(sketch, "E25.0.3.17", {"start": v(28.5, 70.96) * mm, "end": v(21, 57.97) * mm});
            skLineSegment(sketch, "E25.0.3.18", {"start": v(-3, 57.97) * mm, "end": v(-18, 57.97) * mm});
            skCircle(sketch, "E25.0.3.19", {"center": v(31.5, 62.3) * mm, "radius": 4.33 * mm, "construction": true});
            skPoint(sketch, "E25.0.3.20", {"position": v(-31.5, 57.97) * mm});
            skLineSegment(sketch, "E25.0.3.21", {"start": v(7.5, 70.96) * mm, "end": v(0, 57.97) * mm});
            skLineSegment(sketch, "E25.0.3.22", {"start": v(18, 57.97) * mm, "end": v(3, 57.97) * mm});
            skCircle(sketch, "E25.0.3.23", {"center": v(-10.5, 62.3) * mm, "radius": 4.33 * mm, "construction": true});
            skLineSegment(sketch, "E25.0.3.24", {"start": v(24, 57.97) * mm, "end": v(31.5, 70.96) * mm});
            skPoint(sketch, "E25.0.3.25", {"position": v(52.5, 57.97) * mm});
            skLineSegment(sketch, "E25.0.3.26", {"start": v(60, 57.97) * mm, "end": v(45, 57.97) * mm});
            skPoint(sketch, "E25.0.3.27", {"position": v(0, 70.96) * mm});
            skCircle(sketch, "E25.0.3.28", {"center": v(52.5, 62.3) * mm, "radius": 4.33 * mm, "construction": true});
            skLineSegment(sketch, "E25.0.3.29", {"start": v(31.5, 70.96) * mm, "end": v(39, 57.97) * mm});
            skLineSegment(sketch, "E25.0.3.30", {"start": v(-7.5, 70.96) * mm, "end": v(7.5, 70.96) * mm});
            skLineSegment(sketch, "E25.0.3.31", {"start": v(42, 57.97) * mm, "end": v(34.5, 70.96) * mm});
            skLineSegment(sketch, "E25.0.3.32", {"start": v(0, 57.97) * mm, "end": v(-7.5, 70.96) * mm});
            skLineSegment(sketch, "E25.0.3.33", {"start": v(-24, 57.97) * mm, "end": v(-39, 57.97) * mm});
            skCircle(sketch, "E25.0.3.34", {"center": v(-21, 66.63) * mm, "radius": 4.33 * mm, "construction": true});
            skLineSegment(sketch, "E25.0.3.35", {"start": v(3, 57.97) * mm, "end": v(10.5, 70.96) * mm});
            skPoint(sketch, "E25.0.3.36", {"position": v(-52.5, 57.97) * mm});
            skLineSegment(sketch, "E25.0.3.37", {"start": v(-52.5, 70.96) * mm, "end": v(-45, 57.97) * mm});
            skPoint(sketch, "E25.0.3.38", {"position": v(10.5, 57.97) * mm});
            skLineSegment(sketch, "E25.0.3.39", {"start": v(34.5, 70.96) * mm, "end": v(49.5, 70.96) * mm});
            skCircle(sketch, "E25.0.3.40", {"center": v(21, 66.63) * mm, "radius": 4.33 * mm, "construction": true});
            skLineSegment(sketch, "E25.0.3.41", {"start": v(39, 57.97) * mm, "end": v(24, 57.97) * mm});
            skPoint(sketch, "E25.0.3.42", {"position": v(-10.5, 57.97) * mm});
            skLineSegment(sketch, "E25.0.3.43", {"start": v(10.5, 70.96) * mm, "end": v(18, 57.97) * mm});
            skLineSegment(sketch, "E25.0.3.44", {"start": v(49.5, 70.96) * mm, "end": v(42, 57.97) * mm});
            skLineSegment(sketch, "E25.0.3.45", {"start": v(21, 57.97) * mm, "end": v(13.5, 70.96) * mm});
            skPoint(sketch, "E25.0.3.46", {"position": v(-21, 70.96) * mm});
            skCircle(sketch, "E25.0.3.47", {"center": v(10.5, 62.3) * mm, "radius": 4.33 * mm, "construction": true});
            skCircle(sketch, "E25.0.3.48", {"center": v(-31.5, 62.3) * mm, "radius": 4.33 * mm, "construction": true});
            skLineSegment(sketch, "E25.0.3.49", {"start": v(-42, 57.97) * mm, "end": v(-49.5, 70.96) * mm});
            skLineSegment(sketch, "E25.0.3.50", {"start": v(-10.5, 70.96) * mm, "end": v(-3, 57.97) * mm});
            skPoint(sketch, "E25.0.3.51", {"position": v(31.5, 57.97) * mm});
            skPoint(sketch, "E25.0.3.52", {"position": v(42, 70.96) * mm});
            skLineSegment(sketch, "E25.0.3.53", {"start": v(45, 57.97) * mm, "end": v(52.5, 70.96) * mm});
            skPoint(sketch, "E25.0.3.54", {"position": v(21, 70.96) * mm});
            skLineSegment(sketch, "E25.0.4.0", {"start": v(-31.5, 86.95) * mm, "end": v(-24, 73.96) * mm});
            skLineSegment(sketch, "E25.0.4.1", {"start": v(-39, 73.96) * mm, "end": v(-31.5, 86.95) * mm});
            skLineSegment(sketch, "E25.0.4.2", {"start": v(-45, 73.96) * mm, "end": v(-60, 73.96) * mm});
            skLineSegment(sketch, "E25.0.4.3", {"start": v(-34.5, 86.95) * mm, "end": v(-42, 73.96) * mm});
            skLineSegment(sketch, "E25.0.4.4", {"start": v(-49.5, 86.95) * mm, "end": v(-34.5, 86.95) * mm});
            skCircle(sketch, "E25.0.4.5", {"center": v(-52.5, 78.3) * mm, "radius": 4.33 * mm, "construction": true});
            skCircle(sketch, "E25.0.4.6", {"center": v(42, 82.62) * mm, "radius": 4.33 * mm, "construction": true});
            skLineSegment(sketch, "E25.0.4.7", {"start": v(13.5, 86.95) * mm, "end": v(28.5, 86.95) * mm});
            skCircle(sketch, "E25.0.4.8", {"center": v(-42, 82.62) * mm, "radius": 4.33 * mm, "construction": true});
            skCircle(sketch, "E25.0.4.9", {"center": v(0, 82.62) * mm, "radius": 4.33 * mm, "construction": true});
            skLineSegment(sketch, "E25.0.4.10", {"start": v(-21, 73.96) * mm, "end": v(-28.5, 86.95) * mm});
            skLineSegment(sketch, "E25.0.4.11", {"start": v(-13.5, 86.95) * mm, "end": v(-21, 73.96) * mm});
            skLineSegment(sketch, "E25.0.4.12", {"start": v(-28.5, 86.95) * mm, "end": v(-13.5, 86.95) * mm});
            skLineSegment(sketch, "E25.0.4.13", {"start": v(52.5, 86.95) * mm, "end": v(60, 73.96) * mm});
            skPoint(sketch, "E25.0.4.14", {"position": v(-42, 86.95) * mm});
            skLineSegment(sketch, "E25.0.4.15", {"start": v(-60, 73.96) * mm, "end": v(-52.5, 86.95) * mm});
            skLineSegment(sketch, "E25.0.4.16", {"start": v(-18, 73.96) * mm, "end": v(-10.5, 86.95) * mm});
            skLineSegment(sketch, "E25.0.4.17", {"start": v(28.5, 86.95) * mm, "end": v(21, 73.96) * mm});
            skLineSegment(sketch, "E25.0.4.18", {"start": v(-3, 73.96) * mm, "end": v(-18, 73.96) * mm});
            skCircle(sketch, "E25.0.4.19", {"center": v(31.5, 78.3) * mm, "radius": 4.33 * mm, "construction": true});
            skPoint(sketch, "E25.0.4.20", {"position": v(-31.5, 73.96) * mm});
            skLineSegment(sketch, "E25.0.4.21", {"start": v(7.5, 86.95) * mm, "end": v(0, 73.96) * mm});
            skLineSegment(sketch, "E25.0.4.22", {"start": v(18, 73.96) * mm, "end": v(3, 73.96) * mm});
            skCircle(sketch, "E25.0.4.23", {"center": v(-10.5, 78.3) * mm, "radius": 4.33 * mm, "construction": true});
            skLineSegment(sketch, "E25.0.4.24", {"start": v(24, 73.96) * mm, "end": v(31.5, 86.95) * mm});
            skPoint(sketch, "E25.0.4.25", {"position": v(52.5, 73.96) * mm});
            skLineSegment(sketch, "E25.0.4.26", {"start": v(60, 73.96) * mm, "end": v(45, 73.96) * mm});
            skPoint(sketch, "E25.0.4.27", {"position": v(0, 86.95) * mm});
            skCircle(sketch, "E25.0.4.28", {"center": v(52.5, 78.3) * mm, "radius": 4.33 * mm, "construction": true});
            skLineSegment(sketch, "E25.0.4.29", {"start": v(31.5, 86.95) * mm, "end": v(39, 73.96) * mm});
            skLineSegment(sketch, "E25.0.4.30", {"start": v(-7.5, 86.95) * mm, "end": v(7.5, 86.95) * mm});
            skLineSegment(sketch, "E25.0.4.31", {"start": v(42, 73.96) * mm, "end": v(34.5, 86.95) * mm});
            skLineSegment(sketch, "E25.0.4.32", {"start": v(0, 73.96) * mm, "end": v(-7.5, 86.95) * mm});
            skLineSegment(sketch, "E25.0.4.33", {"start": v(-24, 73.96) * mm, "end": v(-39, 73.96) * mm});
            skCircle(sketch, "E25.0.4.34", {"center": v(-21, 82.62) * mm, "radius": 4.33 * mm, "construction": true});
            skLineSegment(sketch, "E25.0.4.35", {"start": v(3, 73.96) * mm, "end": v(10.5, 86.95) * mm});
            skPoint(sketch, "E25.0.4.36", {"position": v(-52.5, 73.96) * mm});
            skLineSegment(sketch, "E25.0.4.37", {"start": v(-52.5, 86.95) * mm, "end": v(-45, 73.96) * mm});
            skPoint(sketch, "E25.0.4.38", {"position": v(10.5, 73.96) * mm});
            skLineSegment(sketch, "E25.0.4.39", {"start": v(34.5, 86.95) * mm, "end": v(49.5, 86.95) * mm});
            skCircle(sketch, "E25.0.4.40", {"center": v(21, 82.62) * mm, "radius": 4.33 * mm, "construction": true});
            skLineSegment(sketch, "E25.0.4.41", {"start": v(39, 73.96) * mm, "end": v(24, 73.96) * mm});
            skPoint(sketch, "E25.0.4.42", {"position": v(-10.5, 73.96) * mm});
            skLineSegment(sketch, "E25.0.4.43", {"start": v(10.5, 86.95) * mm, "end": v(18, 73.96) * mm});
            skLineSegment(sketch, "E25.0.4.44", {"start": v(49.5, 86.95) * mm, "end": v(42, 73.96) * mm});
            skLineSegment(sketch, "E25.0.4.45", {"start": v(21, 73.96) * mm, "end": v(13.5, 86.95) * mm});
            skPoint(sketch, "E25.0.4.46", {"position": v(-21, 86.95) * mm});
            skCircle(sketch, "E25.0.4.47", {"center": v(10.5, 78.3) * mm, "radius": 4.33 * mm, "construction": true});
            skCircle(sketch, "E25.0.4.48", {"center": v(-31.5, 78.3) * mm, "radius": 4.33 * mm, "construction": true});
            skLineSegment(sketch, "E25.0.4.49", {"start": v(-42, 73.96) * mm, "end": v(-49.5, 86.95) * mm});
            skLineSegment(sketch, "E25.0.4.50", {"start": v(-10.5, 86.95) * mm, "end": v(-3, 73.96) * mm});
            skPoint(sketch, "E25.0.4.51", {"position": v(31.5, 73.96) * mm});
            skPoint(sketch, "E25.0.4.52", {"position": v(42, 86.95) * mm});
            skLineSegment(sketch, "E25.0.4.53", {"start": v(45, 73.96) * mm, "end": v(52.5, 86.95) * mm});
            skPoint(sketch, "E25.0.4.54", {"position": v(21, 86.95) * mm});
            skLineSegment(sketch, "E25.0.5.0", {"start": v(-31.5, 102.94) * mm, "end": v(-24, 89.95) * mm});
            skLineSegment(sketch, "E25.0.5.1", {"start": v(-39, 89.95) * mm, "end": v(-31.5, 102.94) * mm});
            skLineSegment(sketch, "E25.0.5.2", {"start": v(-45, 89.95) * mm, "end": v(-60, 89.95) * mm});
            skLineSegment(sketch, "E25.0.5.3", {"start": v(-34.5, 102.94) * mm, "end": v(-42, 89.95) * mm});
            skLineSegment(sketch, "E25.0.5.4", {"start": v(-49.5, 102.94) * mm, "end": v(-34.5, 102.94) * mm});
            skCircle(sketch, "E25.0.5.5", {"center": v(-52.5, 94.28) * mm, "radius": 4.33 * mm, "construction": true});
            skCircle(sketch, "E25.0.5.6", {"center": v(42, 98.61) * mm, "radius": 4.33 * mm, "construction": true});
            skLineSegment(sketch, "E25.0.5.7", {"start": v(13.5, 102.94) * mm, "end": v(28.5, 102.94) * mm});
            skCircle(sketch, "E25.0.5.8", {"center": v(-42, 98.61) * mm, "radius": 4.33 * mm, "construction": true});
            skCircle(sketch, "E25.0.5.9", {"center": v(0, 98.61) * mm, "radius": 4.33 * mm, "construction": true});
            skLineSegment(sketch, "E25.0.5.10", {"start": v(-21, 89.95) * mm, "end": v(-28.5, 102.94) * mm});
            skLineSegment(sketch, "E25.0.5.11", {"start": v(-13.5, 102.94) * mm, "end": v(-21, 89.95) * mm});
            skLineSegment(sketch, "E25.0.5.12", {"start": v(-28.5, 102.94) * mm, "end": v(-13.5, 102.94) * mm});
            skLineSegment(sketch, "E25.0.5.13", {"start": v(52.5, 102.94) * mm, "end": v(60, 89.95) * mm});
            skPoint(sketch, "E25.0.5.14", {"position": v(-42, 102.94) * mm});
            skLineSegment(sketch, "E25.0.5.15", {"start": v(-60, 89.95) * mm, "end": v(-52.5, 102.94) * mm});
            skLineSegment(sketch, "E25.0.5.16", {"start": v(-18, 89.95) * mm, "end": v(-10.5, 102.94) * mm});
            skLineSegment(sketch, "E25.0.5.17", {"start": v(28.5, 102.94) * mm, "end": v(21, 89.95) * mm});
            skLineSegment(sketch, "E25.0.5.18", {"start": v(-3, 89.95) * mm, "end": v(-18, 89.95) * mm});
            skCircle(sketch, "E25.0.5.19", {"center": v(31.5, 94.28) * mm, "radius": 4.33 * mm, "construction": true});
            skPoint(sketch, "E25.0.5.20", {"position": v(-31.5, 89.95) * mm});
            skLineSegment(sketch, "E25.0.5.21", {"start": v(7.5, 102.94) * mm, "end": v(0, 89.95) * mm});
            skLineSegment(sketch, "E25.0.5.22", {"start": v(18, 89.95) * mm, "end": v(3, 89.95) * mm});
            skCircle(sketch, "E25.0.5.23", {"center": v(-10.5, 94.28) * mm, "radius": 4.33 * mm, "construction": true});
            skLineSegment(sketch, "E25.0.5.24", {"start": v(24, 89.95) * mm, "end": v(31.5, 102.94) * mm});
            skPoint(sketch, "E25.0.5.25", {"position": v(52.5, 89.95) * mm});
            skLineSegment(sketch, "E25.0.5.26", {"start": v(60, 89.95) * mm, "end": v(45, 89.95) * mm});
            skPoint(sketch, "E25.0.5.27", {"position": v(0, 102.94) * mm});
            skCircle(sketch, "E25.0.5.28", {"center": v(52.5, 94.28) * mm, "radius": 4.33 * mm, "construction": true});
            skLineSegment(sketch, "E25.0.5.29", {"start": v(31.5, 102.94) * mm, "end": v(39, 89.95) * mm});
            skLineSegment(sketch, "E25.0.5.30", {"start": v(-7.5, 102.94) * mm, "end": v(7.5, 102.94) * mm});
            skLineSegment(sketch, "E25.0.5.31", {"start": v(42, 89.95) * mm, "end": v(34.5, 102.94) * mm});
            skLineSegment(sketch, "E25.0.5.32", {"start": v(0, 89.95) * mm, "end": v(-7.5, 102.94) * mm});
            skLineSegment(sketch, "E25.0.5.33", {"start": v(-24, 89.95) * mm, "end": v(-39, 89.95) * mm});
            skCircle(sketch, "E25.0.5.34", {"center": v(-21, 98.61) * mm, "radius": 4.33 * mm, "construction": true});
            skLineSegment(sketch, "E25.0.5.35", {"start": v(3, 89.95) * mm, "end": v(10.5, 102.94) * mm});
            skPoint(sketch, "E25.0.5.36", {"position": v(-52.5, 89.95) * mm});
            skLineSegment(sketch, "E25.0.5.37", {"start": v(-52.5, 102.94) * mm, "end": v(-45, 89.95) * mm});
            skPoint(sketch, "E25.0.5.38", {"position": v(10.5, 89.95) * mm});
            skLineSegment(sketch, "E25.0.5.39", {"start": v(34.5, 102.94) * mm, "end": v(49.5, 102.94) * mm});
            skCircle(sketch, "E25.0.5.40", {"center": v(21, 98.61) * mm, "radius": 4.33 * mm, "construction": true});
            skLineSegment(sketch, "E25.0.5.41", {"start": v(39, 89.95) * mm, "end": v(24, 89.95) * mm});
            skPoint(sketch, "E25.0.5.42", {"position": v(-10.5, 89.95) * mm});
            skLineSegment(sketch, "E25.0.5.43", {"start": v(10.5, 102.94) * mm, "end": v(18, 89.95) * mm});
            skLineSegment(sketch, "E25.0.5.44", {"start": v(49.5, 102.94) * mm, "end": v(42, 89.95) * mm});
            skLineSegment(sketch, "E25.0.5.45", {"start": v(21, 89.95) * mm, "end": v(13.5, 102.94) * mm});
            skPoint(sketch, "E25.0.5.46", {"position": v(-21, 102.94) * mm});
            skCircle(sketch, "E25.0.5.47", {"center": v(10.5, 94.28) * mm, "radius": 4.33 * mm, "construction": true});
            skCircle(sketch, "E25.0.5.48", {"center": v(-31.5, 94.28) * mm, "radius": 4.33 * mm, "construction": true});
            skLineSegment(sketch, "E25.0.5.49", {"start": v(-42, 89.95) * mm, "end": v(-49.5, 102.94) * mm});
            skLineSegment(sketch, "E25.0.5.50", {"start": v(-10.5, 102.94) * mm, "end": v(-3, 89.95) * mm});
            skPoint(sketch, "E25.0.5.51", {"position": v(31.5, 89.95) * mm});
            skPoint(sketch, "E25.0.5.52", {"position": v(42, 102.94) * mm});
            skLineSegment(sketch, "E25.0.5.53", {"start": v(45, 89.95) * mm, "end": v(52.5, 102.94) * mm});
            skPoint(sketch, "E25.0.5.54", {"position": v(21, 102.94) * mm});
            skLineSegment(sketch, "E25.0.6.0", {"start": v(-31.5, 118.93) * mm, "end": v(-24, 105.94) * mm});
            skLineSegment(sketch, "E25.0.6.1", {"start": v(-39, 105.94) * mm, "end": v(-31.5, 118.93) * mm});
            skLineSegment(sketch, "E25.0.6.2", {"start": v(-45, 105.94) * mm, "end": v(-60, 105.94) * mm});
            skLineSegment(sketch, "E25.0.6.3", {"start": v(-34.5, 118.93) * mm, "end": v(-42, 105.94) * mm});
            skLineSegment(sketch, "E25.0.6.4", {"start": v(-49.5, 118.93) * mm, "end": v(-34.5, 118.93) * mm});
            skCircle(sketch, "E25.0.6.5", {"center": v(-52.5, 110.27) * mm, "radius": 4.33 * mm, "construction": true});
            skCircle(sketch, "E25.0.6.6", {"center": v(42, 114.6) * mm, "radius": 4.33 * mm, "construction": true});
            skLineSegment(sketch, "E25.0.6.7", {"start": v(13.5, 118.93) * mm, "end": v(28.5, 118.93) * mm});
            skCircle(sketch, "E25.0.6.8", {"center": v(-42, 114.6) * mm, "radius": 4.33 * mm, "construction": true});
            skCircle(sketch, "E25.0.6.9", {"center": v(0, 114.6) * mm, "radius": 4.33 * mm, "construction": true});
            skLineSegment(sketch, "E25.0.6.10", {"start": v(-21, 105.94) * mm, "end": v(-28.5, 118.93) * mm});
            skLineSegment(sketch, "E25.0.6.11", {"start": v(-13.5, 118.93) * mm, "end": v(-21, 105.94) * mm});
            skLineSegment(sketch, "E25.0.6.12", {"start": v(-28.5, 118.93) * mm, "end": v(-13.5, 118.93) * mm});
            skLineSegment(sketch, "E25.0.6.13", {"start": v(52.5, 118.93) * mm, "end": v(60, 105.94) * mm});
            skPoint(sketch, "E25.0.6.14", {"position": v(-42, 118.93) * mm});
            skLineSegment(sketch, "E25.0.6.15", {"start": v(-60, 105.94) * mm, "end": v(-52.5, 118.93) * mm});
            skLineSegment(sketch, "E25.0.6.16", {"start": v(-18, 105.94) * mm, "end": v(-10.5, 118.93) * mm});
            skLineSegment(sketch, "E25.0.6.17", {"start": v(28.5, 118.93) * mm, "end": v(21, 105.94) * mm});
            skLineSegment(sketch, "E25.0.6.18", {"start": v(-3, 105.94) * mm, "end": v(-18, 105.94) * mm});
            skCircle(sketch, "E25.0.6.19", {"center": v(31.5, 110.27) * mm, "radius": 4.33 * mm, "construction": true});
            skPoint(sketch, "E25.0.6.20", {"position": v(-31.5, 105.94) * mm});
            skLineSegment(sketch, "E25.0.6.21", {"start": v(7.5, 118.93) * mm, "end": v(0, 105.94) * mm});
            skLineSegment(sketch, "E25.0.6.22", {"start": v(18, 105.94) * mm, "end": v(3, 105.94) * mm});
            skCircle(sketch, "E25.0.6.23", {"center": v(-10.5, 110.27) * mm, "radius": 4.33 * mm, "construction": true});
            skLineSegment(sketch, "E25.0.6.24", {"start": v(24, 105.94) * mm, "end": v(31.5, 118.93) * mm});
            skPoint(sketch, "E25.0.6.25", {"position": v(52.5, 105.94) * mm});
            skLineSegment(sketch, "E25.0.6.26", {"start": v(60, 105.94) * mm, "end": v(45, 105.94) * mm});
            skPoint(sketch, "E25.0.6.27", {"position": v(0, 118.93) * mm});
            skCircle(sketch, "E25.0.6.28", {"center": v(52.5, 110.27) * mm, "radius": 4.33 * mm, "construction": true});
            skLineSegment(sketch, "E25.0.6.29", {"start": v(31.5, 118.93) * mm, "end": v(39, 105.94) * mm});
            skLineSegment(sketch, "E25.0.6.30", {"start": v(-7.5, 118.93) * mm, "end": v(7.5, 118.93) * mm});
            skLineSegment(sketch, "E25.0.6.31", {"start": v(42, 105.94) * mm, "end": v(34.5, 118.93) * mm});
            skLineSegment(sketch, "E25.0.6.32", {"start": v(0, 105.94) * mm, "end": v(-7.5, 118.93) * mm});
            skLineSegment(sketch, "E25.0.6.33", {"start": v(-24, 105.94) * mm, "end": v(-39, 105.94) * mm});
            skCircle(sketch, "E25.0.6.34", {"center": v(-21, 114.6) * mm, "radius": 4.33 * mm, "construction": true});
            skLineSegment(sketch, "E25.0.6.35", {"start": v(3, 105.94) * mm, "end": v(10.5, 118.93) * mm});
            skPoint(sketch, "E25.0.6.36", {"position": v(-52.5, 105.94) * mm});
            skLineSegment(sketch, "E25.0.6.37", {"start": v(-52.5, 118.93) * mm, "end": v(-45, 105.94) * mm});
            skPoint(sketch, "E25.0.6.38", {"position": v(10.5, 105.94) * mm});
            skLineSegment(sketch, "E25.0.6.39", {"start": v(34.5, 118.93) * mm, "end": v(49.5, 118.93) * mm});
            skCircle(sketch, "E25.0.6.40", {"center": v(21, 114.6) * mm, "radius": 4.33 * mm, "construction": true});
            skLineSegment(sketch, "E25.0.6.41", {"start": v(39, 105.94) * mm, "end": v(24, 105.94) * mm});
            skPoint(sketch, "E25.0.6.42", {"position": v(-10.5, 105.94) * mm});
            skLineSegment(sketch, "E25.0.6.43", {"start": v(10.5, 118.93) * mm, "end": v(18, 105.94) * mm});
            skLineSegment(sketch, "E25.0.6.44", {"start": v(49.5, 118.93) * mm, "end": v(42, 105.94) * mm});
            skLineSegment(sketch, "E25.0.6.45", {"start": v(21, 105.94) * mm, "end": v(13.5, 118.93) * mm});
            skPoint(sketch, "E25.0.6.46", {"position": v(-21, 118.93) * mm});
            skCircle(sketch, "E25.0.6.47", {"center": v(10.5, 110.27) * mm, "radius": 4.33 * mm, "construction": true});
            skCircle(sketch, "E25.0.6.48", {"center": v(-31.5, 110.27) * mm, "radius": 4.33 * mm, "construction": true});
            skLineSegment(sketch, "E25.0.6.49", {"start": v(-42, 105.94) * mm, "end": v(-49.5, 118.93) * mm});
            skLineSegment(sketch, "E25.0.6.50", {"start": v(-10.5, 118.93) * mm, "end": v(-3, 105.94) * mm});
            skPoint(sketch, "E25.0.6.51", {"position": v(31.5, 105.94) * mm});
            skPoint(sketch, "E25.0.6.52", {"position": v(42, 118.93) * mm});
            skLineSegment(sketch, "E25.0.6.53", {"start": v(45, 105.94) * mm, "end": v(52.5, 118.93) * mm});
            skPoint(sketch, "E25.0.6.54", {"position": v(21, 118.93) * mm});
            skLineSegment(sketch, "E25.0.7.0", {"start": v(-31.5, 134.92) * mm, "end": v(-24, 121.93) * mm});
            skLineSegment(sketch, "E25.0.7.1", {"start": v(-39, 121.93) * mm, "end": v(-31.5, 134.92) * mm});
            skLineSegment(sketch, "E25.0.7.2", {"start": v(-45, 121.93) * mm, "end": v(-60, 121.93) * mm});
            skLineSegment(sketch, "E25.0.7.3", {"start": v(-34.5, 134.92) * mm, "end": v(-42, 121.93) * mm});
            skLineSegment(sketch, "E25.0.7.4", {"start": v(-49.5, 134.92) * mm, "end": v(-34.5, 134.92) * mm});
            skCircle(sketch, "E25.0.7.5", {"center": v(-52.5, 126.26) * mm, "radius": 4.33 * mm, "construction": true});
            skCircle(sketch, "E25.0.7.6", {"center": v(42, 130.6) * mm, "radius": 4.33 * mm, "construction": true});
            skLineSegment(sketch, "E25.0.7.7", {"start": v(13.5, 134.92) * mm, "end": v(28.5, 134.92) * mm});
            skCircle(sketch, "E25.0.7.8", {"center": v(-42, 130.6) * mm, "radius": 4.33 * mm, "construction": true});
            skCircle(sketch, "E25.0.7.9", {"center": v(0, 130.6) * mm, "radius": 4.33 * mm, "construction": true});
            skLineSegment(sketch, "E25.0.7.10", {"start": v(-21, 121.93) * mm, "end": v(-28.5, 134.92) * mm});
            skLineSegment(sketch, "E25.0.7.11", {"start": v(-13.5, 134.92) * mm, "end": v(-21, 121.93) * mm});
            skLineSegment(sketch, "E25.0.7.12", {"start": v(-28.5, 134.92) * mm, "end": v(-13.5, 134.92) * mm});
            skLineSegment(sketch, "E25.0.7.13", {"start": v(52.5, 134.92) * mm, "end": v(60, 121.93) * mm});
            skPoint(sketch, "E25.0.7.14", {"position": v(-42, 134.92) * mm});
            skLineSegment(sketch, "E25.0.7.15", {"start": v(-60, 121.93) * mm, "end": v(-52.5, 134.92) * mm});
            skLineSegment(sketch, "E25.0.7.16", {"start": v(-18, 121.93) * mm, "end": v(-10.5, 134.92) * mm});
            skLineSegment(sketch, "E25.0.7.17", {"start": v(28.5, 134.92) * mm, "end": v(21, 121.93) * mm});
            skLineSegment(sketch, "E25.0.7.18", {"start": v(-3, 121.93) * mm, "end": v(-18, 121.93) * mm});
            skCircle(sketch, "E25.0.7.19", {"center": v(31.5, 126.26) * mm, "radius": 4.33 * mm, "construction": true});
            skPoint(sketch, "E25.0.7.20", {"position": v(-31.5, 121.93) * mm});
            skLineSegment(sketch, "E25.0.7.21", {"start": v(7.5, 134.92) * mm, "end": v(0, 121.93) * mm});
            skLineSegment(sketch, "E25.0.7.22", {"start": v(18, 121.93) * mm, "end": v(3, 121.93) * mm});
            skCircle(sketch, "E25.0.7.23", {"center": v(-10.5, 126.26) * mm, "radius": 4.33 * mm, "construction": true});
            skLineSegment(sketch, "E25.0.7.24", {"start": v(24, 121.93) * mm, "end": v(31.5, 134.92) * mm});
            skPoint(sketch, "E25.0.7.25", {"position": v(52.5, 121.93) * mm});
            skLineSegment(sketch, "E25.0.7.26", {"start": v(60, 121.93) * mm, "end": v(45, 121.93) * mm});
            skPoint(sketch, "E25.0.7.27", {"position": v(0, 134.92) * mm});
            skCircle(sketch, "E25.0.7.28", {"center": v(52.5, 126.26) * mm, "radius": 4.33 * mm, "construction": true});
            skLineSegment(sketch, "E25.0.7.29", {"start": v(31.5, 134.92) * mm, "end": v(39, 121.93) * mm});
            skLineSegment(sketch, "E25.0.7.30", {"start": v(-7.5, 134.92) * mm, "end": v(7.5, 134.92) * mm});
            skLineSegment(sketch, "E25.0.7.31", {"start": v(42, 121.93) * mm, "end": v(34.5, 134.92) * mm});
            skLineSegment(sketch, "E25.0.7.32", {"start": v(0, 121.93) * mm, "end": v(-7.5, 134.92) * mm});
            skLineSegment(sketch, "E25.0.7.33", {"start": v(-24, 121.93) * mm, "end": v(-39, 121.93) * mm});
            skCircle(sketch, "E25.0.7.34", {"center": v(-21, 130.6) * mm, "radius": 4.33 * mm, "construction": true});
            skLineSegment(sketch, "E25.0.7.35", {"start": v(3, 121.93) * mm, "end": v(10.5, 134.92) * mm});
            skPoint(sketch, "E25.0.7.36", {"position": v(-52.5, 121.93) * mm});
            skLineSegment(sketch, "E25.0.7.37", {"start": v(-52.5, 134.92) * mm, "end": v(-45, 121.93) * mm});
            skPoint(sketch, "E25.0.7.38", {"position": v(10.5, 121.93) * mm});
            skLineSegment(sketch, "E25.0.7.39", {"start": v(34.5, 134.92) * mm, "end": v(49.5, 134.92) * mm});
            skCircle(sketch, "E25.0.7.40", {"center": v(21, 130.6) * mm, "radius": 4.33 * mm, "construction": true});
            skLineSegment(sketch, "E25.0.7.41", {"start": v(39, 121.93) * mm, "end": v(24, 121.93) * mm});
            skPoint(sketch, "E25.0.7.42", {"position": v(-10.5, 121.93) * mm});
            skLineSegment(sketch, "E25.0.7.43", {"start": v(10.5, 134.92) * mm, "end": v(18, 121.93) * mm});
            skLineSegment(sketch, "E25.0.7.44", {"start": v(49.5, 134.92) * mm, "end": v(42, 121.93) * mm});
            skLineSegment(sketch, "E25.0.7.45", {"start": v(21, 121.93) * mm, "end": v(13.5, 134.92) * mm});
            skPoint(sketch, "E25.0.7.46", {"position": v(-21, 134.92) * mm});
            skCircle(sketch, "E25.0.7.47", {"center": v(10.5, 126.26) * mm, "radius": 4.33 * mm, "construction": true});
            skCircle(sketch, "E25.0.7.48", {"center": v(-31.5, 126.26) * mm, "radius": 4.33 * mm, "construction": true});
            skLineSegment(sketch, "E25.0.7.49", {"start": v(-42, 121.93) * mm, "end": v(-49.5, 134.92) * mm});
            skLineSegment(sketch, "E25.0.7.50", {"start": v(-10.5, 134.92) * mm, "end": v(-3, 121.93) * mm});
            skPoint(sketch, "E25.0.7.51", {"position": v(31.5, 121.93) * mm});
            skPoint(sketch, "E25.0.7.52", {"position": v(42, 134.92) * mm});
            skLineSegment(sketch, "E25.0.7.53", {"start": v(45, 121.93) * mm, "end": v(52.5, 134.92) * mm});
            skPoint(sketch, "E25.0.7.54", {"position": v(21, 134.92) * mm});
            skLineSegment(sketch, "E25.0.8.0", {"start": v(-31.5, 150.91) * mm, "end": v(-24, 137.92) * mm});
            skLineSegment(sketch, "E25.0.8.1", {"start": v(-39, 137.92) * mm, "end": v(-31.5, 150.91) * mm});
            skLineSegment(sketch, "E25.0.8.2", {"start": v(-45, 137.92) * mm, "end": v(-60, 137.92) * mm});
            skLineSegment(sketch, "E25.0.8.3", {"start": v(-34.5, 150.91) * mm, "end": v(-42, 137.92) * mm});
            skLineSegment(sketch, "E25.0.8.4", {"start": v(-49.5, 150.91) * mm, "end": v(-34.5, 150.91) * mm});
            skCircle(sketch, "E25.0.8.5", {"center": v(-52.5, 142.25) * mm, "radius": 4.33 * mm, "construction": true});
            skCircle(sketch, "E25.0.8.6", {"center": v(42, 146.58) * mm, "radius": 4.33 * mm, "construction": true});
            skLineSegment(sketch, "E25.0.8.7", {"start": v(13.5, 150.91) * mm, "end": v(28.5, 150.91) * mm});
            skCircle(sketch, "E25.0.8.8", {"center": v(-42, 146.58) * mm, "radius": 4.33 * mm, "construction": true});
            skCircle(sketch, "E25.0.8.9", {"center": v(0, 146.58) * mm, "radius": 4.33 * mm, "construction": true});
            skLineSegment(sketch, "E25.0.8.10", {"start": v(-21, 137.92) * mm, "end": v(-28.5, 150.91) * mm});
            skLineSegment(sketch, "E25.0.8.11", {"start": v(-13.5, 150.91) * mm, "end": v(-21, 137.92) * mm});
            skLineSegment(sketch, "E25.0.8.12", {"start": v(-28.5, 150.91) * mm, "end": v(-13.5, 150.91) * mm});
            skLineSegment(sketch, "E25.0.8.13", {"start": v(52.5, 150.91) * mm, "end": v(60, 137.92) * mm});
            skPoint(sketch, "E25.0.8.14", {"position": v(-42, 150.91) * mm});
            skLineSegment(sketch, "E25.0.8.15", {"start": v(-60, 137.92) * mm, "end": v(-52.5, 150.91) * mm});
            skLineSegment(sketch, "E25.0.8.16", {"start": v(-18, 137.92) * mm, "end": v(-10.5, 150.91) * mm});
            skLineSegment(sketch, "E25.0.8.17", {"start": v(28.5, 150.91) * mm, "end": v(21, 137.92) * mm});
            skLineSegment(sketch, "E25.0.8.18", {"start": v(-3, 137.92) * mm, "end": v(-18, 137.92) * mm});
            skCircle(sketch, "E25.0.8.19", {"center": v(31.5, 142.25) * mm, "radius": 4.33 * mm, "construction": true});
            skPoint(sketch, "E25.0.8.20", {"position": v(-31.5, 137.92) * mm});
            skLineSegment(sketch, "E25.0.8.21", {"start": v(7.5, 150.91) * mm, "end": v(0, 137.92) * mm});
            skLineSegment(sketch, "E25.0.8.22", {"start": v(18, 137.92) * mm, "end": v(3, 137.92) * mm});
            skCircle(sketch, "E25.0.8.23", {"center": v(-10.5, 142.25) * mm, "radius": 4.33 * mm, "construction": true});
            skLineSegment(sketch, "E25.0.8.24", {"start": v(24, 137.92) * mm, "end": v(31.5, 150.91) * mm});
            skPoint(sketch, "E25.0.8.25", {"position": v(52.5, 137.92) * mm});
            skLineSegment(sketch, "E25.0.8.26", {"start": v(60, 137.92) * mm, "end": v(45, 137.92) * mm});
            skPoint(sketch, "E25.0.8.27", {"position": v(0, 150.91) * mm});
            skCircle(sketch, "E25.0.8.28", {"center": v(52.5, 142.25) * mm, "radius": 4.33 * mm, "construction": true});
            skLineSegment(sketch, "E25.0.8.29", {"start": v(31.5, 150.91) * mm, "end": v(39, 137.92) * mm});
            skLineSegment(sketch, "E25.0.8.30", {"start": v(-7.5, 150.91) * mm, "end": v(7.5, 150.91) * mm});
            skLineSegment(sketch, "E25.0.8.31", {"start": v(42, 137.92) * mm, "end": v(34.5, 150.91) * mm});
            skLineSegment(sketch, "E25.0.8.32", {"start": v(0, 137.92) * mm, "end": v(-7.5, 150.91) * mm});
            skLineSegment(sketch, "E25.0.8.33", {"start": v(-24, 137.92) * mm, "end": v(-39, 137.92) * mm});
            skCircle(sketch, "E25.0.8.34", {"center": v(-21, 146.58) * mm, "radius": 4.33 * mm, "construction": true});
            skLineSegment(sketch, "E25.0.8.35", {"start": v(3, 137.92) * mm, "end": v(10.5, 150.91) * mm});
            skPoint(sketch, "E25.0.8.36", {"position": v(-52.5, 137.92) * mm});
            skLineSegment(sketch, "E25.0.8.37", {"start": v(-52.5, 150.91) * mm, "end": v(-45, 137.92) * mm});
            skPoint(sketch, "E25.0.8.38", {"position": v(10.5, 137.92) * mm});
            skLineSegment(sketch, "E25.0.8.39", {"start": v(34.5, 150.91) * mm, "end": v(49.5, 150.91) * mm});
            skCircle(sketch, "E25.0.8.40", {"center": v(21, 146.58) * mm, "radius": 4.33 * mm, "construction": true});
            skLineSegment(sketch, "E25.0.8.41", {"start": v(39, 137.92) * mm, "end": v(24, 137.92) * mm});
            skPoint(sketch, "E25.0.8.42", {"position": v(-10.5, 137.92) * mm});
            skLineSegment(sketch, "E25.0.8.43", {"start": v(10.5, 150.91) * mm, "end": v(18, 137.92) * mm});
            skLineSegment(sketch, "E25.0.8.44", {"start": v(49.5, 150.91) * mm, "end": v(42, 137.92) * mm});
            skLineSegment(sketch, "E25.0.8.45", {"start": v(21, 137.92) * mm, "end": v(13.5, 150.91) * mm});
            skPoint(sketch, "E25.0.8.46", {"position": v(-21, 150.91) * mm});
            skCircle(sketch, "E25.0.8.47", {"center": v(10.5, 142.25) * mm, "radius": 4.33 * mm, "construction": true});
            skCircle(sketch, "E25.0.8.48", {"center": v(-31.5, 142.25) * mm, "radius": 4.33 * mm, "construction": true});
            skLineSegment(sketch, "E25.0.8.49", {"start": v(-42, 137.92) * mm, "end": v(-49.5, 150.91) * mm});
            skLineSegment(sketch, "E25.0.8.50", {"start": v(-10.5, 150.91) * mm, "end": v(-3, 137.92) * mm});
            skPoint(sketch, "E25.0.8.51", {"position": v(31.5, 137.92) * mm});
            skPoint(sketch, "E25.0.8.52", {"position": v(42, 150.91) * mm});
            skLineSegment(sketch, "E25.0.8.53", {"start": v(45, 137.92) * mm, "end": v(52.5, 150.91) * mm});
            skPoint(sketch, "E25.0.8.54", {"position": v(21, 150.91) * mm});
            skLineSegment(sketch, "E25.0.9.0", {"start": v(-31.5, 166.9) * mm, "end": v(-24, 153.9) * mm});
            skLineSegment(sketch, "E25.0.9.1", {"start": v(-39, 153.91) * mm, "end": v(-31.5, 166.9) * mm});
            skLineSegment(sketch, "E25.0.9.2", {"start": v(-45, 153.91) * mm, "end": v(-60, 153.91) * mm});
            skLineSegment(sketch, "E25.0.9.3", {"start": v(-34.5, 166.9) * mm, "end": v(-42, 153.9) * mm});
            skLineSegment(sketch, "E25.0.9.4", {"start": v(-49.5, 166.9) * mm, "end": v(-34.5, 166.9) * mm});
            skCircle(sketch, "E25.0.9.5", {"center": v(-52.5, 158.24) * mm, "radius": 4.33 * mm, "construction": true});
            skCircle(sketch, "E25.0.9.6", {"center": v(42, 162.57) * mm, "radius": 4.33 * mm, "construction": true});
            skLineSegment(sketch, "E25.0.9.7", {"start": v(13.5, 166.9) * mm, "end": v(28.5, 166.9) * mm});
            skCircle(sketch, "E25.0.9.8", {"center": v(-42, 162.57) * mm, "radius": 4.33 * mm, "construction": true});
            skCircle(sketch, "E25.0.9.9", {"center": v(0, 162.57) * mm, "radius": 4.33 * mm, "construction": true});
            skLineSegment(sketch, "E25.0.9.10", {"start": v(-21, 153.91) * mm, "end": v(-28.5, 166.9) * mm});
            skLineSegment(sketch, "E25.0.9.11", {"start": v(-13.5, 166.9) * mm, "end": v(-21, 153.9) * mm});
            skLineSegment(sketch, "E25.0.9.12", {"start": v(-28.5, 166.9) * mm, "end": v(-13.5, 166.9) * mm});
            skLineSegment(sketch, "E25.0.9.13", {"start": v(52.5, 166.9) * mm, "end": v(60, 153.9) * mm});
            skPoint(sketch, "E25.0.9.14", {"position": v(-42, 166.9) * mm});
            skLineSegment(sketch, "E25.0.9.15", {"start": v(-60, 153.91) * mm, "end": v(-52.5, 166.9) * mm});
            skLineSegment(sketch, "E25.0.9.16", {"start": v(-18, 153.91) * mm, "end": v(-10.5, 166.9) * mm});
            skLineSegment(sketch, "E25.0.9.17", {"start": v(28.5, 166.9) * mm, "end": v(21, 153.91) * mm});
            skLineSegment(sketch, "E25.0.9.18", {"start": v(-3, 153.91) * mm, "end": v(-18, 153.91) * mm});
            skCircle(sketch, "E25.0.9.19", {"center": v(31.5, 158.24) * mm, "radius": 4.33 * mm, "construction": true});
            skPoint(sketch, "E25.0.9.20", {"position": v(-31.5, 153.91) * mm});
            skLineSegment(sketch, "E25.0.9.21", {"start": v(7.5, 166.9) * mm, "end": v(0, 153.91) * mm});
            skLineSegment(sketch, "E25.0.9.22", {"start": v(18, 153.91) * mm, "end": v(3, 153.91) * mm});
            skCircle(sketch, "E25.0.9.23", {"center": v(-10.5, 158.24) * mm, "radius": 4.33 * mm, "construction": true});
            skLineSegment(sketch, "E25.0.9.24", {"start": v(24, 153.91) * mm, "end": v(31.5, 166.9) * mm});
            skPoint(sketch, "E25.0.9.25", {"position": v(52.5, 153.91) * mm});
            skLineSegment(sketch, "E25.0.9.26", {"start": v(60, 153.91) * mm, "end": v(45, 153.91) * mm});
            skPoint(sketch, "E25.0.9.27", {"position": v(0, 166.9) * mm});
            skCircle(sketch, "E25.0.9.28", {"center": v(52.5, 158.24) * mm, "radius": 4.33 * mm, "construction": true});
            skLineSegment(sketch, "E25.0.9.29", {"start": v(31.5, 166.9) * mm, "end": v(39, 153.91) * mm});
            skLineSegment(sketch, "E25.0.9.30", {"start": v(-7.5, 166.9) * mm, "end": v(7.5, 166.9) * mm});
            skLineSegment(sketch, "E25.0.9.31", {"start": v(42, 153.91) * mm, "end": v(34.5, 166.9) * mm});
            skLineSegment(sketch, "E25.0.9.32", {"start": v(0, 153.91) * mm, "end": v(-7.5, 166.9) * mm});
            skLineSegment(sketch, "E25.0.9.33", {"start": v(-24, 153.91) * mm, "end": v(-39, 153.91) * mm});
            skCircle(sketch, "E25.0.9.34", {"center": v(-21, 162.57) * mm, "radius": 4.33 * mm, "construction": true});
            skLineSegment(sketch, "E25.0.9.35", {"start": v(3, 153.91) * mm, "end": v(10.5, 166.9) * mm});
            skPoint(sketch, "E25.0.9.36", {"position": v(-52.5, 153.91) * mm});
            skLineSegment(sketch, "E25.0.9.37", {"start": v(-52.5, 166.9) * mm, "end": v(-45, 153.91) * mm});
            skPoint(sketch, "E25.0.9.38", {"position": v(10.5, 153.91) * mm});
            skLineSegment(sketch, "E25.0.9.39", {"start": v(34.5, 166.9) * mm, "end": v(49.5, 166.9) * mm});
            skCircle(sketch, "E25.0.9.40", {"center": v(21, 162.57) * mm, "radius": 4.33 * mm, "construction": true});
            skLineSegment(sketch, "E25.0.9.41", {"start": v(39, 153.91) * mm, "end": v(24, 153.91) * mm});
            skPoint(sketch, "E25.0.9.42", {"position": v(-10.5, 153.91) * mm});
            skLineSegment(sketch, "E25.0.9.43", {"start": v(10.5, 166.9) * mm, "end": v(18, 153.91) * mm});
            skLineSegment(sketch, "E25.0.9.44", {"start": v(49.5, 166.9) * mm, "end": v(42, 153.91) * mm});
            skLineSegment(sketch, "E25.0.9.45", {"start": v(21, 153.9) * mm, "end": v(13.5, 166.9) * mm});
            skPoint(sketch, "E25.0.9.46", {"position": v(-21, 166.9) * mm});
            skCircle(sketch, "E25.0.9.47", {"center": v(10.5, 158.24) * mm, "radius": 4.33 * mm, "construction": true});
            skCircle(sketch, "E25.0.9.48", {"center": v(-31.5, 158.24) * mm, "radius": 4.33 * mm, "construction": true});
            skLineSegment(sketch, "E25.0.9.49", {"start": v(-42, 153.91) * mm, "end": v(-49.5, 166.9) * mm});
            skLineSegment(sketch, "E25.0.9.50", {"start": v(-10.5, 166.9) * mm, "end": v(-3, 153.91) * mm});
            skPoint(sketch, "E25.0.9.51", {"position": v(31.5, 153.91) * mm});
            skPoint(sketch, "E25.0.9.52", {"position": v(42, 166.9) * mm});
            skLineSegment(sketch, "E25.0.9.53", {"start": v(45, 153.91) * mm, "end": v(52.5, 166.9) * mm});
            skPoint(sketch, "E25.0.9.54", {"position": v(21, 166.9) * mm});
            skLineSegment(sketch, "E25.direction1", {"start": v(-60, 10) * mm, "end": v(-35, 10) * mm, "construction": true});
            skLineSegment(sketch, "E25.direction2", {"start": v(-60, 10) * mm, "end": v(-60, 26) * mm, "construction": true});
            skSolve(sketch);
        }
        {
            var Q0;
            Q0 = qSketchRegion(id + "F7", true);
            extrude(context, id + "F8", {"entities" : qUnion([Q0]), "operationType" : NewBodyOperationType.REMOVE, "endBound" : BoundingType.THROUGH_ALL, "oppositeDirection" : true, "depth" : 25 * mm});
        }
        {
            var Q0;
            Q0=makeQuery(id+"F3.boolean.opBoolean","MERGE",FACE,{"derivedFrom":[makeQuery(id+"F1.opExtrude","SWEPT_FACE",FACE,{"disambiguationData":[OSD([sQuery(id+"F0.wireOp",EDGE,"E0.right")])]}),makeQuery(id+"F3.opExtrude","SWEPT_FACE",FACE,{"disambiguationData":[OSD([sQuery(id+"F2.wireOp",EDGE,"E6.right")])]})]});
            var sketch = newSketch(context, id + "F9", { "sketchPlane" : qUnion([Q0])});
            skLineSegment(sketch, "E26", {"start": v(-3, 175.56) * mm, "end": v(0, 175.56) * mm});
            skLineSegment(sketch, "E27", {"start": v(0, 175.56) * mm, "end": v(3, 175.56) * mm});
            skLineSegment(sketch, "E28", {"start": v(-11, 161.7) * mm, "end": v(-8, 161.7) * mm});
            skLineSegment(sketch, "E29", {"start": v(8, 161.7) * mm, "end": v(11, 161.7) * mm});
            skSolve(sketch);
        }
        {
            var Q0;
            Q0=makeQuery(id+"F9.imprint","IMPRINT",FACE,{"disambiguationData":[TD([[makeQuery(id+"F9.imprint","IMPRINT",EDGE,{"derivedFrom":sQuery(id+"F9.wireOp",EDGE,"E26")}),-1.0]])]});
            var Q1;
            Q1=makeQuery(id+"F9.imprint","IMPRINT",FACE,{"disambiguationData":[TD([[makeQuery(id+"F9.imprint","IMPRINT",EDGE,{"derivedFrom":sQuery(id+"F9.wireOp",EDGE,"E27")}),-1.0]])]});
            extrude(context, id + "F10", {"entities" : qUnion([Q0, Q1]), "operationType" : NewBodyOperationType.REMOVE, "endBound" : BoundingType.THROUGH_ALL, "oppositeDirection" : true, "depth" : 25 * mm});
        }
    });
